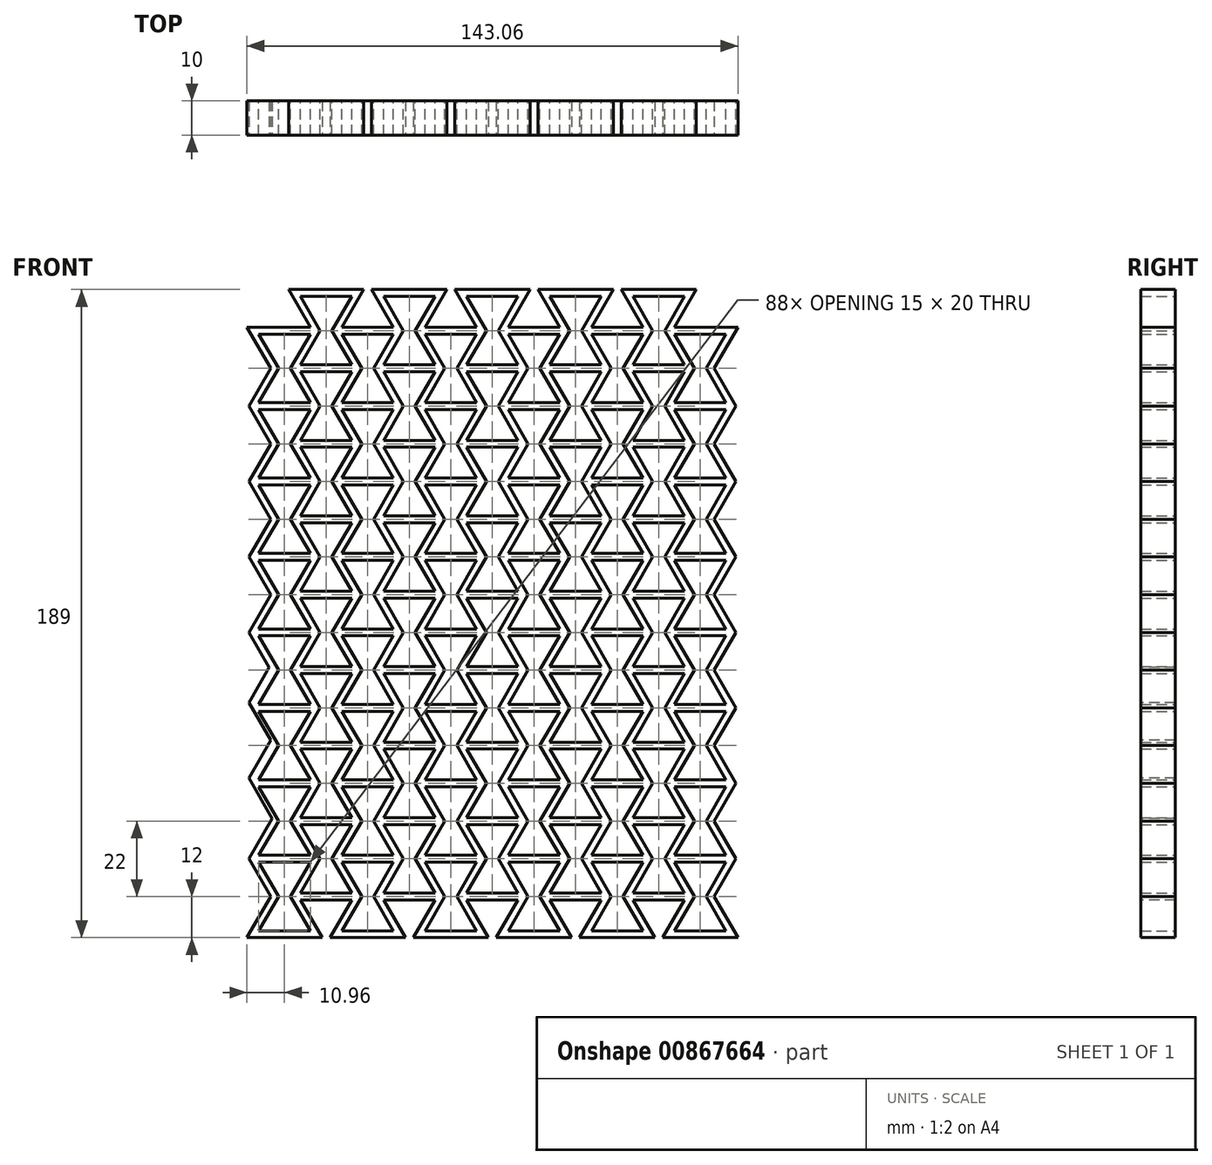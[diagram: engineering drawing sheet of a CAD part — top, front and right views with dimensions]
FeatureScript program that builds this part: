
annotation { "Feature Type Name" : "Feature", "Feature Type Description" : "" }
export const myFeature = defineFeature(function(context is Context, id is Id, definition is map)
    precondition{}
    {
        {
            var Q0;
            Q0=qCreatedBy(makeId("Front.planeOp"),FACE);
            var sketch = newSketch(context, id + "F0", { "sketchPlane" : qUnion([Q0])});
            skLineSegment(sketch, "E0", {"start": v(0, 0) * mm, "end": v(15, 0) * mm});
            skLineSegment(sketch, "E1", {"start": v(0, 20) * mm, "end": v(15, 20) * mm});
            skLineSegment(sketch, "E2", {"start": v(0, 20) * mm, "end": v(5.77, 10) * mm});
            skLineSegment(sketch, "E3", {"start": v(5.77, 10) * mm, "end": v(0, 0) * mm});
            skLineSegment(sketch, "E4", {"start": v(15, 20) * mm, "end": v(9.23, 10) * mm});
            skLineSegment(sketch, "E5", {"start": v(9.23, 10) * mm, "end": v(15, 0) * mm});
            skPoint(sketch, "E6", {"position": v(7.5, 21) * mm});
            skPoint(sketch, "E6.positionSnap0", {"position": v(7.5, 20) * mm});
            skPoint(sketch, "E7", {"position": v(7.5, -1) * mm});
            skPoint(sketch, "E7.positionSnap0", {"position": v(7.5, 0) * mm});
            skPoint(sketch, "E8", {"position": v(1.44, 4.5) * mm});
            skPoint(sketch, "E9", {"position": v(13.56, 4.5) * mm});
            skPoint(sketch, "E10", {"position": v(13.66, 15.67) * mm});
            skPoint(sketch, "E11", {"position": v(0.66, 16.85) * mm});
            skLineSegment(sketch, "E12", {"start": v(10.38, 10) * mm, "end": v(10.04, 10.6) * mm});
            skPoint(sketch, "E13", {"position": v(-1.73, 21) * mm});
            skPoint(sketch, "E14", {"position": v(16.73, 21) * mm});
            skPoint(sketch, "E15", {"position": v(4.62, 10) * mm});
            skPoint(sketch, "E16", {"position": v(10.38, 10) * mm});
            skPoint(sketch, "E17", {"position": v(-1.73, -1) * mm});
            skPoint(sketch, "E18", {"position": v(16.73, -1) * mm});
            skLineSegment(sketch, "E19", {"start": v(0, 22) * mm, "end": v(15, 22) * mm});
            skLineSegment(sketch, "E20", {"start": v(0, 42) * mm, "end": v(15, 42) * mm});
            skLineSegment(sketch, "E21", {"start": v(0, 42) * mm, "end": v(5.77, 32) * mm});
            skLineSegment(sketch, "E22", {"start": v(5.77, 32) * mm, "end": v(0, 22) * mm});
            skLineSegment(sketch, "E23", {"start": v(15, 42) * mm, "end": v(9.23, 32) * mm});
            skLineSegment(sketch, "E24", {"start": v(9.23, 32) * mm, "end": v(15, 22) * mm});
            skPoint(sketch, "E25", {"position": v(7.5, 43) * mm});
            skPoint(sketch, "E25.positionSnap0", {"position": v(7.5, 42) * mm});
            skPoint(sketch, "E26.positionSnap0", {"position": v(7.5, 22) * mm});
            skPoint(sketch, "E27", {"position": v(1.44, 26.5) * mm});
            skPoint(sketch, "E28", {"position": v(13.56, 26.5) * mm});
            skPoint(sketch, "E29", {"position": v(13.66, 37.67) * mm});
            skPoint(sketch, "E30", {"position": v(0.66, 38.85) * mm});
            skLineSegment(sketch, "E31", {"start": v(10.38, 32) * mm, "end": v(10.04, 32.6) * mm});
            skPoint(sketch, "E32", {"position": v(-1.73, 43) * mm});
            skPoint(sketch, "E33", {"position": v(16.73, 43) * mm});
            skPoint(sketch, "E34", {"position": v(4.62, 32) * mm});
            skPoint(sketch, "E35", {"position": v(10.38, 32) * mm});
            skLineSegment(sketch, "E36", {"start": v(0, 44) * mm, "end": v(15, 44) * mm});
            skLineSegment(sketch, "E37", {"start": v(0, 64) * mm, "end": v(15, 64) * mm});
            skLineSegment(sketch, "E38", {"start": v(0, 64) * mm, "end": v(5.77, 54) * mm});
            skLineSegment(sketch, "E39", {"start": v(5.77, 54) * mm, "end": v(0, 44) * mm});
            skLineSegment(sketch, "E40", {"start": v(15, 64) * mm, "end": v(9.23, 54) * mm});
            skLineSegment(sketch, "E41", {"start": v(9.23, 54) * mm, "end": v(15, 44) * mm});
            skPoint(sketch, "E42", {"position": v(7.5, 65) * mm});
            skPoint(sketch, "E42.positionSnap0", {"position": v(7.5, 64) * mm});
            skPoint(sketch, "E43.positionSnap0", {"position": v(7.5, 44) * mm});
            skPoint(sketch, "E44", {"position": v(1.44, 48.5) * mm});
            skPoint(sketch, "E45", {"position": v(13.56, 48.5) * mm});
            skPoint(sketch, "E46", {"position": v(13.66, 59.67) * mm});
            skPoint(sketch, "E47", {"position": v(0.66, 60.85) * mm});
            skLineSegment(sketch, "E48", {"start": v(10.38, 54) * mm, "end": v(10.04, 54.6) * mm});
            skPoint(sketch, "E49", {"position": v(-1.73, 65) * mm});
            skPoint(sketch, "E50", {"position": v(16.73, 65) * mm});
            skPoint(sketch, "E51", {"position": v(4.62, 54) * mm});
            skPoint(sketch, "E52", {"position": v(10.38, 54) * mm});
            skLineSegment(sketch, "E53", {"start": v(0, 66) * mm, "end": v(15, 66) * mm});
            skLineSegment(sketch, "E54", {"start": v(0, 86) * mm, "end": v(15, 86) * mm});
            skLineSegment(sketch, "E55", {"start": v(0, 86) * mm, "end": v(5.77, 76) * mm});
            skLineSegment(sketch, "E56", {"start": v(5.77, 76) * mm, "end": v(0, 66) * mm});
            skLineSegment(sketch, "E57", {"start": v(15, 86) * mm, "end": v(9.23, 76) * mm});
            skLineSegment(sketch, "E58", {"start": v(9.23, 76) * mm, "end": v(15, 66) * mm});
            skPoint(sketch, "E59", {"position": v(7.5, 87) * mm});
            skPoint(sketch, "E59.positionSnap0", {"position": v(7.5, 86) * mm});
            skPoint(sketch, "E60.positionSnap0", {"position": v(7.5, 66) * mm});
            skPoint(sketch, "E61", {"position": v(1.44, 70.5) * mm});
            skPoint(sketch, "E62", {"position": v(13.56, 70.5) * mm});
            skPoint(sketch, "E63", {"position": v(13.66, 81.67) * mm});
            skPoint(sketch, "E64", {"position": v(0.66, 82.85) * mm});
            skLineSegment(sketch, "E65", {"start": v(10.38, 76) * mm, "end": v(10.04, 76.6) * mm});
            skPoint(sketch, "E66", {"position": v(-1.73, 87) * mm});
            skPoint(sketch, "E67", {"position": v(16.73, 87) * mm});
            skPoint(sketch, "E68", {"position": v(4.62, 76) * mm});
            skPoint(sketch, "E69", {"position": v(10.38, 76) * mm});
            skLineSegment(sketch, "E70", {"start": v(0, 88) * mm, "end": v(15, 88) * mm});
            skLineSegment(sketch, "E71", {"start": v(0, 108) * mm, "end": v(15, 108) * mm});
            skLineSegment(sketch, "E72", {"start": v(0, 108) * mm, "end": v(5.77, 98) * mm});
            skLineSegment(sketch, "E73", {"start": v(5.77, 98) * mm, "end": v(0, 88) * mm});
            skLineSegment(sketch, "E74", {"start": v(15, 108) * mm, "end": v(9.23, 98) * mm});
            skLineSegment(sketch, "E75", {"start": v(9.23, 98) * mm, "end": v(15, 88) * mm});
            skPoint(sketch, "E76", {"position": v(7.5, 109) * mm});
            skPoint(sketch, "E76.positionSnap0", {"position": v(7.5, 108) * mm});
            skPoint(sketch, "E77.positionSnap0", {"position": v(7.5, 88) * mm});
            skPoint(sketch, "E78", {"position": v(1.44, 92.5) * mm});
            skPoint(sketch, "E79", {"position": v(13.56, 92.5) * mm});
            skPoint(sketch, "E80", {"position": v(13.66, 103.67) * mm});
            skPoint(sketch, "E81", {"position": v(0.66, 104.85) * mm});
            skLineSegment(sketch, "E82", {"start": v(10.38, 98) * mm, "end": v(10.04, 98.6) * mm});
            skPoint(sketch, "E83", {"position": v(-1.73, 109) * mm});
            skPoint(sketch, "E84", {"position": v(16.73, 109) * mm});
            skPoint(sketch, "E85", {"position": v(4.62, 98) * mm});
            skPoint(sketch, "E86", {"position": v(10.38, 98) * mm});
            skLineSegment(sketch, "E87", {"start": v(0, 110) * mm, "end": v(15, 110) * mm});
            skLineSegment(sketch, "E88", {"start": v(0, 130) * mm, "end": v(15, 130) * mm});
            skLineSegment(sketch, "E89", {"start": v(0, 130) * mm, "end": v(5.77, 120) * mm});
            skLineSegment(sketch, "E90", {"start": v(5.77, 120) * mm, "end": v(0, 110) * mm});
            skLineSegment(sketch, "E91", {"start": v(15, 130) * mm, "end": v(9.23, 120) * mm});
            skLineSegment(sketch, "E92", {"start": v(9.23, 120) * mm, "end": v(15, 110) * mm});
            skPoint(sketch, "E93", {"position": v(7.5, 131) * mm});
            skPoint(sketch, "E93.positionSnap0", {"position": v(7.5, 130) * mm});
            skPoint(sketch, "E94.positionSnap0", {"position": v(7.5, 110) * mm});
            skPoint(sketch, "E95", {"position": v(1.44, 114.5) * mm});
            skPoint(sketch, "E96", {"position": v(13.56, 114.5) * mm});
            skPoint(sketch, "E97", {"position": v(13.66, 125.67) * mm});
            skPoint(sketch, "E98", {"position": v(0.66, 126.85) * mm});
            skLineSegment(sketch, "E99", {"start": v(10.38, 120) * mm, "end": v(10.04, 120.6) * mm});
            skPoint(sketch, "E100", {"position": v(-1.73, 131) * mm});
            skPoint(sketch, "E101", {"position": v(16.73, 131) * mm});
            skPoint(sketch, "E102", {"position": v(4.62, 120) * mm});
            skPoint(sketch, "E103", {"position": v(10.38, 120) * mm});
            skLineSegment(sketch, "E104", {"start": v(0, 132) * mm, "end": v(15, 132) * mm});
            skLineSegment(sketch, "E105", {"start": v(0, 152) * mm, "end": v(15, 152) * mm});
            skLineSegment(sketch, "E106", {"start": v(0, 152) * mm, "end": v(5.77, 142) * mm});
            skLineSegment(sketch, "E107", {"start": v(5.77, 142) * mm, "end": v(0, 132) * mm});
            skLineSegment(sketch, "E108", {"start": v(15, 152) * mm, "end": v(9.23, 142) * mm});
            skLineSegment(sketch, "E109", {"start": v(9.23, 142) * mm, "end": v(15, 132) * mm});
            skPoint(sketch, "E110", {"position": v(7.5, 153) * mm});
            skPoint(sketch, "E110.positionSnap0", {"position": v(7.5, 152) * mm});
            skPoint(sketch, "E111.positionSnap0", {"position": v(7.5, 132) * mm});
            skPoint(sketch, "E112", {"position": v(1.44, 136.5) * mm});
            skPoint(sketch, "E113", {"position": v(13.56, 136.5) * mm});
            skPoint(sketch, "E114", {"position": v(13.66, 147.67) * mm});
            skPoint(sketch, "E115", {"position": v(0.66, 148.85) * mm});
            skLineSegment(sketch, "E116", {"start": v(10.38, 142) * mm, "end": v(10.04, 142.6) * mm});
            skPoint(sketch, "E117", {"position": v(-1.73, 153) * mm});
            skPoint(sketch, "E118", {"position": v(16.73, 153) * mm});
            skPoint(sketch, "E119", {"position": v(4.62, 142) * mm});
            skPoint(sketch, "E120", {"position": v(10.38, 142) * mm});
            skLineSegment(sketch, "E121", {"start": v(0, 154) * mm, "end": v(15, 154) * mm});
            skLineSegment(sketch, "E122", {"start": v(0, 174) * mm, "end": v(15, 174) * mm});
            skLineSegment(sketch, "E123", {"start": v(0, 174) * mm, "end": v(5.77, 164) * mm});
            skLineSegment(sketch, "E124", {"start": v(5.77, 164) * mm, "end": v(0, 154) * mm});
            skLineSegment(sketch, "E125", {"start": v(15, 174) * mm, "end": v(9.23, 164) * mm});
            skLineSegment(sketch, "E126", {"start": v(9.23, 164) * mm, "end": v(15, 154) * mm});
            skPoint(sketch, "E127", {"position": v(7.5, 175) * mm});
            skPoint(sketch, "E127.positionSnap0", {"position": v(7.5, 174) * mm});
            skPoint(sketch, "E128.positionSnap0", {"position": v(7.5, 154) * mm});
            skPoint(sketch, "E129", {"position": v(1.44, 158.5) * mm});
            skPoint(sketch, "E130", {"position": v(13.56, 158.5) * mm});
            skPoint(sketch, "E131", {"position": v(13.66, 169.67) * mm});
            skPoint(sketch, "E132", {"position": v(0.66, 170.85) * mm});
            skLineSegment(sketch, "E133", {"start": v(10.38, 164) * mm, "end": v(10.04, 164.6) * mm});
            skPoint(sketch, "E134", {"position": v(-1.73, 175) * mm});
            skPoint(sketch, "E135", {"position": v(16.73, 175) * mm});
            skPoint(sketch, "E136", {"position": v(4.62, 164) * mm});
            skPoint(sketch, "E137", {"position": v(10.38, 164) * mm});
            skLineSegment(sketch, "E138", {"start": v(12.11, 11) * mm, "end": v(27.11, 11) * mm});
            skLineSegment(sketch, "E139", {"start": v(12.11, 31) * mm, "end": v(27.11, 31) * mm});
            skLineSegment(sketch, "E140", {"start": v(12.11, 31) * mm, "end": v(17.89, 21) * mm});
            skLineSegment(sketch, "E141", {"start": v(17.89, 21) * mm, "end": v(12.11, 11) * mm});
            skLineSegment(sketch, "E142", {"start": v(27.11, 31) * mm, "end": v(21.34, 21) * mm});
            skLineSegment(sketch, "E143", {"start": v(21.34, 21) * mm, "end": v(27.11, 11) * mm});
            skPoint(sketch, "E144", {"position": v(19.61, 32) * mm});
            skPoint(sketch, "E144.positionSnap0", {"position": v(19.61, 31) * mm});
            skPoint(sketch, "E145", {"position": v(19.61, 10) * mm});
            skPoint(sketch, "E145.positionSnap0", {"position": v(19.61, 11) * mm});
            skPoint(sketch, "E146", {"position": v(13.55, 15.5) * mm});
            skPoint(sketch, "E147", {"position": v(25.67, 15.5) * mm});
            skPoint(sketch, "E148", {"position": v(25.77, 26.67) * mm});
            skPoint(sketch, "E149", {"position": v(12.78, 27.85) * mm});
            skLineSegment(sketch, "E150", {"start": v(22.5, 21) * mm, "end": v(22.15, 21.6) * mm});
            skPoint(sketch, "E151", {"position": v(28.85, 32) * mm});
            skPoint(sketch, "E152", {"position": v(22.5, 21) * mm});
            skPoint(sketch, "E153", {"position": v(28.85, 10) * mm});
            skLineSegment(sketch, "E154", {"start": v(12.11, 33) * mm, "end": v(27.11, 33) * mm});
            skLineSegment(sketch, "E155", {"start": v(12.11, 53) * mm, "end": v(27.11, 53) * mm});
            skLineSegment(sketch, "E156", {"start": v(12.11, 53) * mm, "end": v(17.89, 43) * mm});
            skLineSegment(sketch, "E157", {"start": v(17.89, 43) * mm, "end": v(12.11, 33) * mm});
            skLineSegment(sketch, "E158", {"start": v(27.11, 53) * mm, "end": v(21.34, 43) * mm});
            skLineSegment(sketch, "E159", {"start": v(21.34, 43) * mm, "end": v(27.11, 33) * mm});
            skPoint(sketch, "E160", {"position": v(19.61, 54) * mm});
            skPoint(sketch, "E160.positionSnap0", {"position": v(19.61, 53) * mm});
            skPoint(sketch, "E161.positionSnap0", {"position": v(19.61, 33) * mm});
            skPoint(sketch, "E162", {"position": v(13.55, 37.5) * mm});
            skPoint(sketch, "E163", {"position": v(25.67, 37.5) * mm});
            skPoint(sketch, "E164", {"position": v(25.77, 48.67) * mm});
            skPoint(sketch, "E165", {"position": v(12.78, 49.85) * mm});
            skLineSegment(sketch, "E166", {"start": v(22.5, 43) * mm, "end": v(22.15, 43.6) * mm});
            skPoint(sketch, "E167", {"position": v(28.85, 54) * mm});
            skPoint(sketch, "E168", {"position": v(22.5, 43) * mm});
            skLineSegment(sketch, "E169", {"start": v(12.11, 55) * mm, "end": v(27.11, 55) * mm});
            skLineSegment(sketch, "E170", {"start": v(12.11, 75) * mm, "end": v(27.11, 75) * mm});
            skLineSegment(sketch, "E171", {"start": v(12.11, 75) * mm, "end": v(17.89, 65) * mm});
            skLineSegment(sketch, "E172", {"start": v(17.89, 65) * mm, "end": v(12.11, 55) * mm});
            skLineSegment(sketch, "E173", {"start": v(27.11, 75) * mm, "end": v(21.34, 65) * mm});
            skLineSegment(sketch, "E174", {"start": v(21.34, 65) * mm, "end": v(27.11, 55) * mm});
            skPoint(sketch, "E175", {"position": v(19.61, 76) * mm});
            skPoint(sketch, "E175.positionSnap0", {"position": v(19.61, 75) * mm});
            skPoint(sketch, "E176.positionSnap0", {"position": v(19.61, 55) * mm});
            skPoint(sketch, "E177", {"position": v(13.55, 59.5) * mm});
            skPoint(sketch, "E178", {"position": v(25.67, 59.5) * mm});
            skPoint(sketch, "E179", {"position": v(25.77, 70.67) * mm});
            skPoint(sketch, "E180", {"position": v(12.78, 71.85) * mm});
            skLineSegment(sketch, "E181", {"start": v(22.5, 65) * mm, "end": v(22.15, 65.6) * mm});
            skPoint(sketch, "E182", {"position": v(28.85, 76) * mm});
            skPoint(sketch, "E183", {"position": v(22.5, 65) * mm});
            skLineSegment(sketch, "E184", {"start": v(12.11, 77) * mm, "end": v(27.11, 77) * mm});
            skLineSegment(sketch, "E185", {"start": v(12.11, 97) * mm, "end": v(27.11, 97) * mm});
            skLineSegment(sketch, "E186", {"start": v(12.11, 97) * mm, "end": v(17.89, 87) * mm});
            skLineSegment(sketch, "E187", {"start": v(17.89, 87) * mm, "end": v(12.11, 77) * mm});
            skLineSegment(sketch, "E188", {"start": v(27.11, 97) * mm, "end": v(21.34, 87) * mm});
            skLineSegment(sketch, "E189", {"start": v(21.34, 87) * mm, "end": v(27.11, 77) * mm});
            skPoint(sketch, "E190", {"position": v(19.61, 98) * mm});
            skPoint(sketch, "E190.positionSnap0", {"position": v(19.61, 97) * mm});
            skPoint(sketch, "E191.positionSnap0", {"position": v(19.61, 77) * mm});
            skPoint(sketch, "E192", {"position": v(13.55, 81.5) * mm});
            skPoint(sketch, "E193", {"position": v(25.67, 81.5) * mm});
            skPoint(sketch, "E194", {"position": v(25.77, 92.67) * mm});
            skPoint(sketch, "E195", {"position": v(12.78, 93.85) * mm});
            skLineSegment(sketch, "E196", {"start": v(22.5, 87) * mm, "end": v(22.15, 87.6) * mm});
            skPoint(sketch, "E197", {"position": v(28.85, 98) * mm});
            skPoint(sketch, "E198", {"position": v(22.5, 87) * mm});
            skLineSegment(sketch, "E199", {"start": v(12.11, 99) * mm, "end": v(27.11, 99) * mm});
            skLineSegment(sketch, "E200", {"start": v(12.11, 119) * mm, "end": v(27.11, 119) * mm});
            skLineSegment(sketch, "E201", {"start": v(12.11, 119) * mm, "end": v(17.89, 109) * mm});
            skLineSegment(sketch, "E202", {"start": v(17.89, 109) * mm, "end": v(12.11, 99) * mm});
            skLineSegment(sketch, "E203", {"start": v(27.11, 119) * mm, "end": v(21.34, 109) * mm});
            skLineSegment(sketch, "E204", {"start": v(21.34, 109) * mm, "end": v(27.11, 99) * mm});
            skPoint(sketch, "E205", {"position": v(19.61, 120) * mm});
            skPoint(sketch, "E205.positionSnap0", {"position": v(19.61, 119) * mm});
            skPoint(sketch, "E206.positionSnap0", {"position": v(19.61, 99) * mm});
            skPoint(sketch, "E207", {"position": v(13.55, 103.5) * mm});
            skPoint(sketch, "E208", {"position": v(25.67, 103.5) * mm});
            skPoint(sketch, "E209", {"position": v(25.77, 114.67) * mm});
            skPoint(sketch, "E210", {"position": v(12.78, 115.85) * mm});
            skLineSegment(sketch, "E211", {"start": v(22.5, 109) * mm, "end": v(22.15, 109.6) * mm});
            skPoint(sketch, "E212", {"position": v(28.85, 120) * mm});
            skPoint(sketch, "E213", {"position": v(22.5, 109) * mm});
            skLineSegment(sketch, "E214", {"start": v(12.11, 121) * mm, "end": v(27.11, 121) * mm});
            skLineSegment(sketch, "E215", {"start": v(12.11, 141) * mm, "end": v(27.11, 141) * mm});
            skLineSegment(sketch, "E216", {"start": v(12.11, 141) * mm, "end": v(17.89, 131) * mm});
            skLineSegment(sketch, "E217", {"start": v(17.89, 131) * mm, "end": v(12.11, 121) * mm});
            skLineSegment(sketch, "E218", {"start": v(27.11, 141) * mm, "end": v(21.34, 131) * mm});
            skLineSegment(sketch, "E219", {"start": v(21.34, 131) * mm, "end": v(27.11, 121) * mm});
            skPoint(sketch, "E220", {"position": v(19.61, 142) * mm});
            skPoint(sketch, "E220.positionSnap0", {"position": v(19.61, 141) * mm});
            skPoint(sketch, "E221.positionSnap0", {"position": v(19.61, 121) * mm});
            skPoint(sketch, "E222", {"position": v(13.55, 125.5) * mm});
            skPoint(sketch, "E223", {"position": v(25.67, 125.5) * mm});
            skPoint(sketch, "E224", {"position": v(25.77, 136.67) * mm});
            skPoint(sketch, "E225", {"position": v(12.78, 137.85) * mm});
            skLineSegment(sketch, "E226", {"start": v(22.5, 131) * mm, "end": v(22.15, 131.6) * mm});
            skPoint(sketch, "E227", {"position": v(28.85, 142) * mm});
            skPoint(sketch, "E228", {"position": v(22.5, 131) * mm});
            skLineSegment(sketch, "E229", {"start": v(12.11, 143) * mm, "end": v(27.11, 143) * mm});
            skLineSegment(sketch, "E230", {"start": v(12.11, 163) * mm, "end": v(27.11, 163) * mm});
            skLineSegment(sketch, "E231", {"start": v(12.11, 163) * mm, "end": v(17.89, 153) * mm});
            skLineSegment(sketch, "E232", {"start": v(17.89, 153) * mm, "end": v(12.11, 143) * mm});
            skLineSegment(sketch, "E233", {"start": v(27.11, 163) * mm, "end": v(21.34, 153) * mm});
            skLineSegment(sketch, "E234", {"start": v(21.34, 153) * mm, "end": v(27.11, 143) * mm});
            skPoint(sketch, "E235", {"position": v(19.61, 164) * mm});
            skPoint(sketch, "E235.positionSnap0", {"position": v(19.61, 163) * mm});
            skPoint(sketch, "E236.positionSnap0", {"position": v(19.61, 143) * mm});
            skPoint(sketch, "E237", {"position": v(13.55, 147.5) * mm});
            skPoint(sketch, "E238", {"position": v(25.67, 147.5) * mm});
            skPoint(sketch, "E239", {"position": v(25.77, 158.67) * mm});
            skPoint(sketch, "E240", {"position": v(12.78, 159.85) * mm});
            skLineSegment(sketch, "E241", {"start": v(22.5, 153) * mm, "end": v(22.15, 153.6) * mm});
            skPoint(sketch, "E242", {"position": v(28.85, 164) * mm});
            skPoint(sketch, "E243", {"position": v(22.5, 153) * mm});
            skLineSegment(sketch, "E244", {"start": v(12.11, 165) * mm, "end": v(27.11, 165) * mm});
            skLineSegment(sketch, "E245", {"start": v(12.11, 185) * mm, "end": v(27.11, 185) * mm});
            skLineSegment(sketch, "E246", {"start": v(12.11, 185) * mm, "end": v(17.89, 175) * mm});
            skLineSegment(sketch, "E247", {"start": v(17.89, 175) * mm, "end": v(12.11, 165) * mm});
            skLineSegment(sketch, "E248", {"start": v(27.11, 185) * mm, "end": v(21.34, 175) * mm});
            skLineSegment(sketch, "E249", {"start": v(21.34, 175) * mm, "end": v(27.11, 165) * mm});
            skPoint(sketch, "E250", {"position": v(19.61, 186) * mm});
            skPoint(sketch, "E250.positionSnap0", {"position": v(19.61, 185) * mm});
            skPoint(sketch, "E251.positionSnap0", {"position": v(19.61, 165) * mm});
            skPoint(sketch, "E252", {"position": v(13.55, 169.5) * mm});
            skPoint(sketch, "E253", {"position": v(25.67, 169.5) * mm});
            skPoint(sketch, "E254", {"position": v(25.77, 180.67) * mm});
            skPoint(sketch, "E255", {"position": v(12.78, 181.85) * mm});
            skLineSegment(sketch, "E256", {"start": v(22.5, 175) * mm, "end": v(22.15, 175.6) * mm});
            skPoint(sketch, "E257", {"position": v(10.38, 186) * mm});
            skPoint(sketch, "E258", {"position": v(28.85, 186) * mm});
            skPoint(sketch, "E259", {"position": v(22.5, 175) * mm});
            skLineSegment(sketch, "E260", {"start": v(24.23, 0) * mm, "end": v(39.23, 0) * mm});
            skLineSegment(sketch, "E261", {"start": v(24.23, 20) * mm, "end": v(39.23, 20) * mm});
            skLineSegment(sketch, "E262", {"start": v(24.23, 20) * mm, "end": v(30, 10) * mm});
            skLineSegment(sketch, "E263", {"start": v(30, 10) * mm, "end": v(24.23, 0) * mm});
            skLineSegment(sketch, "E264", {"start": v(39.23, 20) * mm, "end": v(33.45, 10) * mm});
            skLineSegment(sketch, "E265", {"start": v(33.45, 10) * mm, "end": v(39.23, 0) * mm});
            skPoint(sketch, "E266", {"position": v(31.73, 21) * mm});
            skPoint(sketch, "E266.positionSnap0", {"position": v(31.73, 20) * mm});
            skPoint(sketch, "E267", {"position": v(31.73, -1) * mm});
            skPoint(sketch, "E267.positionSnap0", {"position": v(31.73, 0) * mm});
            skPoint(sketch, "E268", {"position": v(25.67, 4.5) * mm});
            skPoint(sketch, "E269", {"position": v(37.79, 4.5) * mm});
            skPoint(sketch, "E270", {"position": v(37.88, 15.67) * mm});
            skPoint(sketch, "E271", {"position": v(24.9, 16.85) * mm});
            skLineSegment(sketch, "E272", {"start": v(34.6, 10) * mm, "end": v(34.26, 10.6) * mm});
            skPoint(sketch, "E273", {"position": v(40.96, 21) * mm});
            skPoint(sketch, "E274", {"position": v(34.6, 10) * mm});
            skPoint(sketch, "E275", {"position": v(22.5, -1) * mm});
            skPoint(sketch, "E276", {"position": v(40.96, -1) * mm});
            skLineSegment(sketch, "E277", {"start": v(24.23, 22) * mm, "end": v(39.23, 22) * mm});
            skLineSegment(sketch, "E278", {"start": v(24.23, 42) * mm, "end": v(39.23, 42) * mm});
            skLineSegment(sketch, "E279", {"start": v(24.23, 42) * mm, "end": v(30, 32) * mm});
            skLineSegment(sketch, "E280", {"start": v(30, 32) * mm, "end": v(24.23, 22) * mm});
            skLineSegment(sketch, "E281", {"start": v(39.23, 42) * mm, "end": v(33.45, 32) * mm});
            skLineSegment(sketch, "E282", {"start": v(33.45, 32) * mm, "end": v(39.23, 22) * mm});
            skPoint(sketch, "E283", {"position": v(31.73, 43) * mm});
            skPoint(sketch, "E283.positionSnap0", {"position": v(31.73, 42) * mm});
            skPoint(sketch, "E284.positionSnap0", {"position": v(31.73, 22) * mm});
            skPoint(sketch, "E285", {"position": v(25.67, 26.5) * mm});
            skPoint(sketch, "E286", {"position": v(37.79, 26.5) * mm});
            skPoint(sketch, "E287", {"position": v(37.88, 37.67) * mm});
            skPoint(sketch, "E288", {"position": v(24.9, 38.85) * mm});
            skLineSegment(sketch, "E289", {"start": v(34.6, 32) * mm, "end": v(34.26, 32.6) * mm});
            skPoint(sketch, "E290", {"position": v(40.96, 43) * mm});
            skPoint(sketch, "E291", {"position": v(34.6, 32) * mm});
            skLineSegment(sketch, "E292", {"start": v(24.23, 44) * mm, "end": v(39.23, 44) * mm});
            skLineSegment(sketch, "E293", {"start": v(24.23, 64) * mm, "end": v(39.23, 64) * mm});
            skLineSegment(sketch, "E294", {"start": v(24.23, 64) * mm, "end": v(30, 54) * mm});
            skLineSegment(sketch, "E295", {"start": v(30, 54) * mm, "end": v(24.23, 44) * mm});
            skLineSegment(sketch, "E296", {"start": v(39.23, 64) * mm, "end": v(33.45, 54) * mm});
            skLineSegment(sketch, "E297", {"start": v(33.45, 54) * mm, "end": v(39.23, 44) * mm});
            skPoint(sketch, "E298", {"position": v(31.73, 65) * mm});
            skPoint(sketch, "E298.positionSnap0", {"position": v(31.73, 64) * mm});
            skPoint(sketch, "E299.positionSnap0", {"position": v(31.73, 44) * mm});
            skPoint(sketch, "E300", {"position": v(25.67, 48.5) * mm});
            skPoint(sketch, "E301", {"position": v(37.79, 48.5) * mm});
            skPoint(sketch, "E302", {"position": v(37.88, 59.67) * mm});
            skPoint(sketch, "E303", {"position": v(24.9, 60.85) * mm});
            skLineSegment(sketch, "E304", {"start": v(34.6, 54) * mm, "end": v(34.26, 54.6) * mm});
            skPoint(sketch, "E305", {"position": v(40.96, 65) * mm});
            skPoint(sketch, "E306", {"position": v(34.6, 54) * mm});
            skLineSegment(sketch, "E307", {"start": v(24.23, 66) * mm, "end": v(39.23, 66) * mm});
            skLineSegment(sketch, "E308", {"start": v(24.23, 86) * mm, "end": v(39.23, 86) * mm});
            skLineSegment(sketch, "E309", {"start": v(24.23, 86) * mm, "end": v(30, 76) * mm});
            skLineSegment(sketch, "E310", {"start": v(30, 76) * mm, "end": v(24.23, 66) * mm});
            skLineSegment(sketch, "E311", {"start": v(39.23, 86) * mm, "end": v(33.45, 76) * mm});
            skLineSegment(sketch, "E312", {"start": v(33.45, 76) * mm, "end": v(39.23, 66) * mm});
            skPoint(sketch, "E313", {"position": v(31.73, 87) * mm});
            skPoint(sketch, "E313.positionSnap0", {"position": v(31.73, 86) * mm});
            skPoint(sketch, "E314.positionSnap0", {"position": v(31.73, 66) * mm});
            skPoint(sketch, "E315", {"position": v(25.67, 70.5) * mm});
            skPoint(sketch, "E316", {"position": v(37.79, 70.5) * mm});
            skPoint(sketch, "E317", {"position": v(37.88, 81.67) * mm});
            skPoint(sketch, "E318", {"position": v(24.9, 82.85) * mm});
            skLineSegment(sketch, "E319", {"start": v(34.6, 76) * mm, "end": v(34.26, 76.6) * mm});
            skPoint(sketch, "E320", {"position": v(40.96, 87) * mm});
            skPoint(sketch, "E321", {"position": v(34.6, 76) * mm});
            skLineSegment(sketch, "E322", {"start": v(24.23, 88) * mm, "end": v(39.23, 88) * mm});
            skLineSegment(sketch, "E323", {"start": v(24.23, 108) * mm, "end": v(39.23, 108) * mm});
            skLineSegment(sketch, "E324", {"start": v(24.23, 108) * mm, "end": v(30, 98) * mm});
            skLineSegment(sketch, "E325", {"start": v(30, 98) * mm, "end": v(24.23, 88) * mm});
            skLineSegment(sketch, "E326", {"start": v(39.23, 108) * mm, "end": v(33.45, 98) * mm});
            skLineSegment(sketch, "E327", {"start": v(33.45, 98) * mm, "end": v(39.23, 88) * mm});
            skPoint(sketch, "E328", {"position": v(31.73, 109) * mm});
            skPoint(sketch, "E328.positionSnap0", {"position": v(31.73, 108) * mm});
            skPoint(sketch, "E329.positionSnap0", {"position": v(31.73, 88) * mm});
            skPoint(sketch, "E330", {"position": v(25.67, 92.5) * mm});
            skPoint(sketch, "E331", {"position": v(37.79, 92.5) * mm});
            skPoint(sketch, "E332", {"position": v(37.88, 103.67) * mm});
            skPoint(sketch, "E333", {"position": v(24.9, 104.85) * mm});
            skLineSegment(sketch, "E334", {"start": v(34.6, 98) * mm, "end": v(34.26, 98.6) * mm});
            skPoint(sketch, "E335", {"position": v(40.96, 109) * mm});
            skPoint(sketch, "E336", {"position": v(34.6, 98) * mm});
            skLineSegment(sketch, "E337", {"start": v(24.23, 110) * mm, "end": v(39.23, 110) * mm});
            skLineSegment(sketch, "E338", {"start": v(24.23, 130) * mm, "end": v(39.23, 130) * mm});
            skLineSegment(sketch, "E339", {"start": v(24.23, 130) * mm, "end": v(30, 120) * mm});
            skLineSegment(sketch, "E340", {"start": v(30, 120) * mm, "end": v(24.23, 110) * mm});
            skLineSegment(sketch, "E341", {"start": v(39.23, 130) * mm, "end": v(33.45, 120) * mm});
            skLineSegment(sketch, "E342", {"start": v(33.45, 120) * mm, "end": v(39.23, 110) * mm});
            skPoint(sketch, "E343", {"position": v(31.73, 131) * mm});
            skPoint(sketch, "E343.positionSnap0", {"position": v(31.73, 130) * mm});
            skPoint(sketch, "E344.positionSnap0", {"position": v(31.73, 110) * mm});
            skPoint(sketch, "E345", {"position": v(25.67, 114.5) * mm});
            skPoint(sketch, "E346", {"position": v(37.79, 114.5) * mm});
            skPoint(sketch, "E347", {"position": v(37.88, 125.67) * mm});
            skPoint(sketch, "E348", {"position": v(24.9, 126.85) * mm});
            skLineSegment(sketch, "E349", {"start": v(34.6, 120) * mm, "end": v(34.26, 120.6) * mm});
            skPoint(sketch, "E350", {"position": v(40.96, 131) * mm});
            skPoint(sketch, "E351", {"position": v(34.6, 120) * mm});
            skLineSegment(sketch, "E352", {"start": v(24.23, 132) * mm, "end": v(39.23, 132) * mm});
            skLineSegment(sketch, "E353", {"start": v(24.23, 152) * mm, "end": v(39.23, 152) * mm});
            skLineSegment(sketch, "E354", {"start": v(24.23, 152) * mm, "end": v(30, 142) * mm});
            skLineSegment(sketch, "E355", {"start": v(30, 142) * mm, "end": v(24.23, 132) * mm});
            skLineSegment(sketch, "E356", {"start": v(39.23, 152) * mm, "end": v(33.45, 142) * mm});
            skLineSegment(sketch, "E357", {"start": v(33.45, 142) * mm, "end": v(39.23, 132) * mm});
            skPoint(sketch, "E358", {"position": v(31.73, 153) * mm});
            skPoint(sketch, "E358.positionSnap0", {"position": v(31.73, 152) * mm});
            skPoint(sketch, "E359.positionSnap0", {"position": v(31.73, 132) * mm});
            skPoint(sketch, "E360", {"position": v(25.67, 136.5) * mm});
            skPoint(sketch, "E361", {"position": v(37.79, 136.5) * mm});
            skPoint(sketch, "E362", {"position": v(37.88, 147.67) * mm});
            skPoint(sketch, "E363", {"position": v(24.9, 148.85) * mm});
            skLineSegment(sketch, "E364", {"start": v(34.6, 142) * mm, "end": v(34.26, 142.6) * mm});
            skPoint(sketch, "E365", {"position": v(40.96, 153) * mm});
            skPoint(sketch, "E366", {"position": v(34.6, 142) * mm});
            skLineSegment(sketch, "E367", {"start": v(24.23, 154) * mm, "end": v(39.23, 154) * mm});
            skLineSegment(sketch, "E368", {"start": v(24.23, 174) * mm, "end": v(39.23, 174) * mm});
            skLineSegment(sketch, "E369", {"start": v(24.23, 174) * mm, "end": v(30, 164) * mm});
            skLineSegment(sketch, "E370", {"start": v(30, 164) * mm, "end": v(24.23, 154) * mm});
            skLineSegment(sketch, "E371", {"start": v(39.23, 174) * mm, "end": v(33.45, 164) * mm});
            skLineSegment(sketch, "E372", {"start": v(33.45, 164) * mm, "end": v(39.23, 154) * mm});
            skPoint(sketch, "E373", {"position": v(31.73, 175) * mm});
            skPoint(sketch, "E373.positionSnap0", {"position": v(31.73, 174) * mm});
            skPoint(sketch, "E374.positionSnap0", {"position": v(31.73, 154) * mm});
            skPoint(sketch, "E375", {"position": v(25.67, 158.5) * mm});
            skPoint(sketch, "E376", {"position": v(37.79, 158.5) * mm});
            skPoint(sketch, "E377", {"position": v(37.88, 169.67) * mm});
            skPoint(sketch, "E378", {"position": v(24.9, 170.85) * mm});
            skLineSegment(sketch, "E379", {"start": v(34.6, 164) * mm, "end": v(34.26, 164.6) * mm});
            skPoint(sketch, "E380", {"position": v(40.96, 175) * mm});
            skPoint(sketch, "E381", {"position": v(34.6, 164) * mm});
            skLineSegment(sketch, "E382", {"start": v(36.34, 11) * mm, "end": v(51.34, 11) * mm});
            skLineSegment(sketch, "E383", {"start": v(36.34, 31) * mm, "end": v(51.34, 31) * mm});
            skLineSegment(sketch, "E384", {"start": v(36.34, 31) * mm, "end": v(42.11, 21) * mm});
            skLineSegment(sketch, "E385", {"start": v(42.11, 21) * mm, "end": v(36.34, 11) * mm});
            skLineSegment(sketch, "E386", {"start": v(51.34, 31) * mm, "end": v(45.57, 21) * mm});
            skLineSegment(sketch, "E387", {"start": v(45.57, 21) * mm, "end": v(51.34, 11) * mm});
            skPoint(sketch, "E388", {"position": v(43.84, 32) * mm});
            skPoint(sketch, "E388.positionSnap0", {"position": v(43.84, 31) * mm});
            skPoint(sketch, "E389", {"position": v(43.84, 10) * mm});
            skPoint(sketch, "E389.positionSnap0", {"position": v(43.84, 11) * mm});
            skPoint(sketch, "E390", {"position": v(37.78, 15.5) * mm});
            skPoint(sketch, "E391", {"position": v(49.9, 15.5) * mm});
            skPoint(sketch, "E392", {"position": v(50, 26.67) * mm});
            skPoint(sketch, "E393", {"position": v(37, 27.85) * mm});
            skLineSegment(sketch, "E394", {"start": v(46.72, 21) * mm, "end": v(46.37, 21.6) * mm});
            skPoint(sketch, "E395", {"position": v(53.07, 32) * mm});
            skPoint(sketch, "E396", {"position": v(46.72, 21) * mm});
            skPoint(sketch, "E397", {"position": v(53.07, 10) * mm});
            skLineSegment(sketch, "E398", {"start": v(36.34, 33) * mm, "end": v(51.34, 33) * mm});
            skLineSegment(sketch, "E399", {"start": v(36.34, 53) * mm, "end": v(51.34, 53) * mm});
            skLineSegment(sketch, "E400", {"start": v(36.34, 53) * mm, "end": v(42.11, 43) * mm});
            skLineSegment(sketch, "E401", {"start": v(42.11, 43) * mm, "end": v(36.34, 33) * mm});
            skLineSegment(sketch, "E402", {"start": v(51.34, 53) * mm, "end": v(45.57, 43) * mm});
            skLineSegment(sketch, "E403", {"start": v(45.57, 43) * mm, "end": v(51.34, 33) * mm});
            skPoint(sketch, "E404", {"position": v(43.84, 54) * mm});
            skPoint(sketch, "E404.positionSnap0", {"position": v(43.84, 53) * mm});
            skPoint(sketch, "E405.positionSnap0", {"position": v(43.84, 33) * mm});
            skPoint(sketch, "E406", {"position": v(37.78, 37.5) * mm});
            skPoint(sketch, "E407", {"position": v(49.9, 37.5) * mm});
            skPoint(sketch, "E408", {"position": v(50, 48.67) * mm});
            skPoint(sketch, "E409", {"position": v(37, 49.85) * mm});
            skLineSegment(sketch, "E410", {"start": v(46.72, 43) * mm, "end": v(46.37, 43.6) * mm});
            skPoint(sketch, "E411", {"position": v(53.07, 54) * mm});
            skPoint(sketch, "E412", {"position": v(46.72, 43) * mm});
            skLineSegment(sketch, "E413", {"start": v(36.34, 55) * mm, "end": v(51.34, 55) * mm});
            skLineSegment(sketch, "E414", {"start": v(36.34, 75) * mm, "end": v(51.34, 75) * mm});
            skLineSegment(sketch, "E415", {"start": v(36.34, 75) * mm, "end": v(42.11, 65) * mm});
            skLineSegment(sketch, "E416", {"start": v(42.11, 65) * mm, "end": v(36.34, 55) * mm});
            skLineSegment(sketch, "E417", {"start": v(51.34, 75) * mm, "end": v(45.57, 65) * mm});
            skLineSegment(sketch, "E418", {"start": v(45.57, 65) * mm, "end": v(51.34, 55) * mm});
            skPoint(sketch, "E419", {"position": v(43.84, 76) * mm});
            skPoint(sketch, "E419.positionSnap0", {"position": v(43.84, 75) * mm});
            skPoint(sketch, "E420.positionSnap0", {"position": v(43.84, 55) * mm});
            skPoint(sketch, "E421", {"position": v(37.78, 59.5) * mm});
            skPoint(sketch, "E422", {"position": v(49.9, 59.5) * mm});
            skPoint(sketch, "E423", {"position": v(50, 70.67) * mm});
            skPoint(sketch, "E424", {"position": v(37, 71.85) * mm});
            skLineSegment(sketch, "E425", {"start": v(46.72, 65) * mm, "end": v(46.37, 65.6) * mm});
            skPoint(sketch, "E426", {"position": v(53.07, 76) * mm});
            skPoint(sketch, "E427", {"position": v(46.72, 65) * mm});
            skLineSegment(sketch, "E428", {"start": v(36.34, 77) * mm, "end": v(51.34, 77) * mm});
            skLineSegment(sketch, "E429", {"start": v(36.34, 97) * mm, "end": v(51.34, 97) * mm});
            skLineSegment(sketch, "E430", {"start": v(36.34, 97) * mm, "end": v(42.11, 87) * mm});
            skLineSegment(sketch, "E431", {"start": v(42.11, 87) * mm, "end": v(36.34, 77) * mm});
            skLineSegment(sketch, "E432", {"start": v(51.34, 97) * mm, "end": v(45.57, 87) * mm});
            skLineSegment(sketch, "E433", {"start": v(45.57, 87) * mm, "end": v(51.34, 77) * mm});
            skPoint(sketch, "E434", {"position": v(43.84, 98) * mm});
            skPoint(sketch, "E434.positionSnap0", {"position": v(43.84, 97) * mm});
            skPoint(sketch, "E435.positionSnap0", {"position": v(43.84, 77) * mm});
            skPoint(sketch, "E436", {"position": v(37.78, 81.5) * mm});
            skPoint(sketch, "E437", {"position": v(49.9, 81.5) * mm});
            skPoint(sketch, "E438", {"position": v(50, 92.67) * mm});
            skPoint(sketch, "E439", {"position": v(37, 93.85) * mm});
            skLineSegment(sketch, "E440", {"start": v(46.72, 87) * mm, "end": v(46.37, 87.6) * mm});
            skPoint(sketch, "E441", {"position": v(53.07, 98) * mm});
            skPoint(sketch, "E442", {"position": v(46.72, 87) * mm});
            skLineSegment(sketch, "E443", {"start": v(36.34, 99) * mm, "end": v(51.34, 99) * mm});
            skLineSegment(sketch, "E444", {"start": v(36.34, 119) * mm, "end": v(51.34, 119) * mm});
            skLineSegment(sketch, "E445", {"start": v(36.34, 119) * mm, "end": v(42.11, 109) * mm});
            skLineSegment(sketch, "E446", {"start": v(42.11, 109) * mm, "end": v(36.34, 99) * mm});
            skLineSegment(sketch, "E447", {"start": v(51.34, 119) * mm, "end": v(45.57, 109) * mm});
            skLineSegment(sketch, "E448", {"start": v(45.57, 109) * mm, "end": v(51.34, 99) * mm});
            skPoint(sketch, "E449", {"position": v(43.84, 120) * mm});
            skPoint(sketch, "E449.positionSnap0", {"position": v(43.84, 119) * mm});
            skPoint(sketch, "E450.positionSnap0", {"position": v(43.84, 99) * mm});
            skPoint(sketch, "E451", {"position": v(37.78, 103.5) * mm});
            skPoint(sketch, "E452", {"position": v(49.9, 103.5) * mm});
            skPoint(sketch, "E453", {"position": v(50, 114.67) * mm});
            skPoint(sketch, "E454", {"position": v(37, 115.85) * mm});
            skLineSegment(sketch, "E455", {"start": v(46.72, 109) * mm, "end": v(46.37, 109.6) * mm});
            skPoint(sketch, "E456", {"position": v(53.07, 120) * mm});
            skPoint(sketch, "E457", {"position": v(46.72, 109) * mm});
            skLineSegment(sketch, "E458", {"start": v(36.34, 121) * mm, "end": v(51.34, 121) * mm});
            skLineSegment(sketch, "E459", {"start": v(36.34, 141) * mm, "end": v(51.34, 141) * mm});
            skLineSegment(sketch, "E460", {"start": v(36.34, 141) * mm, "end": v(42.11, 131) * mm});
            skLineSegment(sketch, "E461", {"start": v(42.11, 131) * mm, "end": v(36.34, 121) * mm});
            skLineSegment(sketch, "E462", {"start": v(51.34, 141) * mm, "end": v(45.57, 131) * mm});
            skLineSegment(sketch, "E463", {"start": v(45.57, 131) * mm, "end": v(51.34, 121) * mm});
            skPoint(sketch, "E464", {"position": v(43.84, 142) * mm});
            skPoint(sketch, "E464.positionSnap0", {"position": v(43.84, 141) * mm});
            skPoint(sketch, "E465.positionSnap0", {"position": v(43.84, 121) * mm});
            skPoint(sketch, "E466", {"position": v(37.78, 125.5) * mm});
            skPoint(sketch, "E467", {"position": v(49.9, 125.5) * mm});
            skPoint(sketch, "E468", {"position": v(50, 136.67) * mm});
            skPoint(sketch, "E469", {"position": v(37, 137.85) * mm});
            skLineSegment(sketch, "E470", {"start": v(46.72, 131) * mm, "end": v(46.37, 131.6) * mm});
            skPoint(sketch, "E471", {"position": v(53.07, 142) * mm});
            skPoint(sketch, "E472", {"position": v(46.72, 131) * mm});
            skLineSegment(sketch, "E473", {"start": v(36.34, 143) * mm, "end": v(51.34, 143) * mm});
            skLineSegment(sketch, "E474", {"start": v(36.34, 163) * mm, "end": v(51.34, 163) * mm});
            skLineSegment(sketch, "E475", {"start": v(36.34, 163) * mm, "end": v(42.11, 153) * mm});
            skLineSegment(sketch, "E476", {"start": v(42.11, 153) * mm, "end": v(36.34, 143) * mm});
            skLineSegment(sketch, "E477", {"start": v(51.34, 163) * mm, "end": v(45.57, 153) * mm});
            skLineSegment(sketch, "E478", {"start": v(45.57, 153) * mm, "end": v(51.34, 143) * mm});
            skPoint(sketch, "E479", {"position": v(43.84, 164) * mm});
            skPoint(sketch, "E479.positionSnap0", {"position": v(43.84, 163) * mm});
            skPoint(sketch, "E480.positionSnap0", {"position": v(43.84, 143) * mm});
            skPoint(sketch, "E481", {"position": v(37.78, 147.5) * mm});
            skPoint(sketch, "E482", {"position": v(49.9, 147.5) * mm});
            skPoint(sketch, "E483", {"position": v(50, 158.67) * mm});
            skPoint(sketch, "E484", {"position": v(37, 159.85) * mm});
            skLineSegment(sketch, "E485", {"start": v(46.72, 153) * mm, "end": v(46.37, 153.6) * mm});
            skPoint(sketch, "E486", {"position": v(53.07, 164) * mm});
            skPoint(sketch, "E487", {"position": v(46.72, 153) * mm});
            skLineSegment(sketch, "E488", {"start": v(36.34, 165) * mm, "end": v(51.34, 165) * mm});
            skLineSegment(sketch, "E489", {"start": v(36.34, 185) * mm, "end": v(51.34, 185) * mm});
            skLineSegment(sketch, "E490", {"start": v(36.34, 185) * mm, "end": v(42.11, 175) * mm});
            skLineSegment(sketch, "E491", {"start": v(42.11, 175) * mm, "end": v(36.34, 165) * mm});
            skLineSegment(sketch, "E492", {"start": v(51.34, 185) * mm, "end": v(45.57, 175) * mm});
            skLineSegment(sketch, "E493", {"start": v(45.57, 175) * mm, "end": v(51.34, 165) * mm});
            skPoint(sketch, "E494", {"position": v(43.84, 186) * mm});
            skPoint(sketch, "E494.positionSnap0", {"position": v(43.84, 185) * mm});
            skPoint(sketch, "E495.positionSnap0", {"position": v(43.84, 165) * mm});
            skPoint(sketch, "E496", {"position": v(37.78, 169.5) * mm});
            skPoint(sketch, "E497", {"position": v(49.9, 169.5) * mm});
            skPoint(sketch, "E498", {"position": v(50, 180.67) * mm});
            skPoint(sketch, "E499", {"position": v(37, 181.85) * mm});
            skLineSegment(sketch, "E500", {"start": v(46.72, 175) * mm, "end": v(46.37, 175.6) * mm});
            skPoint(sketch, "E501", {"position": v(34.6, 186) * mm});
            skPoint(sketch, "E502", {"position": v(53.07, 186) * mm});
            skPoint(sketch, "E503", {"position": v(46.72, 175) * mm});
            skLineSegment(sketch, "E504", {"start": v(48.45, 0) * mm, "end": v(63.45, 0) * mm});
            skLineSegment(sketch, "E505", {"start": v(48.45, 20) * mm, "end": v(63.45, 20) * mm});
            skLineSegment(sketch, "E506", {"start": v(48.45, 20) * mm, "end": v(54.23, 10) * mm});
            skLineSegment(sketch, "E507", {"start": v(54.23, 10) * mm, "end": v(48.45, 0) * mm});
            skLineSegment(sketch, "E508", {"start": v(63.45, 20) * mm, "end": v(57.68, 10) * mm});
            skLineSegment(sketch, "E509", {"start": v(57.68, 10) * mm, "end": v(63.45, 0) * mm});
            skPoint(sketch, "E510", {"position": v(55.95, 21) * mm});
            skPoint(sketch, "E510.positionSnap0", {"position": v(55.95, 20) * mm});
            skPoint(sketch, "E511", {"position": v(55.95, -1) * mm});
            skPoint(sketch, "E511.positionSnap0", {"position": v(55.95, 0) * mm});
            skPoint(sketch, "E512", {"position": v(49.9, 4.5) * mm});
            skPoint(sketch, "E513", {"position": v(62.01, 4.5) * mm});
            skPoint(sketch, "E514", {"position": v(62.1, 15.67) * mm});
            skPoint(sketch, "E515", {"position": v(49.12, 16.85) * mm});
            skLineSegment(sketch, "E516", {"start": v(58.83, 10) * mm, "end": v(58.49, 10.6) * mm});
            skPoint(sketch, "E517", {"position": v(65.19, 21) * mm});
            skPoint(sketch, "E518", {"position": v(58.83, 10) * mm});
            skPoint(sketch, "E519", {"position": v(46.72, -1) * mm});
            skPoint(sketch, "E520", {"position": v(65.19, -1) * mm});
            skLineSegment(sketch, "E521", {"start": v(48.45, 22) * mm, "end": v(63.45, 22) * mm});
            skLineSegment(sketch, "E522", {"start": v(48.45, 42) * mm, "end": v(63.45, 42) * mm});
            skLineSegment(sketch, "E523", {"start": v(48.45, 42) * mm, "end": v(54.23, 32) * mm});
            skLineSegment(sketch, "E524", {"start": v(54.23, 32) * mm, "end": v(48.45, 22) * mm});
            skLineSegment(sketch, "E525", {"start": v(63.45, 42) * mm, "end": v(57.68, 32) * mm});
            skLineSegment(sketch, "E526", {"start": v(57.68, 32) * mm, "end": v(63.45, 22) * mm});
            skPoint(sketch, "E527", {"position": v(55.95, 43) * mm});
            skPoint(sketch, "E527.positionSnap0", {"position": v(55.95, 42) * mm});
            skPoint(sketch, "E528.positionSnap0", {"position": v(55.95, 22) * mm});
            skPoint(sketch, "E529", {"position": v(49.9, 26.5) * mm});
            skPoint(sketch, "E530", {"position": v(62.01, 26.5) * mm});
            skPoint(sketch, "E531", {"position": v(62.1, 37.67) * mm});
            skPoint(sketch, "E532", {"position": v(49.12, 38.85) * mm});
            skLineSegment(sketch, "E533", {"start": v(58.83, 32) * mm, "end": v(58.49, 32.6) * mm});
            skPoint(sketch, "E534", {"position": v(65.19, 43) * mm});
            skPoint(sketch, "E535", {"position": v(58.83, 32) * mm});
            skLineSegment(sketch, "E536", {"start": v(48.45, 44) * mm, "end": v(63.45, 44) * mm});
            skLineSegment(sketch, "E537", {"start": v(48.45, 64) * mm, "end": v(63.45, 64) * mm});
            skLineSegment(sketch, "E538", {"start": v(48.45, 64) * mm, "end": v(54.23, 54) * mm});
            skLineSegment(sketch, "E539", {"start": v(54.23, 54) * mm, "end": v(48.45, 44) * mm});
            skLineSegment(sketch, "E540", {"start": v(63.45, 64) * mm, "end": v(57.68, 54) * mm});
            skLineSegment(sketch, "E541", {"start": v(57.68, 54) * mm, "end": v(63.45, 44) * mm});
            skPoint(sketch, "E542", {"position": v(55.95, 65) * mm});
            skPoint(sketch, "E542.positionSnap0", {"position": v(55.95, 64) * mm});
            skPoint(sketch, "E543.positionSnap0", {"position": v(55.95, 44) * mm});
            skPoint(sketch, "E544", {"position": v(49.9, 48.5) * mm});
            skPoint(sketch, "E545", {"position": v(62.01, 48.5) * mm});
            skPoint(sketch, "E546", {"position": v(62.1, 59.67) * mm});
            skPoint(sketch, "E547", {"position": v(49.12, 60.85) * mm});
            skLineSegment(sketch, "E548", {"start": v(58.83, 54) * mm, "end": v(58.49, 54.6) * mm});
            skPoint(sketch, "E549", {"position": v(65.19, 65) * mm});
            skPoint(sketch, "E550", {"position": v(58.83, 54) * mm});
            skLineSegment(sketch, "E551", {"start": v(48.45, 66) * mm, "end": v(63.45, 66) * mm});
            skLineSegment(sketch, "E552", {"start": v(48.45, 86) * mm, "end": v(63.45, 86) * mm});
            skLineSegment(sketch, "E553", {"start": v(48.45, 86) * mm, "end": v(54.23, 76) * mm});
            skLineSegment(sketch, "E554", {"start": v(54.23, 76) * mm, "end": v(48.45, 66) * mm});
            skLineSegment(sketch, "E555", {"start": v(63.45, 86) * mm, "end": v(57.68, 76) * mm});
            skLineSegment(sketch, "E556", {"start": v(57.68, 76) * mm, "end": v(63.45, 66) * mm});
            skPoint(sketch, "E557", {"position": v(55.95, 87) * mm});
            skPoint(sketch, "E557.positionSnap0", {"position": v(55.95, 86) * mm});
            skPoint(sketch, "E558.positionSnap0", {"position": v(55.95, 66) * mm});
            skPoint(sketch, "E559", {"position": v(49.9, 70.5) * mm});
            skPoint(sketch, "E560", {"position": v(62.01, 70.5) * mm});
            skPoint(sketch, "E561", {"position": v(62.1, 81.67) * mm});
            skPoint(sketch, "E562", {"position": v(49.12, 82.85) * mm});
            skLineSegment(sketch, "E563", {"start": v(58.83, 76) * mm, "end": v(58.49, 76.6) * mm});
            skPoint(sketch, "E564", {"position": v(65.19, 87) * mm});
            skPoint(sketch, "E565", {"position": v(58.83, 76) * mm});
            skLineSegment(sketch, "E566", {"start": v(48.45, 88) * mm, "end": v(63.45, 88) * mm});
            skLineSegment(sketch, "E567", {"start": v(48.45, 108) * mm, "end": v(63.45, 108) * mm});
            skLineSegment(sketch, "E568", {"start": v(48.45, 108) * mm, "end": v(54.23, 98) * mm});
            skLineSegment(sketch, "E569", {"start": v(54.23, 98) * mm, "end": v(48.45, 88) * mm});
            skLineSegment(sketch, "E570", {"start": v(63.45, 108) * mm, "end": v(57.68, 98) * mm});
            skLineSegment(sketch, "E571", {"start": v(57.68, 98) * mm, "end": v(63.45, 88) * mm});
            skPoint(sketch, "E572", {"position": v(55.95, 109) * mm});
            skPoint(sketch, "E572.positionSnap0", {"position": v(55.95, 108) * mm});
            skPoint(sketch, "E573.positionSnap0", {"position": v(55.95, 88) * mm});
            skPoint(sketch, "E574", {"position": v(49.9, 92.5) * mm});
            skPoint(sketch, "E575", {"position": v(62.01, 92.5) * mm});
            skPoint(sketch, "E576", {"position": v(62.1, 103.67) * mm});
            skPoint(sketch, "E577", {"position": v(49.12, 104.85) * mm});
            skLineSegment(sketch, "E578", {"start": v(58.83, 98) * mm, "end": v(58.49, 98.6) * mm});
            skPoint(sketch, "E579", {"position": v(65.19, 109) * mm});
            skPoint(sketch, "E580", {"position": v(58.83, 98) * mm});
            skLineSegment(sketch, "E581", {"start": v(48.45, 110) * mm, "end": v(63.45, 110) * mm});
            skLineSegment(sketch, "E582", {"start": v(48.45, 130) * mm, "end": v(63.45, 130) * mm});
            skLineSegment(sketch, "E583", {"start": v(48.45, 130) * mm, "end": v(54.23, 120) * mm});
            skLineSegment(sketch, "E584", {"start": v(54.23, 120) * mm, "end": v(48.45, 110) * mm});
            skLineSegment(sketch, "E585", {"start": v(63.45, 130) * mm, "end": v(57.68, 120) * mm});
            skLineSegment(sketch, "E586", {"start": v(57.68, 120) * mm, "end": v(63.45, 110) * mm});
            skPoint(sketch, "E587", {"position": v(55.95, 131) * mm});
            skPoint(sketch, "E587.positionSnap0", {"position": v(55.95, 130) * mm});
            skPoint(sketch, "E588.positionSnap0", {"position": v(55.95, 110) * mm});
            skPoint(sketch, "E589", {"position": v(49.9, 114.5) * mm});
            skPoint(sketch, "E590", {"position": v(62.01, 114.5) * mm});
            skPoint(sketch, "E591", {"position": v(62.1, 125.67) * mm});
            skPoint(sketch, "E592", {"position": v(49.12, 126.85) * mm});
            skLineSegment(sketch, "E593", {"start": v(58.83, 120) * mm, "end": v(58.49, 120.6) * mm});
            skPoint(sketch, "E594", {"position": v(65.19, 131) * mm});
            skPoint(sketch, "E595", {"position": v(58.83, 120) * mm});
            skLineSegment(sketch, "E596", {"start": v(48.45, 132) * mm, "end": v(63.45, 132) * mm});
            skLineSegment(sketch, "E597", {"start": v(48.45, 152) * mm, "end": v(63.45, 152) * mm});
            skLineSegment(sketch, "E598", {"start": v(48.45, 152) * mm, "end": v(54.23, 142) * mm});
            skLineSegment(sketch, "E599", {"start": v(54.23, 142) * mm, "end": v(48.45, 132) * mm});
            skLineSegment(sketch, "E600", {"start": v(63.45, 152) * mm, "end": v(57.68, 142) * mm});
            skLineSegment(sketch, "E601", {"start": v(57.68, 142) * mm, "end": v(63.45, 132) * mm});
            skPoint(sketch, "E602", {"position": v(55.95, 153) * mm});
            skPoint(sketch, "E602.positionSnap0", {"position": v(55.95, 152) * mm});
            skPoint(sketch, "E603.positionSnap0", {"position": v(55.95, 132) * mm});
            skPoint(sketch, "E604", {"position": v(49.9, 136.5) * mm});
            skPoint(sketch, "E605", {"position": v(62.01, 136.5) * mm});
            skPoint(sketch, "E606", {"position": v(62.1, 147.67) * mm});
            skPoint(sketch, "E607", {"position": v(49.12, 148.85) * mm});
            skLineSegment(sketch, "E608", {"start": v(58.83, 142) * mm, "end": v(58.49, 142.6) * mm});
            skPoint(sketch, "E609", {"position": v(65.19, 153) * mm});
            skPoint(sketch, "E610", {"position": v(58.83, 142) * mm});
            skLineSegment(sketch, "E611", {"start": v(48.45, 154) * mm, "end": v(63.45, 154) * mm});
            skLineSegment(sketch, "E612", {"start": v(48.45, 174) * mm, "end": v(63.45, 174) * mm});
            skLineSegment(sketch, "E613", {"start": v(48.45, 174) * mm, "end": v(54.23, 164) * mm});
            skLineSegment(sketch, "E614", {"start": v(54.23, 164) * mm, "end": v(48.45, 154) * mm});
            skLineSegment(sketch, "E615", {"start": v(63.45, 174) * mm, "end": v(57.68, 164) * mm});
            skLineSegment(sketch, "E616", {"start": v(57.68, 164) * mm, "end": v(63.45, 154) * mm});
            skPoint(sketch, "E617", {"position": v(55.95, 175) * mm});
            skPoint(sketch, "E617.positionSnap0", {"position": v(55.95, 174) * mm});
            skPoint(sketch, "E618.positionSnap0", {"position": v(55.95, 154) * mm});
            skPoint(sketch, "E619", {"position": v(49.9, 158.5) * mm});
            skPoint(sketch, "E620", {"position": v(62.01, 158.5) * mm});
            skPoint(sketch, "E621", {"position": v(62.1, 169.67) * mm});
            skPoint(sketch, "E622", {"position": v(49.12, 170.85) * mm});
            skLineSegment(sketch, "E623", {"start": v(58.83, 164) * mm, "end": v(58.49, 164.6) * mm});
            skPoint(sketch, "E624", {"position": v(65.19, 175) * mm});
            skPoint(sketch, "E625", {"position": v(58.83, 164) * mm});
            skLineSegment(sketch, "E626", {"start": v(60.57, 11) * mm, "end": v(75.57, 11) * mm});
            skLineSegment(sketch, "E627", {"start": v(60.57, 31) * mm, "end": v(75.57, 31) * mm});
            skLineSegment(sketch, "E628", {"start": v(60.57, 31) * mm, "end": v(66.34, 21) * mm});
            skLineSegment(sketch, "E629", {"start": v(66.34, 21) * mm, "end": v(60.57, 11) * mm});
            skLineSegment(sketch, "E630", {"start": v(75.57, 31) * mm, "end": v(69.8, 21) * mm});
            skLineSegment(sketch, "E631", {"start": v(69.8, 21) * mm, "end": v(75.57, 11) * mm});
            skPoint(sketch, "E632", {"position": v(68.07, 32) * mm});
            skPoint(sketch, "E632.positionSnap0", {"position": v(68.07, 31) * mm});
            skPoint(sketch, "E633", {"position": v(68.07, 10) * mm});
            skPoint(sketch, "E633.positionSnap0", {"position": v(68.07, 11) * mm});
            skPoint(sketch, "E634", {"position": v(62, 15.5) * mm});
            skPoint(sketch, "E635", {"position": v(74.13, 15.5) * mm});
            skPoint(sketch, "E636", {"position": v(74.22, 26.67) * mm});
            skPoint(sketch, "E637", {"position": v(61.23, 27.85) * mm});
            skLineSegment(sketch, "E638", {"start": v(70.95, 21) * mm, "end": v(70.6, 21.6) * mm});
            skPoint(sketch, "E639", {"position": v(77.3, 32) * mm});
            skPoint(sketch, "E640", {"position": v(70.95, 21) * mm});
            skPoint(sketch, "E641", {"position": v(77.3, 10) * mm});
            skLineSegment(sketch, "E642", {"start": v(60.57, 33) * mm, "end": v(75.57, 33) * mm});
            skLineSegment(sketch, "E643", {"start": v(60.57, 53) * mm, "end": v(75.57, 53) * mm});
            skLineSegment(sketch, "E644", {"start": v(60.57, 53) * mm, "end": v(66.34, 43) * mm});
            skLineSegment(sketch, "E645", {"start": v(66.34, 43) * mm, "end": v(60.57, 33) * mm});
            skLineSegment(sketch, "E646", {"start": v(75.57, 53) * mm, "end": v(69.8, 43) * mm});
            skLineSegment(sketch, "E647", {"start": v(69.8, 43) * mm, "end": v(75.57, 33) * mm});
            skPoint(sketch, "E648", {"position": v(68.07, 54) * mm});
            skPoint(sketch, "E648.positionSnap0", {"position": v(68.07, 53) * mm});
            skPoint(sketch, "E649.positionSnap0", {"position": v(68.07, 33) * mm});
            skPoint(sketch, "E650", {"position": v(62, 37.5) * mm});
            skPoint(sketch, "E651", {"position": v(74.13, 37.5) * mm});
            skPoint(sketch, "E652", {"position": v(74.22, 48.67) * mm});
            skPoint(sketch, "E653", {"position": v(61.23, 49.85) * mm});
            skLineSegment(sketch, "E654", {"start": v(70.95, 43) * mm, "end": v(70.6, 43.6) * mm});
            skPoint(sketch, "E655", {"position": v(77.3, 54) * mm});
            skPoint(sketch, "E656", {"position": v(70.95, 43) * mm});
            skLineSegment(sketch, "E657", {"start": v(60.57, 55) * mm, "end": v(75.57, 55) * mm});
            skLineSegment(sketch, "E658", {"start": v(60.57, 75) * mm, "end": v(75.57, 75) * mm});
            skLineSegment(sketch, "E659", {"start": v(60.57, 75) * mm, "end": v(66.34, 65) * mm});
            skLineSegment(sketch, "E660", {"start": v(66.34, 65) * mm, "end": v(60.57, 55) * mm});
            skLineSegment(sketch, "E661", {"start": v(75.57, 75) * mm, "end": v(69.8, 65) * mm});
            skLineSegment(sketch, "E662", {"start": v(69.8, 65) * mm, "end": v(75.57, 55) * mm});
            skPoint(sketch, "E663", {"position": v(68.07, 76) * mm});
            skPoint(sketch, "E663.positionSnap0", {"position": v(68.07, 75) * mm});
            skPoint(sketch, "E664.positionSnap0", {"position": v(68.07, 55) * mm});
            skPoint(sketch, "E665", {"position": v(62, 59.5) * mm});
            skPoint(sketch, "E666", {"position": v(74.13, 59.5) * mm});
            skPoint(sketch, "E667", {"position": v(74.22, 70.67) * mm});
            skPoint(sketch, "E668", {"position": v(61.23, 71.85) * mm});
            skLineSegment(sketch, "E669", {"start": v(70.95, 65) * mm, "end": v(70.6, 65.6) * mm});
            skPoint(sketch, "E670", {"position": v(77.3, 76) * mm});
            skPoint(sketch, "E671", {"position": v(70.95, 65) * mm});
            skLineSegment(sketch, "E672", {"start": v(60.57, 77) * mm, "end": v(75.57, 77) * mm});
            skLineSegment(sketch, "E673", {"start": v(60.57, 97) * mm, "end": v(75.57, 97) * mm});
            skLineSegment(sketch, "E674", {"start": v(60.57, 97) * mm, "end": v(66.34, 87) * mm});
            skLineSegment(sketch, "E675", {"start": v(66.34, 87) * mm, "end": v(60.57, 77) * mm});
            skLineSegment(sketch, "E676", {"start": v(75.57, 97) * mm, "end": v(69.8, 87) * mm});
            skLineSegment(sketch, "E677", {"start": v(69.8, 87) * mm, "end": v(75.57, 77) * mm});
            skPoint(sketch, "E678", {"position": v(68.07, 98) * mm});
            skPoint(sketch, "E678.positionSnap0", {"position": v(68.07, 97) * mm});
            skPoint(sketch, "E679.positionSnap0", {"position": v(68.07, 77) * mm});
            skPoint(sketch, "E680", {"position": v(62, 81.5) * mm});
            skPoint(sketch, "E681", {"position": v(74.13, 81.5) * mm});
            skPoint(sketch, "E682", {"position": v(74.22, 92.67) * mm});
            skPoint(sketch, "E683", {"position": v(61.23, 93.85) * mm});
            skLineSegment(sketch, "E684", {"start": v(70.95, 87) * mm, "end": v(70.6, 87.6) * mm});
            skPoint(sketch, "E685", {"position": v(77.3, 98) * mm});
            skPoint(sketch, "E686", {"position": v(70.95, 87) * mm});
            skLineSegment(sketch, "E687", {"start": v(60.57, 99) * mm, "end": v(75.57, 99) * mm});
            skLineSegment(sketch, "E688", {"start": v(60.57, 119) * mm, "end": v(75.57, 119) * mm});
            skLineSegment(sketch, "E689", {"start": v(60.57, 119) * mm, "end": v(66.34, 109) * mm});
            skLineSegment(sketch, "E690", {"start": v(66.34, 109) * mm, "end": v(60.57, 99) * mm});
            skLineSegment(sketch, "E691", {"start": v(75.57, 119) * mm, "end": v(69.8, 109) * mm});
            skLineSegment(sketch, "E692", {"start": v(69.8, 109) * mm, "end": v(75.57, 99) * mm});
            skPoint(sketch, "E693", {"position": v(68.07, 120) * mm});
            skPoint(sketch, "E693.positionSnap0", {"position": v(68.07, 119) * mm});
            skPoint(sketch, "E694.positionSnap0", {"position": v(68.07, 99) * mm});
            skPoint(sketch, "E695", {"position": v(62, 103.5) * mm});
            skPoint(sketch, "E696", {"position": v(74.13, 103.5) * mm});
            skPoint(sketch, "E697", {"position": v(74.22, 114.67) * mm});
            skPoint(sketch, "E698", {"position": v(61.23, 115.85) * mm});
            skLineSegment(sketch, "E699", {"start": v(70.95, 109) * mm, "end": v(70.6, 109.6) * mm});
            skPoint(sketch, "E700", {"position": v(77.3, 120) * mm});
            skPoint(sketch, "E701", {"position": v(70.95, 109) * mm});
            skLineSegment(sketch, "E702", {"start": v(60.57, 121) * mm, "end": v(75.57, 121) * mm});
            skLineSegment(sketch, "E703", {"start": v(60.57, 141) * mm, "end": v(75.57, 141) * mm});
            skLineSegment(sketch, "E704", {"start": v(60.57, 141) * mm, "end": v(66.34, 131) * mm});
            skLineSegment(sketch, "E705", {"start": v(66.34, 131) * mm, "end": v(60.57, 121) * mm});
            skLineSegment(sketch, "E706", {"start": v(75.57, 141) * mm, "end": v(69.8, 131) * mm});
            skLineSegment(sketch, "E707", {"start": v(69.8, 131) * mm, "end": v(75.57, 121) * mm});
            skPoint(sketch, "E708", {"position": v(68.07, 142) * mm});
            skPoint(sketch, "E708.positionSnap0", {"position": v(68.07, 141) * mm});
            skPoint(sketch, "E709.positionSnap0", {"position": v(68.07, 121) * mm});
            skPoint(sketch, "E710", {"position": v(62, 125.5) * mm});
            skPoint(sketch, "E711", {"position": v(74.13, 125.5) * mm});
            skPoint(sketch, "E712", {"position": v(74.22, 136.67) * mm});
            skPoint(sketch, "E713", {"position": v(61.23, 137.85) * mm});
            skLineSegment(sketch, "E714", {"start": v(70.95, 131) * mm, "end": v(70.6, 131.6) * mm});
            skPoint(sketch, "E715", {"position": v(77.3, 142) * mm});
            skPoint(sketch, "E716", {"position": v(70.95, 131) * mm});
            skLineSegment(sketch, "E717", {"start": v(60.57, 143) * mm, "end": v(75.57, 143) * mm});
            skLineSegment(sketch, "E718", {"start": v(60.57, 163) * mm, "end": v(75.57, 163) * mm});
            skLineSegment(sketch, "E719", {"start": v(60.57, 163) * mm, "end": v(66.34, 153) * mm});
            skLineSegment(sketch, "E720", {"start": v(66.34, 153) * mm, "end": v(60.57, 143) * mm});
            skLineSegment(sketch, "E721", {"start": v(75.57, 163) * mm, "end": v(69.8, 153) * mm});
            skLineSegment(sketch, "E722", {"start": v(69.8, 153) * mm, "end": v(75.57, 143) * mm});
            skPoint(sketch, "E723", {"position": v(68.07, 164) * mm});
            skPoint(sketch, "E723.positionSnap0", {"position": v(68.07, 163) * mm});
            skPoint(sketch, "E724.positionSnap0", {"position": v(68.07, 143) * mm});
            skPoint(sketch, "E725", {"position": v(62, 147.5) * mm});
            skPoint(sketch, "E726", {"position": v(74.13, 147.5) * mm});
            skPoint(sketch, "E727", {"position": v(74.22, 158.67) * mm});
            skPoint(sketch, "E728", {"position": v(61.23, 159.85) * mm});
            skLineSegment(sketch, "E729", {"start": v(70.95, 153) * mm, "end": v(70.6, 153.6) * mm});
            skPoint(sketch, "E730", {"position": v(77.3, 164) * mm});
            skPoint(sketch, "E731", {"position": v(70.95, 153) * mm});
            skLineSegment(sketch, "E732", {"start": v(60.57, 165) * mm, "end": v(75.57, 165) * mm});
            skLineSegment(sketch, "E733", {"start": v(60.57, 185) * mm, "end": v(75.57, 185) * mm});
            skLineSegment(sketch, "E734", {"start": v(60.57, 185) * mm, "end": v(66.34, 175) * mm});
            skLineSegment(sketch, "E735", {"start": v(66.34, 175) * mm, "end": v(60.57, 165) * mm});
            skLineSegment(sketch, "E736", {"start": v(75.57, 185) * mm, "end": v(69.8, 175) * mm});
            skLineSegment(sketch, "E737", {"start": v(69.8, 175) * mm, "end": v(75.57, 165) * mm});
            skPoint(sketch, "E738", {"position": v(68.07, 186) * mm});
            skPoint(sketch, "E738.positionSnap0", {"position": v(68.07, 185) * mm});
            skPoint(sketch, "E739.positionSnap0", {"position": v(68.07, 165) * mm});
            skPoint(sketch, "E740", {"position": v(62, 169.5) * mm});
            skPoint(sketch, "E741", {"position": v(74.13, 169.5) * mm});
            skPoint(sketch, "E742", {"position": v(74.22, 180.67) * mm});
            skPoint(sketch, "E743", {"position": v(61.23, 181.85) * mm});
            skLineSegment(sketch, "E744", {"start": v(70.95, 175) * mm, "end": v(70.6, 175.6) * mm});
            skPoint(sketch, "E745", {"position": v(58.83, 186) * mm});
            skPoint(sketch, "E746", {"position": v(77.3, 186) * mm});
            skPoint(sketch, "E747", {"position": v(70.95, 175) * mm});
            skLineSegment(sketch, "E748", {"start": v(72.68, 0) * mm, "end": v(87.68, 0) * mm});
            skLineSegment(sketch, "E749", {"start": v(72.68, 20) * mm, "end": v(87.68, 20) * mm});
            skLineSegment(sketch, "E750", {"start": v(72.68, 20) * mm, "end": v(78.45, 10) * mm});
            skLineSegment(sketch, "E751", {"start": v(78.45, 10) * mm, "end": v(72.68, 0) * mm});
            skLineSegment(sketch, "E752", {"start": v(87.68, 20) * mm, "end": v(81.9, 10) * mm});
            skLineSegment(sketch, "E753", {"start": v(81.9, 10) * mm, "end": v(87.68, 0) * mm});
            skPoint(sketch, "E754", {"position": v(80.18, 21) * mm});
            skPoint(sketch, "E754.positionSnap0", {"position": v(80.18, 20) * mm});
            skPoint(sketch, "E755", {"position": v(80.18, -1) * mm});
            skPoint(sketch, "E755.positionSnap0", {"position": v(80.18, 0) * mm});
            skPoint(sketch, "E756", {"position": v(74.12, 4.5) * mm});
            skPoint(sketch, "E757", {"position": v(86.24, 4.5) * mm});
            skPoint(sketch, "E758", {"position": v(86.34, 15.67) * mm});
            skPoint(sketch, "E759", {"position": v(73.34, 16.85) * mm});
            skLineSegment(sketch, "E760", {"start": v(83.06, 10) * mm, "end": v(82.71, 10.6) * mm});
            skPoint(sketch, "E761", {"position": v(89.41, 21) * mm});
            skPoint(sketch, "E762", {"position": v(83.06, 10) * mm});
            skPoint(sketch, "E763", {"position": v(70.95, -1) * mm});
            skPoint(sketch, "E764", {"position": v(89.41, -1) * mm});
            skLineSegment(sketch, "E765", {"start": v(72.68, 22) * mm, "end": v(87.68, 22) * mm});
            skLineSegment(sketch, "E766", {"start": v(72.68, 42) * mm, "end": v(87.68, 42) * mm});
            skLineSegment(sketch, "E767", {"start": v(72.68, 42) * mm, "end": v(78.45, 32) * mm});
            skLineSegment(sketch, "E768", {"start": v(78.45, 32) * mm, "end": v(72.68, 22) * mm});
            skLineSegment(sketch, "E769", {"start": v(87.68, 42) * mm, "end": v(81.9, 32) * mm});
            skLineSegment(sketch, "E770", {"start": v(81.9, 32) * mm, "end": v(87.68, 22) * mm});
            skPoint(sketch, "E771", {"position": v(80.18, 43) * mm});
            skPoint(sketch, "E771.positionSnap0", {"position": v(80.18, 42) * mm});
            skPoint(sketch, "E772.positionSnap0", {"position": v(80.18, 22) * mm});
            skPoint(sketch, "E773", {"position": v(74.12, 26.5) * mm});
            skPoint(sketch, "E774", {"position": v(86.24, 26.5) * mm});
            skPoint(sketch, "E775", {"position": v(86.34, 37.67) * mm});
            skPoint(sketch, "E776", {"position": v(73.34, 38.85) * mm});
            skLineSegment(sketch, "E777", {"start": v(83.06, 32) * mm, "end": v(82.71, 32.6) * mm});
            skPoint(sketch, "E778", {"position": v(89.41, 43) * mm});
            skPoint(sketch, "E779", {"position": v(83.06, 32) * mm});
            skLineSegment(sketch, "E780", {"start": v(72.68, 44) * mm, "end": v(87.68, 44) * mm});
            skLineSegment(sketch, "E781", {"start": v(72.68, 64) * mm, "end": v(87.68, 64) * mm});
            skLineSegment(sketch, "E782", {"start": v(72.68, 64) * mm, "end": v(78.45, 54) * mm});
            skLineSegment(sketch, "E783", {"start": v(78.45, 54) * mm, "end": v(72.68, 44) * mm});
            skLineSegment(sketch, "E784", {"start": v(87.68, 64) * mm, "end": v(81.9, 54) * mm});
            skLineSegment(sketch, "E785", {"start": v(81.9, 54) * mm, "end": v(87.68, 44) * mm});
            skPoint(sketch, "E786", {"position": v(80.18, 65) * mm});
            skPoint(sketch, "E786.positionSnap0", {"position": v(80.18, 64) * mm});
            skPoint(sketch, "E787.positionSnap0", {"position": v(80.18, 44) * mm});
            skPoint(sketch, "E788", {"position": v(74.12, 48.5) * mm});
            skPoint(sketch, "E789", {"position": v(86.24, 48.5) * mm});
            skPoint(sketch, "E790", {"position": v(86.34, 59.67) * mm});
            skPoint(sketch, "E791", {"position": v(73.34, 60.85) * mm});
            skLineSegment(sketch, "E792", {"start": v(83.06, 54) * mm, "end": v(82.71, 54.6) * mm});
            skPoint(sketch, "E793", {"position": v(89.41, 65) * mm});
            skPoint(sketch, "E794", {"position": v(83.06, 54) * mm});
            skLineSegment(sketch, "E795", {"start": v(72.68, 66) * mm, "end": v(87.68, 66) * mm});
            skLineSegment(sketch, "E796", {"start": v(72.68, 86) * mm, "end": v(87.68, 86) * mm});
            skLineSegment(sketch, "E797", {"start": v(72.68, 86) * mm, "end": v(78.45, 76) * mm});
            skLineSegment(sketch, "E798", {"start": v(78.45, 76) * mm, "end": v(72.68, 66) * mm});
            skLineSegment(sketch, "E799", {"start": v(87.68, 86) * mm, "end": v(81.9, 76) * mm});
            skLineSegment(sketch, "E800", {"start": v(81.9, 76) * mm, "end": v(87.68, 66) * mm});
            skPoint(sketch, "E801", {"position": v(80.18, 87) * mm});
            skPoint(sketch, "E801.positionSnap0", {"position": v(80.18, 86) * mm});
            skPoint(sketch, "E802.positionSnap0", {"position": v(80.18, 66) * mm});
            skPoint(sketch, "E803", {"position": v(74.12, 70.5) * mm});
            skPoint(sketch, "E804", {"position": v(86.24, 70.5) * mm});
            skPoint(sketch, "E805", {"position": v(86.34, 81.67) * mm});
            skPoint(sketch, "E806", {"position": v(73.34, 82.85) * mm});
            skLineSegment(sketch, "E807", {"start": v(83.06, 76) * mm, "end": v(82.71, 76.6) * mm});
            skPoint(sketch, "E808", {"position": v(89.41, 87) * mm});
            skPoint(sketch, "E809", {"position": v(83.06, 76) * mm});
            skLineSegment(sketch, "E810", {"start": v(72.68, 88) * mm, "end": v(87.68, 88) * mm});
            skLineSegment(sketch, "E811", {"start": v(72.68, 108) * mm, "end": v(87.68, 108) * mm});
            skLineSegment(sketch, "E812", {"start": v(72.68, 108) * mm, "end": v(78.45, 98) * mm});
            skLineSegment(sketch, "E813", {"start": v(78.45, 98) * mm, "end": v(72.68, 88) * mm});
            skLineSegment(sketch, "E814", {"start": v(87.68, 108) * mm, "end": v(81.9, 98) * mm});
            skLineSegment(sketch, "E815", {"start": v(81.9, 98) * mm, "end": v(87.68, 88) * mm});
            skPoint(sketch, "E816", {"position": v(80.18, 109) * mm});
            skPoint(sketch, "E816.positionSnap0", {"position": v(80.18, 108) * mm});
            skPoint(sketch, "E817.positionSnap0", {"position": v(80.18, 88) * mm});
            skPoint(sketch, "E818", {"position": v(74.12, 92.5) * mm});
            skPoint(sketch, "E819", {"position": v(86.24, 92.5) * mm});
            skPoint(sketch, "E820", {"position": v(86.34, 103.67) * mm});
            skPoint(sketch, "E821", {"position": v(73.34, 104.85) * mm});
            skLineSegment(sketch, "E822", {"start": v(83.06, 98) * mm, "end": v(82.71, 98.6) * mm});
            skPoint(sketch, "E823", {"position": v(89.41, 109) * mm});
            skPoint(sketch, "E824", {"position": v(83.06, 98) * mm});
            skLineSegment(sketch, "E825", {"start": v(72.68, 110) * mm, "end": v(87.68, 110) * mm});
            skLineSegment(sketch, "E826", {"start": v(72.68, 130) * mm, "end": v(87.68, 130) * mm});
            skLineSegment(sketch, "E827", {"start": v(72.68, 130) * mm, "end": v(78.45, 120) * mm});
            skLineSegment(sketch, "E828", {"start": v(78.45, 120) * mm, "end": v(72.68, 110) * mm});
            skLineSegment(sketch, "E829", {"start": v(87.68, 130) * mm, "end": v(81.9, 120) * mm});
            skLineSegment(sketch, "E830", {"start": v(81.9, 120) * mm, "end": v(87.68, 110) * mm});
            skPoint(sketch, "E831", {"position": v(80.18, 131) * mm});
            skPoint(sketch, "E831.positionSnap0", {"position": v(80.18, 130) * mm});
            skPoint(sketch, "E832.positionSnap0", {"position": v(80.18, 110) * mm});
            skPoint(sketch, "E833", {"position": v(74.12, 114.5) * mm});
            skPoint(sketch, "E834", {"position": v(86.24, 114.5) * mm});
            skPoint(sketch, "E835", {"position": v(86.34, 125.67) * mm});
            skPoint(sketch, "E836", {"position": v(73.34, 126.85) * mm});
            skLineSegment(sketch, "E837", {"start": v(83.06, 120) * mm, "end": v(82.71, 120.6) * mm});
            skPoint(sketch, "E838", {"position": v(89.41, 131) * mm});
            skPoint(sketch, "E839", {"position": v(83.06, 120) * mm});
            skLineSegment(sketch, "E840", {"start": v(72.68, 132) * mm, "end": v(87.68, 132) * mm});
            skLineSegment(sketch, "E841", {"start": v(72.68, 152) * mm, "end": v(87.68, 152) * mm});
            skLineSegment(sketch, "E842", {"start": v(72.68, 152) * mm, "end": v(78.45, 142) * mm});
            skLineSegment(sketch, "E843", {"start": v(78.45, 142) * mm, "end": v(72.68, 132) * mm});
            skLineSegment(sketch, "E844", {"start": v(87.68, 152) * mm, "end": v(81.9, 142) * mm});
            skLineSegment(sketch, "E845", {"start": v(81.9, 142) * mm, "end": v(87.68, 132) * mm});
            skPoint(sketch, "E846", {"position": v(80.18, 153) * mm});
            skPoint(sketch, "E846.positionSnap0", {"position": v(80.18, 152) * mm});
            skPoint(sketch, "E847.positionSnap0", {"position": v(80.18, 132) * mm});
            skPoint(sketch, "E848", {"position": v(74.12, 136.5) * mm});
            skPoint(sketch, "E849", {"position": v(86.24, 136.5) * mm});
            skPoint(sketch, "E850", {"position": v(86.34, 147.67) * mm});
            skPoint(sketch, "E851", {"position": v(73.34, 148.85) * mm});
            skLineSegment(sketch, "E852", {"start": v(83.06, 142) * mm, "end": v(82.71, 142.6) * mm});
            skPoint(sketch, "E853", {"position": v(89.41, 153) * mm});
            skPoint(sketch, "E854", {"position": v(83.06, 142) * mm});
            skLineSegment(sketch, "E855", {"start": v(72.68, 154) * mm, "end": v(87.68, 154) * mm});
            skLineSegment(sketch, "E856", {"start": v(72.68, 174) * mm, "end": v(87.68, 174) * mm});
            skLineSegment(sketch, "E857", {"start": v(72.68, 174) * mm, "end": v(78.45, 164) * mm});
            skLineSegment(sketch, "E858", {"start": v(78.45, 164) * mm, "end": v(72.68, 154) * mm});
            skLineSegment(sketch, "E859", {"start": v(87.68, 174) * mm, "end": v(81.9, 164) * mm});
            skLineSegment(sketch, "E860", {"start": v(81.9, 164) * mm, "end": v(87.68, 154) * mm});
            skPoint(sketch, "E861", {"position": v(80.18, 175) * mm});
            skPoint(sketch, "E861.positionSnap0", {"position": v(80.18, 174) * mm});
            skPoint(sketch, "E862.positionSnap0", {"position": v(80.18, 154) * mm});
            skPoint(sketch, "E863", {"position": v(74.12, 158.5) * mm});
            skPoint(sketch, "E864", {"position": v(86.24, 158.5) * mm});
            skPoint(sketch, "E865", {"position": v(86.34, 169.67) * mm});
            skPoint(sketch, "E866", {"position": v(73.34, 170.85) * mm});
            skLineSegment(sketch, "E867", {"start": v(83.06, 164) * mm, "end": v(82.71, 164.6) * mm});
            skPoint(sketch, "E868", {"position": v(89.41, 175) * mm});
            skPoint(sketch, "E869", {"position": v(83.06, 164) * mm});
            skLineSegment(sketch, "E870", {"start": v(84.8, 11) * mm, "end": v(99.8, 11) * mm});
            skLineSegment(sketch, "E871", {"start": v(84.8, 31) * mm, "end": v(99.8, 31) * mm});
            skLineSegment(sketch, "E872", {"start": v(84.8, 31) * mm, "end": v(90.57, 21) * mm});
            skLineSegment(sketch, "E873", {"start": v(90.57, 21) * mm, "end": v(84.8, 11) * mm});
            skLineSegment(sketch, "E874", {"start": v(99.8, 31) * mm, "end": v(94.02, 21) * mm});
            skLineSegment(sketch, "E875", {"start": v(94.02, 21) * mm, "end": v(99.8, 11) * mm});
            skPoint(sketch, "E876", {"position": v(92.3, 32) * mm});
            skPoint(sketch, "E876.positionSnap0", {"position": v(92.3, 31) * mm});
            skPoint(sketch, "E877", {"position": v(92.3, 10) * mm});
            skPoint(sketch, "E877.positionSnap0", {"position": v(92.3, 11) * mm});
            skPoint(sketch, "E878", {"position": v(86.23, 15.5) * mm});
            skPoint(sketch, "E879", {"position": v(98.35, 15.5) * mm});
            skPoint(sketch, "E880", {"position": v(98.45, 26.67) * mm});
            skPoint(sketch, "E881", {"position": v(85.46, 27.85) * mm});
            skLineSegment(sketch, "E882", {"start": v(95.17, 21) * mm, "end": v(94.83, 21.6) * mm});
            skPoint(sketch, "E883", {"position": v(101.52, 32) * mm});
            skPoint(sketch, "E884", {"position": v(95.17, 21) * mm});
            skPoint(sketch, "E885", {"position": v(101.52, 10) * mm});
            skLineSegment(sketch, "E886", {"start": v(84.8, 33) * mm, "end": v(99.8, 33) * mm});
            skLineSegment(sketch, "E887", {"start": v(84.8, 53) * mm, "end": v(99.8, 53) * mm});
            skLineSegment(sketch, "E888", {"start": v(84.8, 53) * mm, "end": v(90.57, 43) * mm});
            skLineSegment(sketch, "E889", {"start": v(90.57, 43) * mm, "end": v(84.8, 33) * mm});
            skLineSegment(sketch, "E890", {"start": v(99.8, 53) * mm, "end": v(94.02, 43) * mm});
            skLineSegment(sketch, "E891", {"start": v(94.02, 43) * mm, "end": v(99.8, 33) * mm});
            skPoint(sketch, "E892", {"position": v(92.3, 54) * mm});
            skPoint(sketch, "E892.positionSnap0", {"position": v(92.3, 53) * mm});
            skPoint(sketch, "E893.positionSnap0", {"position": v(92.3, 33) * mm});
            skPoint(sketch, "E894", {"position": v(86.23, 37.5) * mm});
            skPoint(sketch, "E895", {"position": v(98.35, 37.5) * mm});
            skPoint(sketch, "E896", {"position": v(98.45, 48.67) * mm});
            skPoint(sketch, "E897", {"position": v(85.46, 49.85) * mm});
            skLineSegment(sketch, "E898", {"start": v(95.17, 43) * mm, "end": v(94.83, 43.6) * mm});
            skPoint(sketch, "E899", {"position": v(101.52, 54) * mm});
            skPoint(sketch, "E900", {"position": v(95.17, 43) * mm});
            skLineSegment(sketch, "E901", {"start": v(84.8, 55) * mm, "end": v(99.8, 55) * mm});
            skLineSegment(sketch, "E902", {"start": v(84.8, 75) * mm, "end": v(99.8, 75) * mm});
            skLineSegment(sketch, "E903", {"start": v(84.8, 75) * mm, "end": v(90.57, 65) * mm});
            skLineSegment(sketch, "E904", {"start": v(90.57, 65) * mm, "end": v(84.8, 55) * mm});
            skLineSegment(sketch, "E905", {"start": v(99.8, 75) * mm, "end": v(94.02, 65) * mm});
            skLineSegment(sketch, "E906", {"start": v(94.02, 65) * mm, "end": v(99.8, 55) * mm});
            skPoint(sketch, "E907", {"position": v(92.3, 76) * mm});
            skPoint(sketch, "E907.positionSnap0", {"position": v(92.3, 75) * mm});
            skPoint(sketch, "E908.positionSnap0", {"position": v(92.3, 55) * mm});
            skPoint(sketch, "E909", {"position": v(86.23, 59.5) * mm});
            skPoint(sketch, "E910", {"position": v(98.35, 59.5) * mm});
            skPoint(sketch, "E911", {"position": v(98.45, 70.67) * mm});
            skPoint(sketch, "E912", {"position": v(85.46, 71.85) * mm});
            skLineSegment(sketch, "E913", {"start": v(95.17, 65) * mm, "end": v(94.83, 65.6) * mm});
            skPoint(sketch, "E914", {"position": v(101.52, 76) * mm});
            skPoint(sketch, "E915", {"position": v(95.17, 65) * mm});
            skLineSegment(sketch, "E916", {"start": v(84.8, 77) * mm, "end": v(99.8, 77) * mm});
            skLineSegment(sketch, "E917", {"start": v(84.8, 97) * mm, "end": v(99.8, 97) * mm});
            skLineSegment(sketch, "E918", {"start": v(84.8, 97) * mm, "end": v(90.57, 87) * mm});
            skLineSegment(sketch, "E919", {"start": v(90.57, 87) * mm, "end": v(84.8, 77) * mm});
            skLineSegment(sketch, "E920", {"start": v(99.8, 97) * mm, "end": v(94.02, 87) * mm});
            skLineSegment(sketch, "E921", {"start": v(94.02, 87) * mm, "end": v(99.8, 77) * mm});
            skPoint(sketch, "E922", {"position": v(92.3, 98) * mm});
            skPoint(sketch, "E922.positionSnap0", {"position": v(92.3, 97) * mm});
            skPoint(sketch, "E923.positionSnap0", {"position": v(92.3, 77) * mm});
            skPoint(sketch, "E924", {"position": v(86.23, 81.5) * mm});
            skPoint(sketch, "E925", {"position": v(98.35, 81.5) * mm});
            skPoint(sketch, "E926", {"position": v(98.45, 92.67) * mm});
            skPoint(sketch, "E927", {"position": v(85.46, 93.85) * mm});
            skLineSegment(sketch, "E928", {"start": v(95.17, 87) * mm, "end": v(94.83, 87.6) * mm});
            skPoint(sketch, "E929", {"position": v(101.52, 98) * mm});
            skPoint(sketch, "E930", {"position": v(95.17, 87) * mm});
            skLineSegment(sketch, "E931", {"start": v(84.8, 99) * mm, "end": v(99.8, 99) * mm});
            skLineSegment(sketch, "E932", {"start": v(84.8, 119) * mm, "end": v(99.8, 119) * mm});
            skLineSegment(sketch, "E933", {"start": v(84.8, 119) * mm, "end": v(90.57, 109) * mm});
            skLineSegment(sketch, "E934", {"start": v(90.57, 109) * mm, "end": v(84.8, 99) * mm});
            skLineSegment(sketch, "E935", {"start": v(99.8, 119) * mm, "end": v(94.02, 109) * mm});
            skLineSegment(sketch, "E936", {"start": v(94.02, 109) * mm, "end": v(99.8, 99) * mm});
            skPoint(sketch, "E937", {"position": v(92.3, 120) * mm});
            skPoint(sketch, "E937.positionSnap0", {"position": v(92.3, 119) * mm});
            skPoint(sketch, "E938.positionSnap0", {"position": v(92.3, 99) * mm});
            skPoint(sketch, "E939", {"position": v(86.23, 103.5) * mm});
            skPoint(sketch, "E940", {"position": v(98.35, 103.5) * mm});
            skPoint(sketch, "E941", {"position": v(98.45, 114.67) * mm});
            skPoint(sketch, "E942", {"position": v(85.46, 115.85) * mm});
            skLineSegment(sketch, "E943", {"start": v(95.17, 109) * mm, "end": v(94.83, 109.6) * mm});
            skPoint(sketch, "E944", {"position": v(101.52, 120) * mm});
            skPoint(sketch, "E945", {"position": v(95.17, 109) * mm});
            skLineSegment(sketch, "E946", {"start": v(84.8, 121) * mm, "end": v(99.8, 121) * mm});
            skLineSegment(sketch, "E947", {"start": v(84.8, 141) * mm, "end": v(99.8, 141) * mm});
            skLineSegment(sketch, "E948", {"start": v(84.8, 141) * mm, "end": v(90.57, 131) * mm});
            skLineSegment(sketch, "E949", {"start": v(90.57, 131) * mm, "end": v(84.8, 121) * mm});
            skLineSegment(sketch, "E950", {"start": v(99.8, 141) * mm, "end": v(94.02, 131) * mm});
            skLineSegment(sketch, "E951", {"start": v(94.02, 131) * mm, "end": v(99.8, 121) * mm});
            skPoint(sketch, "E952", {"position": v(92.3, 142) * mm});
            skPoint(sketch, "E952.positionSnap0", {"position": v(92.3, 141) * mm});
            skPoint(sketch, "E953.positionSnap0", {"position": v(92.3, 121) * mm});
            skPoint(sketch, "E954", {"position": v(86.23, 125.5) * mm});
            skPoint(sketch, "E955", {"position": v(98.35, 125.5) * mm});
            skPoint(sketch, "E956", {"position": v(98.45, 136.67) * mm});
            skPoint(sketch, "E957", {"position": v(85.46, 137.85) * mm});
            skLineSegment(sketch, "E958", {"start": v(95.17, 131) * mm, "end": v(94.83, 131.6) * mm});
            skPoint(sketch, "E959", {"position": v(101.52, 142) * mm});
            skPoint(sketch, "E960", {"position": v(95.17, 131) * mm});
            skLineSegment(sketch, "E961", {"start": v(84.8, 143) * mm, "end": v(99.8, 143) * mm});
            skLineSegment(sketch, "E962", {"start": v(84.8, 163) * mm, "end": v(99.8, 163) * mm});
            skLineSegment(sketch, "E963", {"start": v(84.8, 163) * mm, "end": v(90.57, 153) * mm});
            skLineSegment(sketch, "E964", {"start": v(90.57, 153) * mm, "end": v(84.8, 143) * mm});
            skLineSegment(sketch, "E965", {"start": v(99.8, 163) * mm, "end": v(94.02, 153) * mm});
            skLineSegment(sketch, "E966", {"start": v(94.02, 153) * mm, "end": v(99.8, 143) * mm});
            skPoint(sketch, "E967", {"position": v(92.3, 164) * mm});
            skPoint(sketch, "E967.positionSnap0", {"position": v(92.3, 163) * mm});
            skPoint(sketch, "E968.positionSnap0", {"position": v(92.3, 143) * mm});
            skPoint(sketch, "E969", {"position": v(86.23, 147.5) * mm});
            skPoint(sketch, "E970", {"position": v(98.35, 147.5) * mm});
            skPoint(sketch, "E971", {"position": v(98.45, 158.67) * mm});
            skPoint(sketch, "E972", {"position": v(85.46, 159.85) * mm});
            skLineSegment(sketch, "E973", {"start": v(95.17, 153) * mm, "end": v(94.83, 153.6) * mm});
            skPoint(sketch, "E974", {"position": v(101.52, 164) * mm});
            skPoint(sketch, "E975", {"position": v(95.17, 153) * mm});
            skLineSegment(sketch, "E976", {"start": v(84.8, 165) * mm, "end": v(99.8, 165) * mm});
            skLineSegment(sketch, "E977", {"start": v(84.8, 185) * mm, "end": v(99.8, 185) * mm});
            skLineSegment(sketch, "E978", {"start": v(84.8, 185) * mm, "end": v(90.57, 175) * mm});
            skLineSegment(sketch, "E979", {"start": v(90.57, 175) * mm, "end": v(84.8, 165) * mm});
            skLineSegment(sketch, "E980", {"start": v(99.8, 185) * mm, "end": v(94.02, 175) * mm});
            skLineSegment(sketch, "E981", {"start": v(94.02, 175) * mm, "end": v(99.8, 165) * mm});
            skPoint(sketch, "E982", {"position": v(92.3, 186) * mm});
            skPoint(sketch, "E982.positionSnap0", {"position": v(92.3, 185) * mm});
            skPoint(sketch, "E983.positionSnap0", {"position": v(92.3, 165) * mm});
            skPoint(sketch, "E984", {"position": v(86.23, 169.5) * mm});
            skPoint(sketch, "E985", {"position": v(98.35, 169.5) * mm});
            skPoint(sketch, "E986", {"position": v(98.45, 180.67) * mm});
            skPoint(sketch, "E987", {"position": v(85.46, 181.85) * mm});
            skLineSegment(sketch, "E988", {"start": v(95.17, 175) * mm, "end": v(94.83, 175.6) * mm});
            skPoint(sketch, "E989", {"position": v(83.06, 186) * mm});
            skPoint(sketch, "E990", {"position": v(101.52, 186) * mm});
            skPoint(sketch, "E991", {"position": v(95.17, 175) * mm});
            skLineSegment(sketch, "E992", {"start": v(96.9, 0) * mm, "end": v(111.9, 0) * mm});
            skLineSegment(sketch, "E993", {"start": v(96.9, 20) * mm, "end": v(111.9, 20) * mm});
            skLineSegment(sketch, "E994", {"start": v(96.9, 20) * mm, "end": v(102.68, 10) * mm});
            skLineSegment(sketch, "E995", {"start": v(102.68, 10) * mm, "end": v(96.9, 0) * mm});
            skLineSegment(sketch, "E996", {"start": v(111.9, 20) * mm, "end": v(106.13, 10) * mm});
            skLineSegment(sketch, "E997", {"start": v(106.13, 10) * mm, "end": v(111.9, 0) * mm});
            skPoint(sketch, "E998", {"position": v(104.4, 21) * mm});
            skPoint(sketch, "E998.positionSnap0", {"position": v(104.4, 20) * mm});
            skPoint(sketch, "E999", {"position": v(104.4, -1) * mm});
            skPoint(sketch, "E999.positionSnap0", {"position": v(104.4, 0) * mm});
            skPoint(sketch, "E1000", {"position": v(98.35, 4.5) * mm});
            skPoint(sketch, "E1001", {"position": v(110.47, 4.5) * mm});
            skPoint(sketch, "E1002", {"position": v(110.56, 15.67) * mm});
            skPoint(sketch, "E1003", {"position": v(97.57, 16.85) * mm});
            skLineSegment(sketch, "E1004", {"start": v(107.29, 10) * mm, "end": v(106.94, 10.6) * mm});
            skPoint(sketch, "E1005", {"position": v(113.64, 21) * mm});
            skPoint(sketch, "E1006", {"position": v(107.29, 10) * mm});
            skPoint(sketch, "E1007", {"position": v(95.17, -1) * mm});
            skPoint(sketch, "E1008", {"position": v(113.64, -1) * mm});
            skLineSegment(sketch, "E1009", {"start": v(96.9, 22) * mm, "end": v(111.9, 22) * mm});
            skLineSegment(sketch, "E1010", {"start": v(96.9, 42) * mm, "end": v(111.9, 42) * mm});
            skLineSegment(sketch, "E1011", {"start": v(96.9, 42) * mm, "end": v(102.68, 32) * mm});
            skLineSegment(sketch, "E1012", {"start": v(102.68, 32) * mm, "end": v(96.9, 22) * mm});
            skLineSegment(sketch, "E1013", {"start": v(111.9, 42) * mm, "end": v(106.13, 32) * mm});
            skLineSegment(sketch, "E1014", {"start": v(106.13, 32) * mm, "end": v(111.9, 22) * mm});
            skPoint(sketch, "E1015", {"position": v(104.4, 43) * mm});
            skPoint(sketch, "E1015.positionSnap0", {"position": v(104.4, 42) * mm});
            skPoint(sketch, "E1016.positionSnap0", {"position": v(104.4, 22) * mm});
            skPoint(sketch, "E1017", {"position": v(98.35, 26.5) * mm});
            skPoint(sketch, "E1018", {"position": v(110.47, 26.5) * mm});
            skPoint(sketch, "E1019", {"position": v(110.56, 37.67) * mm});
            skPoint(sketch, "E1020", {"position": v(97.57, 38.85) * mm});
            skLineSegment(sketch, "E1021", {"start": v(107.29, 32) * mm, "end": v(106.94, 32.6) * mm});
            skPoint(sketch, "E1022", {"position": v(113.64, 43) * mm});
            skPoint(sketch, "E1023", {"position": v(107.29, 32) * mm});
            skLineSegment(sketch, "E1024", {"start": v(96.9, 44) * mm, "end": v(111.9, 44) * mm});
            skLineSegment(sketch, "E1025", {"start": v(96.9, 64) * mm, "end": v(111.9, 64) * mm});
            skLineSegment(sketch, "E1026", {"start": v(96.9, 64) * mm, "end": v(102.68, 54) * mm});
            skLineSegment(sketch, "E1027", {"start": v(102.68, 54) * mm, "end": v(96.9, 44) * mm});
            skLineSegment(sketch, "E1028", {"start": v(111.9, 64) * mm, "end": v(106.13, 54) * mm});
            skLineSegment(sketch, "E1029", {"start": v(106.13, 54) * mm, "end": v(111.9, 44) * mm});
            skPoint(sketch, "E1030", {"position": v(104.4, 65) * mm});
            skPoint(sketch, "E1030.positionSnap0", {"position": v(104.4, 64) * mm});
            skPoint(sketch, "E1031.positionSnap0", {"position": v(104.4, 44) * mm});
            skPoint(sketch, "E1032", {"position": v(98.35, 48.5) * mm});
            skPoint(sketch, "E1033", {"position": v(110.47, 48.5) * mm});
            skPoint(sketch, "E1034", {"position": v(110.56, 59.67) * mm});
            skPoint(sketch, "E1035", {"position": v(97.57, 60.85) * mm});
            skLineSegment(sketch, "E1036", {"start": v(107.29, 54) * mm, "end": v(106.94, 54.6) * mm});
            skPoint(sketch, "E1037", {"position": v(113.64, 65) * mm});
            skPoint(sketch, "E1038", {"position": v(107.29, 54) * mm});
            skLineSegment(sketch, "E1039", {"start": v(96.9, 66) * mm, "end": v(111.9, 66) * mm});
            skLineSegment(sketch, "E1040", {"start": v(96.9, 86) * mm, "end": v(111.9, 86) * mm});
            skLineSegment(sketch, "E1041", {"start": v(96.9, 86) * mm, "end": v(102.68, 76) * mm});
            skLineSegment(sketch, "E1042", {"start": v(102.68, 76) * mm, "end": v(96.9, 66) * mm});
            skLineSegment(sketch, "E1043", {"start": v(111.9, 86) * mm, "end": v(106.13, 76) * mm});
            skLineSegment(sketch, "E1044", {"start": v(106.13, 76) * mm, "end": v(111.9, 66) * mm});
            skPoint(sketch, "E1045", {"position": v(104.4, 87) * mm});
            skPoint(sketch, "E1045.positionSnap0", {"position": v(104.4, 86) * mm});
            skPoint(sketch, "E1046.positionSnap0", {"position": v(104.4, 66) * mm});
            skPoint(sketch, "E1047", {"position": v(98.35, 70.5) * mm});
            skPoint(sketch, "E1048", {"position": v(110.47, 70.5) * mm});
            skPoint(sketch, "E1049", {"position": v(110.56, 81.67) * mm});
            skPoint(sketch, "E1050", {"position": v(97.57, 82.85) * mm});
            skLineSegment(sketch, "E1051", {"start": v(107.29, 76) * mm, "end": v(106.94, 76.6) * mm});
            skPoint(sketch, "E1052", {"position": v(113.64, 87) * mm});
            skPoint(sketch, "E1053", {"position": v(107.29, 76) * mm});
            skLineSegment(sketch, "E1054", {"start": v(96.9, 88) * mm, "end": v(111.9, 88) * mm});
            skLineSegment(sketch, "E1055", {"start": v(96.9, 108) * mm, "end": v(111.9, 108) * mm});
            skLineSegment(sketch, "E1056", {"start": v(96.9, 108) * mm, "end": v(102.68, 98) * mm});
            skLineSegment(sketch, "E1057", {"start": v(102.68, 98) * mm, "end": v(96.9, 88) * mm});
            skLineSegment(sketch, "E1058", {"start": v(111.9, 108) * mm, "end": v(106.13, 98) * mm});
            skLineSegment(sketch, "E1059", {"start": v(106.13, 98) * mm, "end": v(111.9, 88) * mm});
            skPoint(sketch, "E1060", {"position": v(104.4, 109) * mm});
            skPoint(sketch, "E1060.positionSnap0", {"position": v(104.4, 108) * mm});
            skPoint(sketch, "E1061.positionSnap0", {"position": v(104.4, 88) * mm});
            skPoint(sketch, "E1062", {"position": v(98.35, 92.5) * mm});
            skPoint(sketch, "E1063", {"position": v(110.47, 92.5) * mm});
            skPoint(sketch, "E1064", {"position": v(110.56, 103.67) * mm});
            skPoint(sketch, "E1065", {"position": v(97.57, 104.85) * mm});
            skLineSegment(sketch, "E1066", {"start": v(107.29, 98) * mm, "end": v(106.94, 98.6) * mm});
            skPoint(sketch, "E1067", {"position": v(113.64, 109) * mm});
            skPoint(sketch, "E1068", {"position": v(107.29, 98) * mm});
            skLineSegment(sketch, "E1069", {"start": v(96.9, 110) * mm, "end": v(111.9, 110) * mm});
            skLineSegment(sketch, "E1070", {"start": v(96.9, 130) * mm, "end": v(111.9, 130) * mm});
            skLineSegment(sketch, "E1071", {"start": v(96.9, 130) * mm, "end": v(102.68, 120) * mm});
            skLineSegment(sketch, "E1072", {"start": v(102.68, 120) * mm, "end": v(96.9, 110) * mm});
            skLineSegment(sketch, "E1073", {"start": v(111.9, 130) * mm, "end": v(106.13, 120) * mm});
            skLineSegment(sketch, "E1074", {"start": v(106.13, 120) * mm, "end": v(111.9, 110) * mm});
            skPoint(sketch, "E1075", {"position": v(104.4, 131) * mm});
            skPoint(sketch, "E1075.positionSnap0", {"position": v(104.4, 130) * mm});
            skPoint(sketch, "E1076.positionSnap0", {"position": v(104.4, 110) * mm});
            skPoint(sketch, "E1077", {"position": v(98.35, 114.5) * mm});
            skPoint(sketch, "E1078", {"position": v(110.47, 114.5) * mm});
            skPoint(sketch, "E1079", {"position": v(110.56, 125.67) * mm});
            skPoint(sketch, "E1080", {"position": v(97.57, 126.85) * mm});
            skLineSegment(sketch, "E1081", {"start": v(107.29, 120) * mm, "end": v(106.94, 120.6) * mm});
            skPoint(sketch, "E1082", {"position": v(113.64, 131) * mm});
            skPoint(sketch, "E1083", {"position": v(107.29, 120) * mm});
            skLineSegment(sketch, "E1084", {"start": v(96.9, 132) * mm, "end": v(111.9, 132) * mm});
            skLineSegment(sketch, "E1085", {"start": v(96.9, 152) * mm, "end": v(111.9, 152) * mm});
            skLineSegment(sketch, "E1086", {"start": v(96.9, 152) * mm, "end": v(102.68, 142) * mm});
            skLineSegment(sketch, "E1087", {"start": v(102.68, 142) * mm, "end": v(96.9, 132) * mm});
            skLineSegment(sketch, "E1088", {"start": v(111.9, 152) * mm, "end": v(106.13, 142) * mm});
            skLineSegment(sketch, "E1089", {"start": v(106.13, 142) * mm, "end": v(111.9, 132) * mm});
            skPoint(sketch, "E1090", {"position": v(104.4, 153) * mm});
            skPoint(sketch, "E1090.positionSnap0", {"position": v(104.4, 152) * mm});
            skPoint(sketch, "E1091.positionSnap0", {"position": v(104.4, 132) * mm});
            skPoint(sketch, "E1092", {"position": v(98.35, 136.5) * mm});
            skPoint(sketch, "E1093", {"position": v(110.47, 136.5) * mm});
            skPoint(sketch, "E1094", {"position": v(110.56, 147.67) * mm});
            skPoint(sketch, "E1095", {"position": v(97.57, 148.85) * mm});
            skLineSegment(sketch, "E1096", {"start": v(107.29, 142) * mm, "end": v(106.94, 142.6) * mm});
            skPoint(sketch, "E1097", {"position": v(113.64, 153) * mm});
            skPoint(sketch, "E1098", {"position": v(107.29, 142) * mm});
            skLineSegment(sketch, "E1099", {"start": v(96.9, 154) * mm, "end": v(111.9, 154) * mm});
            skLineSegment(sketch, "E1100", {"start": v(96.9, 174) * mm, "end": v(111.9, 174) * mm});
            skLineSegment(sketch, "E1101", {"start": v(96.9, 174) * mm, "end": v(102.68, 164) * mm});
            skLineSegment(sketch, "E1102", {"start": v(102.68, 164) * mm, "end": v(96.9, 154) * mm});
            skLineSegment(sketch, "E1103", {"start": v(111.9, 174) * mm, "end": v(106.13, 164) * mm});
            skLineSegment(sketch, "E1104", {"start": v(106.13, 164) * mm, "end": v(111.9, 154) * mm});
            skPoint(sketch, "E1105", {"position": v(104.4, 175) * mm});
            skPoint(sketch, "E1105.positionSnap0", {"position": v(104.4, 174) * mm});
            skPoint(sketch, "E1106.positionSnap0", {"position": v(104.4, 154) * mm});
            skPoint(sketch, "E1107", {"position": v(98.35, 158.5) * mm});
            skPoint(sketch, "E1108", {"position": v(110.47, 158.5) * mm});
            skPoint(sketch, "E1109", {"position": v(110.56, 169.67) * mm});
            skPoint(sketch, "E1110", {"position": v(97.57, 170.85) * mm});
            skLineSegment(sketch, "E1111", {"start": v(107.29, 164) * mm, "end": v(106.94, 164.6) * mm});
            skPoint(sketch, "E1112", {"position": v(113.64, 175) * mm});
            skPoint(sketch, "E1113", {"position": v(107.29, 164) * mm});
            skLineSegment(sketch, "E1114", {"start": v(109.02, 11) * mm, "end": v(124.02, 11) * mm});
            skLineSegment(sketch, "E1115", {"start": v(109.02, 31) * mm, "end": v(124.02, 31) * mm});
            skLineSegment(sketch, "E1116", {"start": v(109.02, 31) * mm, "end": v(114.8, 21) * mm});
            skLineSegment(sketch, "E1117", {"start": v(114.8, 21) * mm, "end": v(109.02, 11) * mm});
            skLineSegment(sketch, "E1118", {"start": v(124.02, 31) * mm, "end": v(118.25, 21) * mm});
            skLineSegment(sketch, "E1119", {"start": v(118.25, 21) * mm, "end": v(124.02, 11) * mm});
            skPoint(sketch, "E1120", {"position": v(116.52, 32) * mm});
            skPoint(sketch, "E1120.positionSnap0", {"position": v(116.52, 31) * mm});
            skPoint(sketch, "E1121", {"position": v(116.52, 10) * mm});
            skPoint(sketch, "E1121.positionSnap0", {"position": v(116.52, 11) * mm});
            skPoint(sketch, "E1122", {"position": v(110.46, 15.5) * mm});
            skPoint(sketch, "E1123", {"position": v(122.58, 15.5) * mm});
            skPoint(sketch, "E1124", {"position": v(122.68, 26.67) * mm});
            skPoint(sketch, "E1125", {"position": v(109.68, 27.85) * mm});
            skLineSegment(sketch, "E1126", {"start": v(119.4, 21) * mm, "end": v(119.05, 21.6) * mm});
            skPoint(sketch, "E1127", {"position": v(125.75, 32) * mm});
            skPoint(sketch, "E1128", {"position": v(119.4, 21) * mm});
            skPoint(sketch, "E1129", {"position": v(125.75, 10) * mm});
            skLineSegment(sketch, "E1130", {"start": v(109.02, 33) * mm, "end": v(124.02, 33) * mm});
            skLineSegment(sketch, "E1131", {"start": v(109.02, 53) * mm, "end": v(124.02, 53) * mm});
            skLineSegment(sketch, "E1132", {"start": v(109.02, 53) * mm, "end": v(114.8, 43) * mm});
            skLineSegment(sketch, "E1133", {"start": v(114.8, 43) * mm, "end": v(109.02, 33) * mm});
            skLineSegment(sketch, "E1134", {"start": v(124.02, 53) * mm, "end": v(118.25, 43) * mm});
            skLineSegment(sketch, "E1135", {"start": v(118.25, 43) * mm, "end": v(124.02, 33) * mm});
            skPoint(sketch, "E1136", {"position": v(116.52, 54) * mm});
            skPoint(sketch, "E1136.positionSnap0", {"position": v(116.52, 53) * mm});
            skPoint(sketch, "E1137.positionSnap0", {"position": v(116.52, 33) * mm});
            skPoint(sketch, "E1138", {"position": v(110.46, 37.5) * mm});
            skPoint(sketch, "E1139", {"position": v(122.58, 37.5) * mm});
            skPoint(sketch, "E1140", {"position": v(122.68, 48.67) * mm});
            skPoint(sketch, "E1141", {"position": v(109.68, 49.85) * mm});
            skLineSegment(sketch, "E1142", {"start": v(119.4, 43) * mm, "end": v(119.05, 43.6) * mm});
            skPoint(sketch, "E1143", {"position": v(125.75, 54) * mm});
            skPoint(sketch, "E1144", {"position": v(119.4, 43) * mm});
            skLineSegment(sketch, "E1145", {"start": v(109.02, 55) * mm, "end": v(124.02, 55) * mm});
            skLineSegment(sketch, "E1146", {"start": v(109.02, 75) * mm, "end": v(124.02, 75) * mm});
            skLineSegment(sketch, "E1147", {"start": v(109.02, 75) * mm, "end": v(114.8, 65) * mm});
            skLineSegment(sketch, "E1148", {"start": v(114.8, 65) * mm, "end": v(109.02, 55) * mm});
            skLineSegment(sketch, "E1149", {"start": v(124.02, 75) * mm, "end": v(118.25, 65) * mm});
            skLineSegment(sketch, "E1150", {"start": v(118.25, 65) * mm, "end": v(124.02, 55) * mm});
            skPoint(sketch, "E1151", {"position": v(116.52, 76) * mm});
            skPoint(sketch, "E1151.positionSnap0", {"position": v(116.52, 75) * mm});
            skPoint(sketch, "E1152.positionSnap0", {"position": v(116.52, 55) * mm});
            skPoint(sketch, "E1153", {"position": v(110.46, 59.5) * mm});
            skPoint(sketch, "E1154", {"position": v(122.58, 59.5) * mm});
            skPoint(sketch, "E1155", {"position": v(122.68, 70.67) * mm});
            skPoint(sketch, "E1156", {"position": v(109.68, 71.85) * mm});
            skLineSegment(sketch, "E1157", {"start": v(119.4, 65) * mm, "end": v(119.05, 65.6) * mm});
            skPoint(sketch, "E1158", {"position": v(125.75, 76) * mm});
            skPoint(sketch, "E1159", {"position": v(119.4, 65) * mm});
            skLineSegment(sketch, "E1160", {"start": v(109.02, 77) * mm, "end": v(124.02, 77) * mm});
            skLineSegment(sketch, "E1161", {"start": v(109.02, 97) * mm, "end": v(124.02, 97) * mm});
            skLineSegment(sketch, "E1162", {"start": v(109.02, 97) * mm, "end": v(114.8, 87) * mm});
            skLineSegment(sketch, "E1163", {"start": v(114.8, 87) * mm, "end": v(109.02, 77) * mm});
            skLineSegment(sketch, "E1164", {"start": v(124.02, 97) * mm, "end": v(118.25, 87) * mm});
            skLineSegment(sketch, "E1165", {"start": v(118.25, 87) * mm, "end": v(124.02, 77) * mm});
            skPoint(sketch, "E1166", {"position": v(116.52, 98) * mm});
            skPoint(sketch, "E1166.positionSnap0", {"position": v(116.52, 97) * mm});
            skPoint(sketch, "E1167.positionSnap0", {"position": v(116.52, 77) * mm});
            skPoint(sketch, "E1168", {"position": v(110.46, 81.5) * mm});
            skPoint(sketch, "E1169", {"position": v(122.58, 81.5) * mm});
            skPoint(sketch, "E1170", {"position": v(122.68, 92.67) * mm});
            skPoint(sketch, "E1171", {"position": v(109.68, 93.85) * mm});
            skLineSegment(sketch, "E1172", {"start": v(119.4, 87) * mm, "end": v(119.05, 87.6) * mm});
            skPoint(sketch, "E1173", {"position": v(125.75, 98) * mm});
            skPoint(sketch, "E1174", {"position": v(119.4, 87) * mm});
            skLineSegment(sketch, "E1175", {"start": v(109.02, 99) * mm, "end": v(124.02, 99) * mm});
            skLineSegment(sketch, "E1176", {"start": v(109.02, 119) * mm, "end": v(124.02, 119) * mm});
            skLineSegment(sketch, "E1177", {"start": v(109.02, 119) * mm, "end": v(114.8, 109) * mm});
            skLineSegment(sketch, "E1178", {"start": v(114.8, 109) * mm, "end": v(109.02, 99) * mm});
            skLineSegment(sketch, "E1179", {"start": v(124.02, 119) * mm, "end": v(118.25, 109) * mm});
            skLineSegment(sketch, "E1180", {"start": v(118.25, 109) * mm, "end": v(124.02, 99) * mm});
            skPoint(sketch, "E1181", {"position": v(116.52, 120) * mm});
            skPoint(sketch, "E1181.positionSnap0", {"position": v(116.52, 119) * mm});
            skPoint(sketch, "E1182.positionSnap0", {"position": v(116.52, 99) * mm});
            skPoint(sketch, "E1183", {"position": v(110.46, 103.5) * mm});
            skPoint(sketch, "E1184", {"position": v(122.58, 103.5) * mm});
            skPoint(sketch, "E1185", {"position": v(122.68, 114.67) * mm});
            skPoint(sketch, "E1186", {"position": v(109.68, 115.85) * mm});
            skLineSegment(sketch, "E1187", {"start": v(119.4, 109) * mm, "end": v(119.05, 109.6) * mm});
            skPoint(sketch, "E1188", {"position": v(125.75, 120) * mm});
            skPoint(sketch, "E1189", {"position": v(119.4, 109) * mm});
            skLineSegment(sketch, "E1190", {"start": v(109.02, 121) * mm, "end": v(124.02, 121) * mm});
            skLineSegment(sketch, "E1191", {"start": v(109.02, 141) * mm, "end": v(124.02, 141) * mm});
            skLineSegment(sketch, "E1192", {"start": v(109.02, 141) * mm, "end": v(114.8, 131) * mm});
            skLineSegment(sketch, "E1193", {"start": v(114.8, 131) * mm, "end": v(109.02, 121) * mm});
            skLineSegment(sketch, "E1194", {"start": v(124.02, 141) * mm, "end": v(118.25, 131) * mm});
            skLineSegment(sketch, "E1195", {"start": v(118.25, 131) * mm, "end": v(124.02, 121) * mm});
            skPoint(sketch, "E1196", {"position": v(116.52, 142) * mm});
            skPoint(sketch, "E1196.positionSnap0", {"position": v(116.52, 141) * mm});
            skPoint(sketch, "E1197.positionSnap0", {"position": v(116.52, 121) * mm});
            skPoint(sketch, "E1198", {"position": v(110.46, 125.5) * mm});
            skPoint(sketch, "E1199", {"position": v(122.58, 125.5) * mm});
            skPoint(sketch, "E1200", {"position": v(122.68, 136.67) * mm});
            skPoint(sketch, "E1201", {"position": v(109.68, 137.85) * mm});
            skLineSegment(sketch, "E1202", {"start": v(119.4, 131) * mm, "end": v(119.05, 131.6) * mm});
            skPoint(sketch, "E1203", {"position": v(125.75, 142) * mm});
            skPoint(sketch, "E1204", {"position": v(119.4, 131) * mm});
            skLineSegment(sketch, "E1205", {"start": v(109.02, 143) * mm, "end": v(124.02, 143) * mm});
            skLineSegment(sketch, "E1206", {"start": v(109.02, 163) * mm, "end": v(124.02, 163) * mm});
            skLineSegment(sketch, "E1207", {"start": v(109.02, 163) * mm, "end": v(114.8, 153) * mm});
            skLineSegment(sketch, "E1208", {"start": v(114.8, 153) * mm, "end": v(109.02, 143) * mm});
            skLineSegment(sketch, "E1209", {"start": v(124.02, 163) * mm, "end": v(118.25, 153) * mm});
            skLineSegment(sketch, "E1210", {"start": v(118.25, 153) * mm, "end": v(124.02, 143) * mm});
            skPoint(sketch, "E1211", {"position": v(116.52, 164) * mm});
            skPoint(sketch, "E1211.positionSnap0", {"position": v(116.52, 163) * mm});
            skPoint(sketch, "E1212.positionSnap0", {"position": v(116.52, 143) * mm});
            skPoint(sketch, "E1213", {"position": v(110.46, 147.5) * mm});
            skPoint(sketch, "E1214", {"position": v(122.58, 147.5) * mm});
            skPoint(sketch, "E1215", {"position": v(122.68, 158.67) * mm});
            skPoint(sketch, "E1216", {"position": v(109.68, 159.85) * mm});
            skLineSegment(sketch, "E1217", {"start": v(119.4, 153) * mm, "end": v(119.05, 153.6) * mm});
            skPoint(sketch, "E1218", {"position": v(125.75, 164) * mm});
            skPoint(sketch, "E1219", {"position": v(119.4, 153) * mm});
            skLineSegment(sketch, "E1220", {"start": v(109.02, 165) * mm, "end": v(124.02, 165) * mm});
            skLineSegment(sketch, "E1221", {"start": v(109.02, 185) * mm, "end": v(124.02, 185) * mm});
            skLineSegment(sketch, "E1222", {"start": v(109.02, 185) * mm, "end": v(114.8, 175) * mm});
            skLineSegment(sketch, "E1223", {"start": v(114.8, 175) * mm, "end": v(109.02, 165) * mm});
            skLineSegment(sketch, "E1224", {"start": v(124.02, 185) * mm, "end": v(118.25, 175) * mm});
            skLineSegment(sketch, "E1225", {"start": v(118.25, 175) * mm, "end": v(124.02, 165) * mm});
            skPoint(sketch, "E1226", {"position": v(116.52, 186) * mm});
            skPoint(sketch, "E1226.positionSnap0", {"position": v(116.52, 185) * mm});
            skPoint(sketch, "E1227.positionSnap0", {"position": v(116.52, 165) * mm});
            skPoint(sketch, "E1228", {"position": v(110.46, 169.5) * mm});
            skPoint(sketch, "E1229", {"position": v(122.58, 169.5) * mm});
            skPoint(sketch, "E1230", {"position": v(122.68, 180.67) * mm});
            skPoint(sketch, "E1231", {"position": v(109.68, 181.85) * mm});
            skLineSegment(sketch, "E1232", {"start": v(119.4, 175) * mm, "end": v(119.05, 175.6) * mm});
            skPoint(sketch, "E1233", {"position": v(107.29, 186) * mm});
            skPoint(sketch, "E1234", {"position": v(125.75, 186) * mm});
            skPoint(sketch, "E1235", {"position": v(119.4, 175) * mm});
            skLineSegment(sketch, "E1236", {"start": v(121.13, 0) * mm, "end": v(136.13, 0) * mm});
            skLineSegment(sketch, "E1237", {"start": v(121.13, 20) * mm, "end": v(136.13, 20) * mm});
            skLineSegment(sketch, "E1238", {"start": v(121.13, 20) * mm, "end": v(126.9, 10) * mm});
            skLineSegment(sketch, "E1239", {"start": v(126.9, 10) * mm, "end": v(121.13, 0) * mm});
            skLineSegment(sketch, "E1240", {"start": v(136.13, 20) * mm, "end": v(130.36, 10) * mm});
            skLineSegment(sketch, "E1241", {"start": v(130.36, 10) * mm, "end": v(136.13, 0) * mm});
            skPoint(sketch, "E1242", {"position": v(128.63, 21) * mm});
            skPoint(sketch, "E1242.positionSnap0", {"position": v(128.63, 20) * mm});
            skPoint(sketch, "E1243", {"position": v(128.63, -1) * mm});
            skPoint(sketch, "E1243.positionSnap0", {"position": v(128.63, 0) * mm});
            skPoint(sketch, "E1244", {"position": v(122.57, 4.5) * mm});
            skPoint(sketch, "E1245", {"position": v(134.7, 4.5) * mm});
            skPoint(sketch, "E1246", {"position": v(134.79, 15.67) * mm});
            skPoint(sketch, "E1247", {"position": v(121.8, 16.85) * mm});
            skLineSegment(sketch, "E1248", {"start": v(131.51, 10) * mm, "end": v(131.17, 10.6) * mm});
            skPoint(sketch, "E1249", {"position": v(137.86, 21) * mm});
            skPoint(sketch, "E1250", {"position": v(131.51, 10) * mm});
            skPoint(sketch, "E1251", {"position": v(119.4, -1) * mm});
            skPoint(sketch, "E1252", {"position": v(137.86, -1) * mm});
            skLineSegment(sketch, "E1253", {"start": v(121.13, 22) * mm, "end": v(136.13, 22) * mm});
            skLineSegment(sketch, "E1254", {"start": v(121.13, 42) * mm, "end": v(136.13, 42) * mm});
            skLineSegment(sketch, "E1255", {"start": v(121.13, 42) * mm, "end": v(126.9, 32) * mm});
            skLineSegment(sketch, "E1256", {"start": v(126.9, 32) * mm, "end": v(121.13, 22) * mm});
            skLineSegment(sketch, "E1257", {"start": v(136.13, 42) * mm, "end": v(130.36, 32) * mm});
            skLineSegment(sketch, "E1258", {"start": v(130.36, 32) * mm, "end": v(136.13, 22) * mm});
            skPoint(sketch, "E1259", {"position": v(128.63, 43) * mm});
            skPoint(sketch, "E1259.positionSnap0", {"position": v(128.63, 42) * mm});
            skPoint(sketch, "E1260.positionSnap0", {"position": v(128.63, 22) * mm});
            skPoint(sketch, "E1261", {"position": v(122.57, 26.5) * mm});
            skPoint(sketch, "E1262", {"position": v(134.7, 26.5) * mm});
            skPoint(sketch, "E1263", {"position": v(134.79, 37.67) * mm});
            skPoint(sketch, "E1264", {"position": v(121.8, 38.85) * mm});
            skLineSegment(sketch, "E1265", {"start": v(131.51, 32) * mm, "end": v(131.17, 32.6) * mm});
            skPoint(sketch, "E1266", {"position": v(137.86, 43) * mm});
            skPoint(sketch, "E1267", {"position": v(131.51, 32) * mm});
            skLineSegment(sketch, "E1268", {"start": v(121.13, 44) * mm, "end": v(136.13, 44) * mm});
            skLineSegment(sketch, "E1269", {"start": v(121.13, 64) * mm, "end": v(136.13, 64) * mm});
            skLineSegment(sketch, "E1270", {"start": v(121.13, 64) * mm, "end": v(126.9, 54) * mm});
            skLineSegment(sketch, "E1271", {"start": v(126.9, 54) * mm, "end": v(121.13, 44) * mm});
            skLineSegment(sketch, "E1272", {"start": v(136.13, 64) * mm, "end": v(130.36, 54) * mm});
            skLineSegment(sketch, "E1273", {"start": v(130.36, 54) * mm, "end": v(136.13, 44) * mm});
            skPoint(sketch, "E1274", {"position": v(128.63, 65) * mm});
            skPoint(sketch, "E1274.positionSnap0", {"position": v(128.63, 64) * mm});
            skPoint(sketch, "E1275.positionSnap0", {"position": v(128.63, 44) * mm});
            skPoint(sketch, "E1276", {"position": v(122.57, 48.5) * mm});
            skPoint(sketch, "E1277", {"position": v(134.7, 48.5) * mm});
            skPoint(sketch, "E1278", {"position": v(134.79, 59.67) * mm});
            skPoint(sketch, "E1279", {"position": v(121.8, 60.85) * mm});
            skLineSegment(sketch, "E1280", {"start": v(131.51, 54) * mm, "end": v(131.17, 54.6) * mm});
            skPoint(sketch, "E1281", {"position": v(137.86, 65) * mm});
            skPoint(sketch, "E1282", {"position": v(131.51, 54) * mm});
            skLineSegment(sketch, "E1283", {"start": v(121.13, 66) * mm, "end": v(136.13, 66) * mm});
            skLineSegment(sketch, "E1284", {"start": v(121.13, 86) * mm, "end": v(136.13, 86) * mm});
            skLineSegment(sketch, "E1285", {"start": v(121.13, 86) * mm, "end": v(126.9, 76) * mm});
            skLineSegment(sketch, "E1286", {"start": v(126.9, 76) * mm, "end": v(121.13, 66) * mm});
            skLineSegment(sketch, "E1287", {"start": v(136.13, 86) * mm, "end": v(130.36, 76) * mm});
            skLineSegment(sketch, "E1288", {"start": v(130.36, 76) * mm, "end": v(136.13, 66) * mm});
            skPoint(sketch, "E1289", {"position": v(128.63, 87) * mm});
            skPoint(sketch, "E1289.positionSnap0", {"position": v(128.63, 86) * mm});
            skPoint(sketch, "E1290.positionSnap0", {"position": v(128.63, 66) * mm});
            skPoint(sketch, "E1291", {"position": v(122.57, 70.5) * mm});
            skPoint(sketch, "E1292", {"position": v(134.7, 70.5) * mm});
            skPoint(sketch, "E1293", {"position": v(134.79, 81.67) * mm});
            skPoint(sketch, "E1294", {"position": v(121.8, 82.85) * mm});
            skLineSegment(sketch, "E1295", {"start": v(131.51, 76) * mm, "end": v(131.17, 76.6) * mm});
            skPoint(sketch, "E1296", {"position": v(137.86, 87) * mm});
            skPoint(sketch, "E1297", {"position": v(131.51, 76) * mm});
            skLineSegment(sketch, "E1298", {"start": v(121.13, 88) * mm, "end": v(136.13, 88) * mm});
            skLineSegment(sketch, "E1299", {"start": v(121.13, 108) * mm, "end": v(136.13, 108) * mm});
            skLineSegment(sketch, "E1300", {"start": v(121.13, 108) * mm, "end": v(126.9, 98) * mm});
            skLineSegment(sketch, "E1301", {"start": v(126.9, 98) * mm, "end": v(121.13, 88) * mm});
            skLineSegment(sketch, "E1302", {"start": v(136.13, 108) * mm, "end": v(130.36, 98) * mm});
            skLineSegment(sketch, "E1303", {"start": v(130.36, 98) * mm, "end": v(136.13, 88) * mm});
            skPoint(sketch, "E1304", {"position": v(128.63, 109) * mm});
            skPoint(sketch, "E1304.positionSnap0", {"position": v(128.63, 108) * mm});
            skPoint(sketch, "E1305.positionSnap0", {"position": v(128.63, 88) * mm});
            skPoint(sketch, "E1306", {"position": v(122.57, 92.5) * mm});
            skPoint(sketch, "E1307", {"position": v(134.7, 92.5) * mm});
            skPoint(sketch, "E1308", {"position": v(134.79, 103.67) * mm});
            skPoint(sketch, "E1309", {"position": v(121.8, 104.85) * mm});
            skLineSegment(sketch, "E1310", {"start": v(131.51, 98) * mm, "end": v(131.17, 98.6) * mm});
            skPoint(sketch, "E1311", {"position": v(137.86, 109) * mm});
            skPoint(sketch, "E1312", {"position": v(131.51, 98) * mm});
            skLineSegment(sketch, "E1313", {"start": v(121.13, 110) * mm, "end": v(136.13, 110) * mm});
            skLineSegment(sketch, "E1314", {"start": v(121.13, 130) * mm, "end": v(136.13, 130) * mm});
            skLineSegment(sketch, "E1315", {"start": v(121.13, 130) * mm, "end": v(126.9, 120) * mm});
            skLineSegment(sketch, "E1316", {"start": v(126.9, 120) * mm, "end": v(121.13, 110) * mm});
            skLineSegment(sketch, "E1317", {"start": v(136.13, 130) * mm, "end": v(130.36, 120) * mm});
            skLineSegment(sketch, "E1318", {"start": v(130.36, 120) * mm, "end": v(136.13, 110) * mm});
            skPoint(sketch, "E1319", {"position": v(128.63, 131) * mm});
            skPoint(sketch, "E1319.positionSnap0", {"position": v(128.63, 130) * mm});
            skPoint(sketch, "E1320.positionSnap0", {"position": v(128.63, 110) * mm});
            skPoint(sketch, "E1321", {"position": v(122.57, 114.5) * mm});
            skPoint(sketch, "E1322", {"position": v(134.7, 114.5) * mm});
            skPoint(sketch, "E1323", {"position": v(134.79, 125.67) * mm});
            skPoint(sketch, "E1324", {"position": v(121.8, 126.85) * mm});
            skLineSegment(sketch, "E1325", {"start": v(131.51, 120) * mm, "end": v(131.17, 120.6) * mm});
            skPoint(sketch, "E1326", {"position": v(137.86, 131) * mm});
            skPoint(sketch, "E1327", {"position": v(131.51, 120) * mm});
            skLineSegment(sketch, "E1328", {"start": v(121.13, 132) * mm, "end": v(136.13, 132) * mm});
            skLineSegment(sketch, "E1329", {"start": v(121.13, 152) * mm, "end": v(136.13, 152) * mm});
            skLineSegment(sketch, "E1330", {"start": v(121.13, 152) * mm, "end": v(126.9, 142) * mm});
            skLineSegment(sketch, "E1331", {"start": v(126.9, 142) * mm, "end": v(121.13, 132) * mm});
            skLineSegment(sketch, "E1332", {"start": v(136.13, 152) * mm, "end": v(130.36, 142) * mm});
            skLineSegment(sketch, "E1333", {"start": v(130.36, 142) * mm, "end": v(136.13, 132) * mm});
            skPoint(sketch, "E1334", {"position": v(128.63, 153) * mm});
            skPoint(sketch, "E1334.positionSnap0", {"position": v(128.63, 152) * mm});
            skPoint(sketch, "E1335.positionSnap0", {"position": v(128.63, 132) * mm});
            skPoint(sketch, "E1336", {"position": v(122.57, 136.5) * mm});
            skPoint(sketch, "E1337", {"position": v(134.7, 136.5) * mm});
            skPoint(sketch, "E1338", {"position": v(134.79, 147.67) * mm});
            skPoint(sketch, "E1339", {"position": v(121.8, 148.85) * mm});
            skLineSegment(sketch, "E1340", {"start": v(131.51, 142) * mm, "end": v(131.17, 142.6) * mm});
            skPoint(sketch, "E1341", {"position": v(137.86, 153) * mm});
            skPoint(sketch, "E1342", {"position": v(131.51, 142) * mm});
            skLineSegment(sketch, "E1343", {"start": v(121.13, 154) * mm, "end": v(136.13, 154) * mm});
            skLineSegment(sketch, "E1344", {"start": v(121.13, 174) * mm, "end": v(136.13, 174) * mm});
            skLineSegment(sketch, "E1345", {"start": v(121.13, 174) * mm, "end": v(126.9, 164) * mm});
            skLineSegment(sketch, "E1346", {"start": v(126.9, 164) * mm, "end": v(121.13, 154) * mm});
            skLineSegment(sketch, "E1347", {"start": v(136.13, 174) * mm, "end": v(130.36, 164) * mm});
            skLineSegment(sketch, "E1348", {"start": v(130.36, 164) * mm, "end": v(136.13, 154) * mm});
            skPoint(sketch, "E1349", {"position": v(128.63, 175) * mm});
            skPoint(sketch, "E1349.positionSnap0", {"position": v(128.63, 174) * mm});
            skPoint(sketch, "E1350.positionSnap0", {"position": v(128.63, 154) * mm});
            skPoint(sketch, "E1351", {"position": v(122.57, 158.5) * mm});
            skPoint(sketch, "E1352", {"position": v(134.7, 158.5) * mm});
            skPoint(sketch, "E1353", {"position": v(134.79, 169.67) * mm});
            skPoint(sketch, "E1354", {"position": v(121.8, 170.85) * mm});
            skLineSegment(sketch, "E1355", {"start": v(131.51, 164) * mm, "end": v(131.17, 164.6) * mm});
            skPoint(sketch, "E1356", {"position": v(137.86, 175) * mm});
            skPoint(sketch, "E1357", {"position": v(131.51, 164) * mm});
            skLineSegment(sketch, "E1358", {"start": v(133.25, 11) * mm, "end": v(148.25, 11) * mm});
            skLineSegment(sketch, "E1359", {"start": v(133.25, 31) * mm, "end": v(148.25, 31) * mm});
            skLineSegment(sketch, "E1360", {"start": v(133.25, 31) * mm, "end": v(139.02, 21) * mm});
            skLineSegment(sketch, "E1361", {"start": v(139.02, 21) * mm, "end": v(133.25, 11) * mm});
            skLineSegment(sketch, "E1362", {"start": v(148.25, 31) * mm, "end": v(142.47, 21) * mm});
            skLineSegment(sketch, "E1363", {"start": v(142.47, 21) * mm, "end": v(148.25, 11) * mm});
            skPoint(sketch, "E1364", {"position": v(140.75, 32) * mm});
            skPoint(sketch, "E1364.positionSnap0", {"position": v(140.75, 31) * mm});
            skPoint(sketch, "E1365", {"position": v(140.75, 10) * mm});
            skPoint(sketch, "E1365.positionSnap0", {"position": v(140.75, 11) * mm});
            skPoint(sketch, "E1366", {"position": v(134.69, 15.5) * mm});
            skPoint(sketch, "E1367", {"position": v(146.8, 15.5) * mm});
            skPoint(sketch, "E1368", {"position": v(146.9, 26.67) * mm});
            skPoint(sketch, "E1369", {"position": v(133.91, 27.85) * mm});
            skLineSegment(sketch, "E1370", {"start": v(143.63, 21) * mm, "end": v(143.28, 21.6) * mm});
            skPoint(sketch, "E1371", {"position": v(149.98, 32) * mm});
            skPoint(sketch, "E1372", {"position": v(143.63, 21) * mm});
            skPoint(sketch, "E1373", {"position": v(149.98, 10) * mm});
            skLineSegment(sketch, "E1374", {"start": v(133.25, 33) * mm, "end": v(148.25, 33) * mm});
            skLineSegment(sketch, "E1375", {"start": v(133.25, 53) * mm, "end": v(148.25, 53) * mm});
            skLineSegment(sketch, "E1376", {"start": v(133.25, 53) * mm, "end": v(139.02, 43) * mm});
            skLineSegment(sketch, "E1377", {"start": v(139.02, 43) * mm, "end": v(133.25, 33) * mm});
            skLineSegment(sketch, "E1378", {"start": v(148.25, 53) * mm, "end": v(142.47, 43) * mm});
            skLineSegment(sketch, "E1379", {"start": v(142.47, 43) * mm, "end": v(148.25, 33) * mm});
            skPoint(sketch, "E1380", {"position": v(140.75, 54) * mm});
            skPoint(sketch, "E1380.positionSnap0", {"position": v(140.75, 53) * mm});
            skPoint(sketch, "E1381.positionSnap0", {"position": v(140.75, 33) * mm});
            skPoint(sketch, "E1382", {"position": v(134.69, 37.5) * mm});
            skPoint(sketch, "E1383", {"position": v(146.8, 37.5) * mm});
            skPoint(sketch, "E1384", {"position": v(146.9, 48.67) * mm});
            skPoint(sketch, "E1385", {"position": v(133.91, 49.85) * mm});
            skLineSegment(sketch, "E1386", {"start": v(143.63, 43) * mm, "end": v(143.28, 43.6) * mm});
            skPoint(sketch, "E1387", {"position": v(149.98, 54) * mm});
            skPoint(sketch, "E1388", {"position": v(143.63, 43) * mm});
            skLineSegment(sketch, "E1389", {"start": v(133.25, 55) * mm, "end": v(148.25, 55) * mm});
            skLineSegment(sketch, "E1390", {"start": v(133.25, 75) * mm, "end": v(148.25, 75) * mm});
            skLineSegment(sketch, "E1391", {"start": v(133.25, 75) * mm, "end": v(139.02, 65) * mm});
            skLineSegment(sketch, "E1392", {"start": v(139.02, 65) * mm, "end": v(133.25, 55) * mm});
            skLineSegment(sketch, "E1393", {"start": v(148.25, 75) * mm, "end": v(142.47, 65) * mm});
            skLineSegment(sketch, "E1394", {"start": v(142.47, 65) * mm, "end": v(148.25, 55) * mm});
            skPoint(sketch, "E1395", {"position": v(140.75, 76) * mm});
            skPoint(sketch, "E1395.positionSnap0", {"position": v(140.75, 75) * mm});
            skPoint(sketch, "E1396.positionSnap0", {"position": v(140.75, 55) * mm});
            skPoint(sketch, "E1397", {"position": v(134.69, 59.5) * mm});
            skPoint(sketch, "E1398", {"position": v(146.8, 59.5) * mm});
            skPoint(sketch, "E1399", {"position": v(146.9, 70.67) * mm});
            skPoint(sketch, "E1400", {"position": v(133.91, 71.85) * mm});
            skLineSegment(sketch, "E1401", {"start": v(143.63, 65) * mm, "end": v(143.28, 65.6) * mm});
            skPoint(sketch, "E1402", {"position": v(149.98, 76) * mm});
            skPoint(sketch, "E1403", {"position": v(143.63, 65) * mm});
            skLineSegment(sketch, "E1404", {"start": v(133.25, 77) * mm, "end": v(148.25, 77) * mm});
            skLineSegment(sketch, "E1405", {"start": v(133.25, 97) * mm, "end": v(148.25, 97) * mm});
            skLineSegment(sketch, "E1406", {"start": v(133.25, 97) * mm, "end": v(139.02, 87) * mm});
            skLineSegment(sketch, "E1407", {"start": v(139.02, 87) * mm, "end": v(133.25, 77) * mm});
            skLineSegment(sketch, "E1408", {"start": v(148.25, 97) * mm, "end": v(142.47, 87) * mm});
            skLineSegment(sketch, "E1409", {"start": v(142.47, 87) * mm, "end": v(148.25, 77) * mm});
            skPoint(sketch, "E1410", {"position": v(140.75, 98) * mm});
            skPoint(sketch, "E1410.positionSnap0", {"position": v(140.75, 97) * mm});
            skPoint(sketch, "E1411.positionSnap0", {"position": v(140.75, 77) * mm});
            skPoint(sketch, "E1412", {"position": v(134.69, 81.5) * mm});
            skPoint(sketch, "E1413", {"position": v(146.8, 81.5) * mm});
            skPoint(sketch, "E1414", {"position": v(146.9, 92.67) * mm});
            skPoint(sketch, "E1415", {"position": v(133.91, 93.85) * mm});
            skLineSegment(sketch, "E1416", {"start": v(143.63, 87) * mm, "end": v(143.28, 87.6) * mm});
            skPoint(sketch, "E1417", {"position": v(149.98, 98) * mm});
            skPoint(sketch, "E1418", {"position": v(143.63, 87) * mm});
            skLineSegment(sketch, "E1419", {"start": v(133.25, 99) * mm, "end": v(148.25, 99) * mm});
            skLineSegment(sketch, "E1420", {"start": v(133.25, 119) * mm, "end": v(148.25, 119) * mm});
            skLineSegment(sketch, "E1421", {"start": v(133.25, 119) * mm, "end": v(139.02, 109) * mm});
            skLineSegment(sketch, "E1422", {"start": v(139.02, 109) * mm, "end": v(133.25, 99) * mm});
            skLineSegment(sketch, "E1423", {"start": v(148.25, 119) * mm, "end": v(142.47, 109) * mm});
            skLineSegment(sketch, "E1424", {"start": v(142.47, 109) * mm, "end": v(148.25, 99) * mm});
            skPoint(sketch, "E1425", {"position": v(140.75, 120) * mm});
            skPoint(sketch, "E1425.positionSnap0", {"position": v(140.75, 119) * mm});
            skPoint(sketch, "E1426.positionSnap0", {"position": v(140.75, 99) * mm});
            skPoint(sketch, "E1427", {"position": v(134.69, 103.5) * mm});
            skPoint(sketch, "E1428", {"position": v(146.8, 103.5) * mm});
            skPoint(sketch, "E1429", {"position": v(146.9, 114.67) * mm});
            skPoint(sketch, "E1430", {"position": v(133.91, 115.85) * mm});
            skLineSegment(sketch, "E1431", {"start": v(143.63, 109) * mm, "end": v(143.28, 109.6) * mm});
            skPoint(sketch, "E1432", {"position": v(149.98, 120) * mm});
            skPoint(sketch, "E1433", {"position": v(143.63, 109) * mm});
            skLineSegment(sketch, "E1434", {"start": v(133.25, 121) * mm, "end": v(148.25, 121) * mm});
            skLineSegment(sketch, "E1435", {"start": v(133.25, 141) * mm, "end": v(148.25, 141) * mm});
            skLineSegment(sketch, "E1436", {"start": v(133.25, 141) * mm, "end": v(139.02, 131) * mm});
            skLineSegment(sketch, "E1437", {"start": v(139.02, 131) * mm, "end": v(133.25, 121) * mm});
            skLineSegment(sketch, "E1438", {"start": v(148.25, 141) * mm, "end": v(142.47, 131) * mm});
            skLineSegment(sketch, "E1439", {"start": v(142.47, 131) * mm, "end": v(148.25, 121) * mm});
            skPoint(sketch, "E1440", {"position": v(140.75, 142) * mm});
            skPoint(sketch, "E1440.positionSnap0", {"position": v(140.75, 141) * mm});
            skPoint(sketch, "E1441.positionSnap0", {"position": v(140.75, 121) * mm});
            skPoint(sketch, "E1442", {"position": v(134.69, 125.5) * mm});
            skPoint(sketch, "E1443", {"position": v(146.8, 125.5) * mm});
            skPoint(sketch, "E1444", {"position": v(146.9, 136.67) * mm});
            skPoint(sketch, "E1445", {"position": v(133.91, 137.85) * mm});
            skLineSegment(sketch, "E1446", {"start": v(143.63, 131) * mm, "end": v(143.28, 131.6) * mm});
            skPoint(sketch, "E1447", {"position": v(149.98, 142) * mm});
            skPoint(sketch, "E1448", {"position": v(143.63, 131) * mm});
            skLineSegment(sketch, "E1449", {"start": v(133.25, 143) * mm, "end": v(148.25, 143) * mm});
            skLineSegment(sketch, "E1450", {"start": v(133.25, 163) * mm, "end": v(148.25, 163) * mm});
            skLineSegment(sketch, "E1451", {"start": v(133.25, 163) * mm, "end": v(139.02, 153) * mm});
            skLineSegment(sketch, "E1452", {"start": v(139.02, 153) * mm, "end": v(133.25, 143) * mm});
            skLineSegment(sketch, "E1453", {"start": v(148.25, 163) * mm, "end": v(142.47, 153) * mm});
            skLineSegment(sketch, "E1454", {"start": v(142.47, 153) * mm, "end": v(148.25, 143) * mm});
            skPoint(sketch, "E1455", {"position": v(140.75, 164) * mm});
            skPoint(sketch, "E1455.positionSnap0", {"position": v(140.75, 163) * mm});
            skPoint(sketch, "E1456.positionSnap0", {"position": v(140.75, 143) * mm});
            skPoint(sketch, "E1457", {"position": v(134.69, 147.5) * mm});
            skPoint(sketch, "E1458", {"position": v(146.8, 147.5) * mm});
            skPoint(sketch, "E1459", {"position": v(146.9, 158.67) * mm});
            skPoint(sketch, "E1460", {"position": v(133.91, 159.85) * mm});
            skLineSegment(sketch, "E1461", {"start": v(143.63, 153) * mm, "end": v(143.28, 153.6) * mm});
            skPoint(sketch, "E1462", {"position": v(149.98, 164) * mm});
            skPoint(sketch, "E1463", {"position": v(143.63, 153) * mm});
            skPoint(sketch, "E1464", {"position": v(140.75, 186) * mm});
            skPoint(sketch, "E1464.positionSnap0", {"position": v(140.75, 185) * mm});
            skPoint(sketch, "E1465.positionSnap0", {"position": v(140.75, 165) * mm});
            skPoint(sketch, "E1466", {"position": v(134.69, 169.5) * mm});
            skPoint(sketch, "E1467", {"position": v(146.8, 169.5) * mm});
            skPoint(sketch, "E1468", {"position": v(146.9, 180.67) * mm});
            skPoint(sketch, "E1469", {"position": v(133.91, 181.85) * mm});
            skLineSegment(sketch, "E1470", {"start": v(143.63, 175) * mm, "end": v(143.28, 175.6) * mm});
            skPoint(sketch, "E1471", {"position": v(131.51, 186) * mm});
            skPoint(sketch, "E1472", {"position": v(149.98, 186) * mm});
            skPoint(sketch, "E1473", {"position": v(143.63, 175) * mm});
            skLineSegment(sketch, "E1474.bottom", {"start": v(-36.43, 201.1) * mm, "end": v(176.03, 201.1) * mm});
            skLineSegment(sketch, "E1474.top", {"start": v(-36.43, -13.62) * mm, "end": v(176.03, -13.62) * mm});
            skLineSegment(sketch, "E1474.left", {"start": v(-36.43, 201.1) * mm, "end": v(-36.43, -13.62) * mm});
            skLineSegment(sketch, "E1474.right", {"start": v(176.03, 201.1) * mm, "end": v(176.03, -13.62) * mm});
            skSolve(sketch);
        }
        {
            var Q0;
            Q0=qSketchRegion(id+"F0",true);
            extrude(context, id + "F1", {"entities" : qUnion([Q0]), "depth" : 10 * mm, "offsetDistance" : 25 * mm});
        }
        {
            var Q0;
            Q0=makeQuery(id+"F1.opExtrude","CAP_FACE",FACE,{"disambiguationData":[OSD([sQuery(id+"F0.wireOp",EDGE,"E0"),sQuery(id+"F0.wireOp",EDGE,"E1"),sQuery(id+"F0.wireOp",EDGE,"E2"),sQuery(id+"F0.wireOp",EDGE,"E3"),sQuery(id+"F0.wireOp",EDGE,"E4"),sQuery(id+"F0.wireOp",EDGE,"E5"),sQuery(id+"F0.wireOp",EDGE,"E19"),sQuery(id+"F0.wireOp",EDGE,"E20"),sQuery(id+"F0.wireOp",EDGE,"E21"),sQuery(id+"F0.wireOp",EDGE,"E22"),sQuery(id+"F0.wireOp",EDGE,"E23"),sQuery(id+"F0.wireOp",EDGE,"E24"),sQuery(id+"F0.wireOp",EDGE,"E36"),sQuery(id+"F0.wireOp",EDGE,"E37"),sQuery(id+"F0.wireOp",EDGE,"E38"),sQuery(id+"F0.wireOp",EDGE,"E39"),sQuery(id+"F0.wireOp",EDGE,"E40"),sQuery(id+"F0.wireOp",EDGE,"E41"),sQuery(id+"F0.wireOp",EDGE,"E53"),sQuery(id+"F0.wireOp",EDGE,"E54"),sQuery(id+"F0.wireOp",EDGE,"E55"),sQuery(id+"F0.wireOp",EDGE,"E56"),sQuery(id+"F0.wireOp",EDGE,"E57"),sQuery(id+"F0.wireOp",EDGE,"E58"),sQuery(id+"F0.wireOp",EDGE,"E70"),sQuery(id+"F0.wireOp",EDGE,"E71"),sQuery(id+"F0.wireOp",EDGE,"E72"),sQuery(id+"F0.wireOp",EDGE,"E73"),sQuery(id+"F0.wireOp",EDGE,"E74"),sQuery(id+"F0.wireOp",EDGE,"E75"),sQuery(id+"F0.wireOp",EDGE,"E87"),sQuery(id+"F0.wireOp",EDGE,"E88"),sQuery(id+"F0.wireOp",EDGE,"E89"),sQuery(id+"F0.wireOp",EDGE,"E90"),sQuery(id+"F0.wireOp",EDGE,"E91"),sQuery(id+"F0.wireOp",EDGE,"E92"),sQuery(id+"F0.wireOp",EDGE,"E104"),sQuery(id+"F0.wireOp",EDGE,"E105"),sQuery(id+"F0.wireOp",EDGE,"E106"),sQuery(id+"F0.wireOp",EDGE,"E107"),sQuery(id+"F0.wireOp",EDGE,"E108"),sQuery(id+"F0.wireOp",EDGE,"E109"),sQuery(id+"F0.wireOp",EDGE,"E121"),sQuery(id+"F0.wireOp",EDGE,"E122"),sQuery(id+"F0.wireOp",EDGE,"E123"),sQuery(id+"F0.wireOp",EDGE,"E124"),sQuery(id+"F0.wireOp",EDGE,"E125"),sQuery(id+"F0.wireOp",EDGE,"E126"),sQuery(id+"F0.wireOp",EDGE,"E138"),sQuery(id+"F0.wireOp",EDGE,"E139"),sQuery(id+"F0.wireOp",EDGE,"E140"),sQuery(id+"F0.wireOp",EDGE,"E141"),sQuery(id+"F0.wireOp",EDGE,"E142"),sQuery(id+"F0.wireOp",EDGE,"E143"),sQuery(id+"F0.wireOp",EDGE,"E154"),sQuery(id+"F0.wireOp",EDGE,"E155"),sQuery(id+"F0.wireOp",EDGE,"E156"),sQuery(id+"F0.wireOp",EDGE,"E157"),sQuery(id+"F0.wireOp",EDGE,"E158"),sQuery(id+"F0.wireOp",EDGE,"E159"),sQuery(id+"F0.wireOp",EDGE,"E169"),sQuery(id+"F0.wireOp",EDGE,"E170"),sQuery(id+"F0.wireOp",EDGE,"E171"),sQuery(id+"F0.wireOp",EDGE,"E172"),sQuery(id+"F0.wireOp",EDGE,"E173"),sQuery(id+"F0.wireOp",EDGE,"E174"),sQuery(id+"F0.wireOp",EDGE,"E184"),sQuery(id+"F0.wireOp",EDGE,"E185"),sQuery(id+"F0.wireOp",EDGE,"E186"),sQuery(id+"F0.wireOp",EDGE,"E187"),sQuery(id+"F0.wireOp",EDGE,"E188"),sQuery(id+"F0.wireOp",EDGE,"E189"),sQuery(id+"F0.wireOp",EDGE,"E199"),sQuery(id+"F0.wireOp",EDGE,"E200"),sQuery(id+"F0.wireOp",EDGE,"E201"),sQuery(id+"F0.wireOp",EDGE,"E202"),sQuery(id+"F0.wireOp",EDGE,"E203"),sQuery(id+"F0.wireOp",EDGE,"E204"),sQuery(id+"F0.wireOp",EDGE,"E214"),sQuery(id+"F0.wireOp",EDGE,"E215"),sQuery(id+"F0.wireOp",EDGE,"E216"),sQuery(id+"F0.wireOp",EDGE,"E217"),sQuery(id+"F0.wireOp",EDGE,"E218"),sQuery(id+"F0.wireOp",EDGE,"E219"),sQuery(id+"F0.wireOp",EDGE,"E229"),sQuery(id+"F0.wireOp",EDGE,"E230"),sQuery(id+"F0.wireOp",EDGE,"E231"),sQuery(id+"F0.wireOp",EDGE,"E232"),sQuery(id+"F0.wireOp",EDGE,"E233"),sQuery(id+"F0.wireOp",EDGE,"E234"),sQuery(id+"F0.wireOp",EDGE,"E244"),sQuery(id+"F0.wireOp",EDGE,"E245"),sQuery(id+"F0.wireOp",EDGE,"E246"),sQuery(id+"F0.wireOp",EDGE,"E247"),sQuery(id+"F0.wireOp",EDGE,"E248"),sQuery(id+"F0.wireOp",EDGE,"E249"),sQuery(id+"F0.wireOp",EDGE,"E260"),sQuery(id+"F0.wireOp",EDGE,"E261"),sQuery(id+"F0.wireOp",EDGE,"E262"),sQuery(id+"F0.wireOp",EDGE,"E263"),sQuery(id+"F0.wireOp",EDGE,"E264"),sQuery(id+"F0.wireOp",EDGE,"E265"),sQuery(id+"F0.wireOp",EDGE,"E277"),sQuery(id+"F0.wireOp",EDGE,"E278"),sQuery(id+"F0.wireOp",EDGE,"E279"),sQuery(id+"F0.wireOp",EDGE,"E280"),sQuery(id+"F0.wireOp",EDGE,"E281"),sQuery(id+"F0.wireOp",EDGE,"E282"),sQuery(id+"F0.wireOp",EDGE,"E292"),sQuery(id+"F0.wireOp",EDGE,"E293"),sQuery(id+"F0.wireOp",EDGE,"E294"),sQuery(id+"F0.wireOp",EDGE,"E295"),sQuery(id+"F0.wireOp",EDGE,"E296"),sQuery(id+"F0.wireOp",EDGE,"E297"),sQuery(id+"F0.wireOp",EDGE,"E307"),sQuery(id+"F0.wireOp",EDGE,"E308"),sQuery(id+"F0.wireOp",EDGE,"E309"),sQuery(id+"F0.wireOp",EDGE,"E310"),sQuery(id+"F0.wireOp",EDGE,"E311"),sQuery(id+"F0.wireOp",EDGE,"E312"),sQuery(id+"F0.wireOp",EDGE,"E322"),sQuery(id+"F0.wireOp",EDGE,"E323"),sQuery(id+"F0.wireOp",EDGE,"E324"),sQuery(id+"F0.wireOp",EDGE,"E325"),sQuery(id+"F0.wireOp",EDGE,"E326"),sQuery(id+"F0.wireOp",EDGE,"E327"),sQuery(id+"F0.wireOp",EDGE,"E337"),sQuery(id+"F0.wireOp",EDGE,"E338"),sQuery(id+"F0.wireOp",EDGE,"E339"),sQuery(id+"F0.wireOp",EDGE,"E340"),sQuery(id+"F0.wireOp",EDGE,"E341"),sQuery(id+"F0.wireOp",EDGE,"E342"),sQuery(id+"F0.wireOp",EDGE,"E352"),sQuery(id+"F0.wireOp",EDGE,"E353"),sQuery(id+"F0.wireOp",EDGE,"E354"),sQuery(id+"F0.wireOp",EDGE,"E355"),sQuery(id+"F0.wireOp",EDGE,"E356"),sQuery(id+"F0.wireOp",EDGE,"E357"),sQuery(id+"F0.wireOp",EDGE,"E367"),sQuery(id+"F0.wireOp",EDGE,"E368"),sQuery(id+"F0.wireOp",EDGE,"E369"),sQuery(id+"F0.wireOp",EDGE,"E370"),sQuery(id+"F0.wireOp",EDGE,"E371"),sQuery(id+"F0.wireOp",EDGE,"E372"),sQuery(id+"F0.wireOp",EDGE,"E382"),sQuery(id+"F0.wireOp",EDGE,"E383"),sQuery(id+"F0.wireOp",EDGE,"E384"),sQuery(id+"F0.wireOp",EDGE,"E385"),sQuery(id+"F0.wireOp",EDGE,"E386"),sQuery(id+"F0.wireOp",EDGE,"E387"),sQuery(id+"F0.wireOp",EDGE,"E398"),sQuery(id+"F0.wireOp",EDGE,"E399"),sQuery(id+"F0.wireOp",EDGE,"E400"),sQuery(id+"F0.wireOp",EDGE,"E401"),sQuery(id+"F0.wireOp",EDGE,"E402"),sQuery(id+"F0.wireOp",EDGE,"E403"),sQuery(id+"F0.wireOp",EDGE,"E413"),sQuery(id+"F0.wireOp",EDGE,"E414"),sQuery(id+"F0.wireOp",EDGE,"E415"),sQuery(id+"F0.wireOp",EDGE,"E416"),sQuery(id+"F0.wireOp",EDGE,"E417"),sQuery(id+"F0.wireOp",EDGE,"E418"),sQuery(id+"F0.wireOp",EDGE,"E428"),sQuery(id+"F0.wireOp",EDGE,"E429"),sQuery(id+"F0.wireOp",EDGE,"E430"),sQuery(id+"F0.wireOp",EDGE,"E431"),sQuery(id+"F0.wireOp",EDGE,"E432"),sQuery(id+"F0.wireOp",EDGE,"E433"),sQuery(id+"F0.wireOp",EDGE,"E443"),sQuery(id+"F0.wireOp",EDGE,"E444"),sQuery(id+"F0.wireOp",EDGE,"E445"),sQuery(id+"F0.wireOp",EDGE,"E446"),sQuery(id+"F0.wireOp",EDGE,"E447"),sQuery(id+"F0.wireOp",EDGE,"E448"),sQuery(id+"F0.wireOp",EDGE,"E458"),sQuery(id+"F0.wireOp",EDGE,"E459"),sQuery(id+"F0.wireOp",EDGE,"E460"),sQuery(id+"F0.wireOp",EDGE,"E461"),sQuery(id+"F0.wireOp",EDGE,"E462"),sQuery(id+"F0.wireOp",EDGE,"E463"),sQuery(id+"F0.wireOp",EDGE,"E473"),sQuery(id+"F0.wireOp",EDGE,"E474"),sQuery(id+"F0.wireOp",EDGE,"E475"),sQuery(id+"F0.wireOp",EDGE,"E476"),sQuery(id+"F0.wireOp",EDGE,"E477"),sQuery(id+"F0.wireOp",EDGE,"E478"),sQuery(id+"F0.wireOp",EDGE,"E488"),sQuery(id+"F0.wireOp",EDGE,"E489"),sQuery(id+"F0.wireOp",EDGE,"E490"),sQuery(id+"F0.wireOp",EDGE,"E491"),sQuery(id+"F0.wireOp",EDGE,"E492"),sQuery(id+"F0.wireOp",EDGE,"E493"),sQuery(id+"F0.wireOp",EDGE,"E504"),sQuery(id+"F0.wireOp",EDGE,"E505"),sQuery(id+"F0.wireOp",EDGE,"E506"),sQuery(id+"F0.wireOp",EDGE,"E507"),sQuery(id+"F0.wireOp",EDGE,"E508"),sQuery(id+"F0.wireOp",EDGE,"E509"),sQuery(id+"F0.wireOp",EDGE,"E521"),sQuery(id+"F0.wireOp",EDGE,"E522"),sQuery(id+"F0.wireOp",EDGE,"E523"),sQuery(id+"F0.wireOp",EDGE,"E524"),sQuery(id+"F0.wireOp",EDGE,"E525"),sQuery(id+"F0.wireOp",EDGE,"E526"),sQuery(id+"F0.wireOp",EDGE,"E536"),sQuery(id+"F0.wireOp",EDGE,"E537"),sQuery(id+"F0.wireOp",EDGE,"E538"),sQuery(id+"F0.wireOp",EDGE,"E539"),sQuery(id+"F0.wireOp",EDGE,"E540"),sQuery(id+"F0.wireOp",EDGE,"E541"),sQuery(id+"F0.wireOp",EDGE,"E551"),sQuery(id+"F0.wireOp",EDGE,"E552"),sQuery(id+"F0.wireOp",EDGE,"E553"),sQuery(id+"F0.wireOp",EDGE,"E554"),sQuery(id+"F0.wireOp",EDGE,"E555"),sQuery(id+"F0.wireOp",EDGE,"E556"),sQuery(id+"F0.wireOp",EDGE,"E566"),sQuery(id+"F0.wireOp",EDGE,"E567"),sQuery(id+"F0.wireOp",EDGE,"E568"),sQuery(id+"F0.wireOp",EDGE,"E569"),sQuery(id+"F0.wireOp",EDGE,"E570"),sQuery(id+"F0.wireOp",EDGE,"E571"),sQuery(id+"F0.wireOp",EDGE,"E581"),sQuery(id+"F0.wireOp",EDGE,"E582"),sQuery(id+"F0.wireOp",EDGE,"E583"),sQuery(id+"F0.wireOp",EDGE,"E584"),sQuery(id+"F0.wireOp",EDGE,"E585"),sQuery(id+"F0.wireOp",EDGE,"E586"),sQuery(id+"F0.wireOp",EDGE,"E596"),sQuery(id+"F0.wireOp",EDGE,"E597"),sQuery(id+"F0.wireOp",EDGE,"E598"),sQuery(id+"F0.wireOp",EDGE,"E599"),sQuery(id+"F0.wireOp",EDGE,"E600"),sQuery(id+"F0.wireOp",EDGE,"E601"),sQuery(id+"F0.wireOp",EDGE,"E611"),sQuery(id+"F0.wireOp",EDGE,"E612"),sQuery(id+"F0.wireOp",EDGE,"E613"),sQuery(id+"F0.wireOp",EDGE,"E614"),sQuery(id+"F0.wireOp",EDGE,"E615"),sQuery(id+"F0.wireOp",EDGE,"E616"),sQuery(id+"F0.wireOp",EDGE,"E626"),sQuery(id+"F0.wireOp",EDGE,"E627"),sQuery(id+"F0.wireOp",EDGE,"E628"),sQuery(id+"F0.wireOp",EDGE,"E629"),sQuery(id+"F0.wireOp",EDGE,"E630"),sQuery(id+"F0.wireOp",EDGE,"E631"),sQuery(id+"F0.wireOp",EDGE,"E642"),sQuery(id+"F0.wireOp",EDGE,"E643"),sQuery(id+"F0.wireOp",EDGE,"E644"),sQuery(id+"F0.wireOp",EDGE,"E645"),sQuery(id+"F0.wireOp",EDGE,"E646"),sQuery(id+"F0.wireOp",EDGE,"E647"),sQuery(id+"F0.wireOp",EDGE,"E657"),sQuery(id+"F0.wireOp",EDGE,"E658"),sQuery(id+"F0.wireOp",EDGE,"E659"),sQuery(id+"F0.wireOp",EDGE,"E660"),sQuery(id+"F0.wireOp",EDGE,"E661"),sQuery(id+"F0.wireOp",EDGE,"E662"),sQuery(id+"F0.wireOp",EDGE,"E672"),sQuery(id+"F0.wireOp",EDGE,"E673"),sQuery(id+"F0.wireOp",EDGE,"E674"),sQuery(id+"F0.wireOp",EDGE,"E675"),sQuery(id+"F0.wireOp",EDGE,"E676"),sQuery(id+"F0.wireOp",EDGE,"E677"),sQuery(id+"F0.wireOp",EDGE,"E687"),sQuery(id+"F0.wireOp",EDGE,"E688"),sQuery(id+"F0.wireOp",EDGE,"E689"),sQuery(id+"F0.wireOp",EDGE,"E690"),sQuery(id+"F0.wireOp",EDGE,"E691"),sQuery(id+"F0.wireOp",EDGE,"E692"),sQuery(id+"F0.wireOp",EDGE,"E702"),sQuery(id+"F0.wireOp",EDGE,"E703"),sQuery(id+"F0.wireOp",EDGE,"E704"),sQuery(id+"F0.wireOp",EDGE,"E705"),sQuery(id+"F0.wireOp",EDGE,"E706"),sQuery(id+"F0.wireOp",EDGE,"E707"),sQuery(id+"F0.wireOp",EDGE,"E717"),sQuery(id+"F0.wireOp",EDGE,"E718"),sQuery(id+"F0.wireOp",EDGE,"E719"),sQuery(id+"F0.wireOp",EDGE,"E720"),sQuery(id+"F0.wireOp",EDGE,"E721"),sQuery(id+"F0.wireOp",EDGE,"E722"),sQuery(id+"F0.wireOp",EDGE,"E732"),sQuery(id+"F0.wireOp",EDGE,"E733"),sQuery(id+"F0.wireOp",EDGE,"E734"),sQuery(id+"F0.wireOp",EDGE,"E735"),sQuery(id+"F0.wireOp",EDGE,"E736"),sQuery(id+"F0.wireOp",EDGE,"E737"),sQuery(id+"F0.wireOp",EDGE,"E748"),sQuery(id+"F0.wireOp",EDGE,"E749"),sQuery(id+"F0.wireOp",EDGE,"E750"),sQuery(id+"F0.wireOp",EDGE,"E751"),sQuery(id+"F0.wireOp",EDGE,"E752"),sQuery(id+"F0.wireOp",EDGE,"E753"),sQuery(id+"F0.wireOp",EDGE,"E765"),sQuery(id+"F0.wireOp",EDGE,"E766"),sQuery(id+"F0.wireOp",EDGE,"E767"),sQuery(id+"F0.wireOp",EDGE,"E768"),sQuery(id+"F0.wireOp",EDGE,"E769"),sQuery(id+"F0.wireOp",EDGE,"E770"),sQuery(id+"F0.wireOp",EDGE,"E780"),sQuery(id+"F0.wireOp",EDGE,"E781"),sQuery(id+"F0.wireOp",EDGE,"E782"),sQuery(id+"F0.wireOp",EDGE,"E783"),sQuery(id+"F0.wireOp",EDGE,"E784"),sQuery(id+"F0.wireOp",EDGE,"E785"),sQuery(id+"F0.wireOp",EDGE,"E795"),sQuery(id+"F0.wireOp",EDGE,"E796"),sQuery(id+"F0.wireOp",EDGE,"E797"),sQuery(id+"F0.wireOp",EDGE,"E798"),sQuery(id+"F0.wireOp",EDGE,"E799"),sQuery(id+"F0.wireOp",EDGE,"E800"),sQuery(id+"F0.wireOp",EDGE,"E810"),sQuery(id+"F0.wireOp",EDGE,"E811"),sQuery(id+"F0.wireOp",EDGE,"E812"),sQuery(id+"F0.wireOp",EDGE,"E813"),sQuery(id+"F0.wireOp",EDGE,"E814"),sQuery(id+"F0.wireOp",EDGE,"E815"),sQuery(id+"F0.wireOp",EDGE,"E825"),sQuery(id+"F0.wireOp",EDGE,"E826"),sQuery(id+"F0.wireOp",EDGE,"E827"),sQuery(id+"F0.wireOp",EDGE,"E828"),sQuery(id+"F0.wireOp",EDGE,"E829"),sQuery(id+"F0.wireOp",EDGE,"E830"),sQuery(id+"F0.wireOp",EDGE,"E840"),sQuery(id+"F0.wireOp",EDGE,"E841"),sQuery(id+"F0.wireOp",EDGE,"E842"),sQuery(id+"F0.wireOp",EDGE,"E843"),sQuery(id+"F0.wireOp",EDGE,"E844"),sQuery(id+"F0.wireOp",EDGE,"E845"),sQuery(id+"F0.wireOp",EDGE,"E855"),sQuery(id+"F0.wireOp",EDGE,"E856"),sQuery(id+"F0.wireOp",EDGE,"E857"),sQuery(id+"F0.wireOp",EDGE,"E858"),sQuery(id+"F0.wireOp",EDGE,"E859"),sQuery(id+"F0.wireOp",EDGE,"E860"),sQuery(id+"F0.wireOp",EDGE,"E870"),sQuery(id+"F0.wireOp",EDGE,"E871"),sQuery(id+"F0.wireOp",EDGE,"E872"),sQuery(id+"F0.wireOp",EDGE,"E873"),sQuery(id+"F0.wireOp",EDGE,"E874"),sQuery(id+"F0.wireOp",EDGE,"E875"),sQuery(id+"F0.wireOp",EDGE,"E886"),sQuery(id+"F0.wireOp",EDGE,"E887"),sQuery(id+"F0.wireOp",EDGE,"E888"),sQuery(id+"F0.wireOp",EDGE,"E889"),sQuery(id+"F0.wireOp",EDGE,"E890"),sQuery(id+"F0.wireOp",EDGE,"E891"),sQuery(id+"F0.wireOp",EDGE,"E901"),sQuery(id+"F0.wireOp",EDGE,"E902"),sQuery(id+"F0.wireOp",EDGE,"E903"),sQuery(id+"F0.wireOp",EDGE,"E904"),sQuery(id+"F0.wireOp",EDGE,"E905"),sQuery(id+"F0.wireOp",EDGE,"E906"),sQuery(id+"F0.wireOp",EDGE,"E916"),sQuery(id+"F0.wireOp",EDGE,"E917"),sQuery(id+"F0.wireOp",EDGE,"E918"),sQuery(id+"F0.wireOp",EDGE,"E919"),sQuery(id+"F0.wireOp",EDGE,"E920"),sQuery(id+"F0.wireOp",EDGE,"E921"),sQuery(id+"F0.wireOp",EDGE,"E931"),sQuery(id+"F0.wireOp",EDGE,"E932"),sQuery(id+"F0.wireOp",EDGE,"E933"),sQuery(id+"F0.wireOp",EDGE,"E934"),sQuery(id+"F0.wireOp",EDGE,"E935"),sQuery(id+"F0.wireOp",EDGE,"E936"),sQuery(id+"F0.wireOp",EDGE,"E946"),sQuery(id+"F0.wireOp",EDGE,"E947"),sQuery(id+"F0.wireOp",EDGE,"E948"),sQuery(id+"F0.wireOp",EDGE,"E949"),sQuery(id+"F0.wireOp",EDGE,"E950"),sQuery(id+"F0.wireOp",EDGE,"E951"),sQuery(id+"F0.wireOp",EDGE,"E961"),sQuery(id+"F0.wireOp",EDGE,"E962"),sQuery(id+"F0.wireOp",EDGE,"E963"),sQuery(id+"F0.wireOp",EDGE,"E964"),sQuery(id+"F0.wireOp",EDGE,"E965"),sQuery(id+"F0.wireOp",EDGE,"E966"),sQuery(id+"F0.wireOp",EDGE,"E976"),sQuery(id+"F0.wireOp",EDGE,"E977"),sQuery(id+"F0.wireOp",EDGE,"E978"),sQuery(id+"F0.wireOp",EDGE,"E979"),sQuery(id+"F0.wireOp",EDGE,"E980"),sQuery(id+"F0.wireOp",EDGE,"E981"),sQuery(id+"F0.wireOp",EDGE,"E992"),sQuery(id+"F0.wireOp",EDGE,"E993"),sQuery(id+"F0.wireOp",EDGE,"E994"),sQuery(id+"F0.wireOp",EDGE,"E995"),sQuery(id+"F0.wireOp",EDGE,"E996"),sQuery(id+"F0.wireOp",EDGE,"E997"),sQuery(id+"F0.wireOp",EDGE,"E1009"),sQuery(id+"F0.wireOp",EDGE,"E1010"),sQuery(id+"F0.wireOp",EDGE,"E1011"),sQuery(id+"F0.wireOp",EDGE,"E1012"),sQuery(id+"F0.wireOp",EDGE,"E1013"),sQuery(id+"F0.wireOp",EDGE,"E1014"),sQuery(id+"F0.wireOp",EDGE,"E1024"),sQuery(id+"F0.wireOp",EDGE,"E1025"),sQuery(id+"F0.wireOp",EDGE,"E1026"),sQuery(id+"F0.wireOp",EDGE,"E1027"),sQuery(id+"F0.wireOp",EDGE,"E1028"),sQuery(id+"F0.wireOp",EDGE,"E1029"),sQuery(id+"F0.wireOp",EDGE,"E1039"),sQuery(id+"F0.wireOp",EDGE,"E1040"),sQuery(id+"F0.wireOp",EDGE,"E1041"),sQuery(id+"F0.wireOp",EDGE,"E1042"),sQuery(id+"F0.wireOp",EDGE,"E1043"),sQuery(id+"F0.wireOp",EDGE,"E1044"),sQuery(id+"F0.wireOp",EDGE,"E1054"),sQuery(id+"F0.wireOp",EDGE,"E1055"),sQuery(id+"F0.wireOp",EDGE,"E1056"),sQuery(id+"F0.wireOp",EDGE,"E1057"),sQuery(id+"F0.wireOp",EDGE,"E1058"),sQuery(id+"F0.wireOp",EDGE,"E1059"),sQuery(id+"F0.wireOp",EDGE,"E1069"),sQuery(id+"F0.wireOp",EDGE,"E1070"),sQuery(id+"F0.wireOp",EDGE,"E1071"),sQuery(id+"F0.wireOp",EDGE,"E1072"),sQuery(id+"F0.wireOp",EDGE,"E1073"),sQuery(id+"F0.wireOp",EDGE,"E1074"),sQuery(id+"F0.wireOp",EDGE,"E1084"),sQuery(id+"F0.wireOp",EDGE,"E1085"),sQuery(id+"F0.wireOp",EDGE,"E1086"),sQuery(id+"F0.wireOp",EDGE,"E1087"),sQuery(id+"F0.wireOp",EDGE,"E1088"),sQuery(id+"F0.wireOp",EDGE,"E1089"),sQuery(id+"F0.wireOp",EDGE,"E1099"),sQuery(id+"F0.wireOp",EDGE,"E1100"),sQuery(id+"F0.wireOp",EDGE,"E1101"),sQuery(id+"F0.wireOp",EDGE,"E1102"),sQuery(id+"F0.wireOp",EDGE,"E1103"),sQuery(id+"F0.wireOp",EDGE,"E1104"),sQuery(id+"F0.wireOp",EDGE,"E1114"),sQuery(id+"F0.wireOp",EDGE,"E1115"),sQuery(id+"F0.wireOp",EDGE,"E1116"),sQuery(id+"F0.wireOp",EDGE,"E1117"),sQuery(id+"F0.wireOp",EDGE,"E1118"),sQuery(id+"F0.wireOp",EDGE,"E1119"),sQuery(id+"F0.wireOp",EDGE,"E1130"),sQuery(id+"F0.wireOp",EDGE,"E1131"),sQuery(id+"F0.wireOp",EDGE,"E1132"),sQuery(id+"F0.wireOp",EDGE,"E1133"),sQuery(id+"F0.wireOp",EDGE,"E1134"),sQuery(id+"F0.wireOp",EDGE,"E1135"),sQuery(id+"F0.wireOp",EDGE,"E1145"),sQuery(id+"F0.wireOp",EDGE,"E1146"),sQuery(id+"F0.wireOp",EDGE,"E1147"),sQuery(id+"F0.wireOp",EDGE,"E1148"),sQuery(id+"F0.wireOp",EDGE,"E1149"),sQuery(id+"F0.wireOp",EDGE,"E1150"),sQuery(id+"F0.wireOp",EDGE,"E1160"),sQuery(id+"F0.wireOp",EDGE,"E1161"),sQuery(id+"F0.wireOp",EDGE,"E1162"),sQuery(id+"F0.wireOp",EDGE,"E1163"),sQuery(id+"F0.wireOp",EDGE,"E1164"),sQuery(id+"F0.wireOp",EDGE,"E1165"),sQuery(id+"F0.wireOp",EDGE,"E1175"),sQuery(id+"F0.wireOp",EDGE,"E1176"),sQuery(id+"F0.wireOp",EDGE,"E1177"),sQuery(id+"F0.wireOp",EDGE,"E1178"),sQuery(id+"F0.wireOp",EDGE,"E1179"),sQuery(id+"F0.wireOp",EDGE,"E1180"),sQuery(id+"F0.wireOp",EDGE,"E1190"),sQuery(id+"F0.wireOp",EDGE,"E1191"),sQuery(id+"F0.wireOp",EDGE,"E1192"),sQuery(id+"F0.wireOp",EDGE,"E1193"),sQuery(id+"F0.wireOp",EDGE,"E1194"),sQuery(id+"F0.wireOp",EDGE,"E1195"),sQuery(id+"F0.wireOp",EDGE,"E1205"),sQuery(id+"F0.wireOp",EDGE,"E1206"),sQuery(id+"F0.wireOp",EDGE,"E1207"),sQuery(id+"F0.wireOp",EDGE,"E1208"),sQuery(id+"F0.wireOp",EDGE,"E1209"),sQuery(id+"F0.wireOp",EDGE,"E1210"),sQuery(id+"F0.wireOp",EDGE,"E1220"),sQuery(id+"F0.wireOp",EDGE,"E1221"),sQuery(id+"F0.wireOp",EDGE,"E1222"),sQuery(id+"F0.wireOp",EDGE,"E1223"),sQuery(id+"F0.wireOp",EDGE,"E1224"),sQuery(id+"F0.wireOp",EDGE,"E1225"),sQuery(id+"F0.wireOp",EDGE,"E1236"),sQuery(id+"F0.wireOp",EDGE,"E1237"),sQuery(id+"F0.wireOp",EDGE,"E1238"),sQuery(id+"F0.wireOp",EDGE,"E1239"),sQuery(id+"F0.wireOp",EDGE,"E1240"),sQuery(id+"F0.wireOp",EDGE,"E1241"),sQuery(id+"F0.wireOp",EDGE,"E1253"),sQuery(id+"F0.wireOp",EDGE,"E1254"),sQuery(id+"F0.wireOp",EDGE,"E1255"),sQuery(id+"F0.wireOp",EDGE,"E1256"),sQuery(id+"F0.wireOp",EDGE,"E1257"),sQuery(id+"F0.wireOp",EDGE,"E1258"),sQuery(id+"F0.wireOp",EDGE,"E1268"),sQuery(id+"F0.wireOp",EDGE,"E1269"),sQuery(id+"F0.wireOp",EDGE,"E1270"),sQuery(id+"F0.wireOp",EDGE,"E1271"),sQuery(id+"F0.wireOp",EDGE,"E1272"),sQuery(id+"F0.wireOp",EDGE,"E1273"),sQuery(id+"F0.wireOp",EDGE,"E1283"),sQuery(id+"F0.wireOp",EDGE,"E1284"),sQuery(id+"F0.wireOp",EDGE,"E1285"),sQuery(id+"F0.wireOp",EDGE,"E1286"),sQuery(id+"F0.wireOp",EDGE,"E1287"),sQuery(id+"F0.wireOp",EDGE,"E1288"),sQuery(id+"F0.wireOp",EDGE,"E1298"),sQuery(id+"F0.wireOp",EDGE,"E1299"),sQuery(id+"F0.wireOp",EDGE,"E1300"),sQuery(id+"F0.wireOp",EDGE,"E1301"),sQuery(id+"F0.wireOp",EDGE,"E1302"),sQuery(id+"F0.wireOp",EDGE,"E1303"),sQuery(id+"F0.wireOp",EDGE,"E1313"),sQuery(id+"F0.wireOp",EDGE,"E1314"),sQuery(id+"F0.wireOp",EDGE,"E1315"),sQuery(id+"F0.wireOp",EDGE,"E1316"),sQuery(id+"F0.wireOp",EDGE,"E1317"),sQuery(id+"F0.wireOp",EDGE,"E1318"),sQuery(id+"F0.wireOp",EDGE,"E1328"),sQuery(id+"F0.wireOp",EDGE,"E1329"),sQuery(id+"F0.wireOp",EDGE,"E1330"),sQuery(id+"F0.wireOp",EDGE,"E1331"),sQuery(id+"F0.wireOp",EDGE,"E1332"),sQuery(id+"F0.wireOp",EDGE,"E1333"),sQuery(id+"F0.wireOp",EDGE,"E1343"),sQuery(id+"F0.wireOp",EDGE,"E1344"),sQuery(id+"F0.wireOp",EDGE,"E1345"),sQuery(id+"F0.wireOp",EDGE,"E1346"),sQuery(id+"F0.wireOp",EDGE,"E1347"),sQuery(id+"F0.wireOp",EDGE,"E1348"),sQuery(id+"F0.wireOp",EDGE,"E1358"),sQuery(id+"F0.wireOp",EDGE,"E1359"),sQuery(id+"F0.wireOp",EDGE,"E1360"),sQuery(id+"F0.wireOp",EDGE,"E1361"),sQuery(id+"F0.wireOp",EDGE,"E1362"),sQuery(id+"F0.wireOp",EDGE,"E1363"),sQuery(id+"F0.wireOp",EDGE,"E1374"),sQuery(id+"F0.wireOp",EDGE,"E1375"),sQuery(id+"F0.wireOp",EDGE,"E1376"),sQuery(id+"F0.wireOp",EDGE,"E1377"),sQuery(id+"F0.wireOp",EDGE,"E1378"),sQuery(id+"F0.wireOp",EDGE,"E1379"),sQuery(id+"F0.wireOp",EDGE,"E1389"),sQuery(id+"F0.wireOp",EDGE,"E1390"),sQuery(id+"F0.wireOp",EDGE,"E1391"),sQuery(id+"F0.wireOp",EDGE,"E1392"),sQuery(id+"F0.wireOp",EDGE,"E1393"),sQuery(id+"F0.wireOp",EDGE,"E1394"),sQuery(id+"F0.wireOp",EDGE,"E1404"),sQuery(id+"F0.wireOp",EDGE,"E1405"),sQuery(id+"F0.wireOp",EDGE,"E1406"),sQuery(id+"F0.wireOp",EDGE,"E1407"),sQuery(id+"F0.wireOp",EDGE,"E1408"),sQuery(id+"F0.wireOp",EDGE,"E1409"),sQuery(id+"F0.wireOp",EDGE,"E1419"),sQuery(id+"F0.wireOp",EDGE,"E1420"),sQuery(id+"F0.wireOp",EDGE,"E1421"),sQuery(id+"F0.wireOp",EDGE,"E1422"),sQuery(id+"F0.wireOp",EDGE,"E1423"),sQuery(id+"F0.wireOp",EDGE,"E1424"),sQuery(id+"F0.wireOp",EDGE,"E1434"),sQuery(id+"F0.wireOp",EDGE,"E1435"),sQuery(id+"F0.wireOp",EDGE,"E1436"),sQuery(id+"F0.wireOp",EDGE,"E1437"),sQuery(id+"F0.wireOp",EDGE,"E1438"),sQuery(id+"F0.wireOp",EDGE,"E1439"),sQuery(id+"F0.wireOp",EDGE,"E1449"),sQuery(id+"F0.wireOp",EDGE,"E1450"),sQuery(id+"F0.wireOp",EDGE,"E1451"),sQuery(id+"F0.wireOp",EDGE,"E1452"),sQuery(id+"F0.wireOp",EDGE,"E1453"),sQuery(id+"F0.wireOp",EDGE,"E1454"),sQuery(id+"F0.wireOp",EDGE,"ee3eb250-1661-4155-86ec-dae5921570f0"),sQuery(id+"F0.wireOp",EDGE,"41b0b4bd-b274-45d1-b67e-6795481cb549"),sQuery(id+"F0.wireOp",EDGE,"dd59f366-ba7d-4e5a-bf2b-2efbbdece830"),sQuery(id+"F0.wireOp",EDGE,"e15401b2-9218-4683-a37e-0150a1617781"),sQuery(id+"F0.wireOp",EDGE,"c8841f8c-7797-46fb-a8c1-38bbecde44fd"),sQuery(id+"F0.wireOp",EDGE,"f2f586a9-af0c-4e53-85e5-e688b2b667e0"),sQuery(id+"F0.wireOp",EDGE,"E1474.bottom"),sQuery(id+"F0.wireOp",EDGE,"E1474.top"),sQuery(id+"F0.wireOp",EDGE,"E1474.left"),sQuery(id+"F0.wireOp",EDGE,"E1474.right")])],"isStart":false});
            var sketch = newSketch(context, id + "F2", { "sketchPlane" : qUnion([Q0])});
            skPoint(sketch, "E1475", {"position": v(12.11, 9) * mm});
            skPoint(sketch, "E1476", {"position": v(27.11, 9) * mm});
            skPoint(sketch, "E1477", {"position": v(7.5, -2) * mm});
            skPoint(sketch, "E1477.positionSnap0", {"position": v(7.5, 0) * mm});
            skPoint(sketch, "E1478", {"position": v(31.73, -2) * mm});
            skPoint(sketch, "E1478.positionSnap0", {"position": v(31.73, 0) * mm});
            skLineSegment(sketch, "E1479", {"start": v(12.11, 9) * mm, "end": v(27.11, 9) * mm});
            skLineSegment(sketch, "E1480", {"start": v(12.11, 9) * mm, "end": v(18.46, -2) * mm});
            skPoint(sketch, "E1481", {"position": v(2.89, 9) * mm});
            skLineSegment(sketch, "E1482", {"start": v(2.89, 9) * mm, "end": v(-3.46, -2) * mm});
            skLineSegment(sketch, "E1483", {"start": v(-3.46, -2) * mm, "end": v(18.46, -2) * mm});
            skLineSegment(sketch, "E1484", {"start": v(20.76, -2) * mm, "end": v(42.7, -2) * mm});
            skLineSegment(sketch, "E1485", {"start": v(36.34, 9) * mm, "end": v(51.34, 9) * mm});
            skPoint(sketch, "E1486", {"position": v(36.34, 9) * mm});
            skPoint(sketch, "E1487", {"position": v(51.34, 9) * mm});
            skPoint(sketch, "E1488", {"position": v(60.57, 9) * mm});
            skPoint(sketch, "E1489", {"position": v(75.57, 9) * mm});
            skPoint(sketch, "E1490", {"position": v(84.8, 9) * mm});
            skPoint(sketch, "E1491", {"position": v(99.8, 9) * mm});
            skPoint(sketch, "E1492", {"position": v(109.02, 9) * mm});
            skPoint(sketch, "E1493", {"position": v(124.02, 9) * mm});
            skPoint(sketch, "E1494", {"position": v(133.25, 9) * mm});
            skLineSegment(sketch, "E1495", {"start": v(27.11, 9) * mm, "end": v(20.76, -2) * mm});
            skLineSegment(sketch, "E1496", {"start": v(36.34, 9) * mm, "end": v(42.7, -2) * mm});
            skLineSegment(sketch, "E1497", {"start": v(51.34, 9) * mm, "end": v(44.99, -2) * mm});
            skLineSegment(sketch, "E1498", {"start": v(60.57, 9) * mm, "end": v(66.92, -2) * mm});
            skLineSegment(sketch, "E1499", {"start": v(75.57, 9) * mm, "end": v(69.22, -2) * mm});
            skLineSegment(sketch, "E1500", {"start": v(84.8, 9) * mm, "end": v(91.14, -2) * mm});
            skLineSegment(sketch, "E1501", {"start": v(99.8, 9) * mm, "end": v(93.44, -2) * mm});
            skLineSegment(sketch, "E1502", {"start": v(93.44, -2) * mm, "end": v(93.36, -1.45) * mm});
            skLineSegment(sketch, "E1503", {"start": v(109.02, 9) * mm, "end": v(115.37, -2) * mm});
            skLineSegment(sketch, "E1504", {"start": v(115.37, -2) * mm, "end": v(114.76, -1.64) * mm});
            skLineSegment(sketch, "E1505", {"start": v(124.02, 9) * mm, "end": v(117.67, -2) * mm});
            skLineSegment(sketch, "E1506", {"start": v(133.25, 9) * mm, "end": v(139.6, -2) * mm});
            skPoint(sketch, "E1507", {"position": v(-1.73, 21) * mm});
            skPoint(sketch, "E1508", {"position": v(0.82, 14.59) * mm});
            skLineSegment(sketch, "E1509", {"start": v(0.82, 14.59) * mm, "end": v(3.46, 10) * mm});
            skLineSegment(sketch, "E1510", {"start": v(2.89, 9) * mm, "end": v(3.46, 10) * mm});
            skLineSegment(sketch, "E1511", {"start": v(0.82, 14.59) * mm, "end": v(-2.89, 21) * mm});
            skLineSegment(sketch, "E1512", {"start": v(-2.89, 21) * mm, "end": v(3.92, 32.78) * mm});
            skLineSegment(sketch, "E1513", {"start": v(3.92, 32.78) * mm, "end": v(-2.89, 44.56) * mm});
            skLineSegment(sketch, "E1514", {"start": v(-2.89, 44.56) * mm, "end": v(3.46, 55.56) * mm});
            skLineSegment(sketch, "E1515", {"start": v(3.46, 55.56) * mm, "end": v(-2.89, 66.56) * mm});
            skLineSegment(sketch, "E1516", {"start": v(-2.89, 66.56) * mm, "end": v(3.01, 76.78) * mm});
            skLineSegment(sketch, "E1517", {"start": v(3.01, 76.78) * mm, "end": v(-2.89, 87) * mm});
            skLineSegment(sketch, "E1518", {"start": v(-2.89, 87) * mm, "end": v(3.46, 98) * mm});
            skLineSegment(sketch, "E1519", {"start": v(3.46, 98) * mm, "end": v(-2.89, 109) * mm});
            skLineSegment(sketch, "E1520", {"start": v(-2.89, 109) * mm, "end": v(3.46, 120) * mm});
            skLineSegment(sketch, "E1521", {"start": v(3.46, 120) * mm, "end": v(-2.89, 131) * mm});
            skLineSegment(sketch, "E1522", {"start": v(-2.89, 131) * mm, "end": v(3.46, 142) * mm});
            skLineSegment(sketch, "E1523", {"start": v(3.46, 142) * mm, "end": v(-2.89, 153) * mm});
            skLineSegment(sketch, "E1524", {"start": v(-2.89, 153) * mm, "end": v(3.46, 164) * mm});
            skLineSegment(sketch, "E1525", {"start": v(3.46, 164) * mm, "end": v(-2.89, 175) * mm});
            skLineSegment(sketch, "E1526.trimOffspring", {"start": v(44.99, -2) * mm, "end": v(66.92, -2) * mm});
            skLineSegment(sketch, "E1527.trimOffspring", {"start": v(69.22, -2) * mm, "end": v(91.14, -2) * mm});
            skLineSegment(sketch, "E1528.trimOffspring", {"start": v(93.44, -2) * mm, "end": v(115.37, -2) * mm});
            skLineSegment(sketch, "E1529.trimOffspring", {"start": v(60.57, 9) * mm, "end": v(75.57, 9) * mm});
            skLineSegment(sketch, "E1530.trimOffspring", {"start": v(84.8, 9) * mm, "end": v(99.8, 9) * mm});
            skLineSegment(sketch, "E1531.trimOffspring", {"start": v(109.02, 9) * mm, "end": v(124.02, 9) * mm});
            skLineSegment(sketch, "E1532.trimOffspring", {"start": v(117.67, -2) * mm, "end": v(139.6, -2) * mm});
            skPoint(sketch, "E1533", {"position": v(144.78, 21) * mm});
            skPoint(sketch, "E1534", {"position": v(5.77, 10) * mm});
            skPoint(sketch, "E1535", {"position": v(136.13, 176) * mm});
            skPoint(sketch, "E1536", {"position": v(121.13, 176) * mm});
            skPoint(sketch, "E1537", {"position": v(116.52, 187) * mm});
            skPoint(sketch, "E1537.positionSnap0", {"position": v(116.52, 185) * mm});
            skLineSegment(sketch, "E1538", {"start": v(136.13, 176) * mm, "end": v(121.13, 176) * mm});
            skPoint(sketch, "E1539", {"position": v(145.36, 176) * mm});
            skLineSegment(sketch, "E1540", {"start": v(127.48, 187) * mm, "end": v(105.56, 187) * mm});
            skLineSegment(sketch, "E1541", {"start": v(111.9, 176) * mm, "end": v(96.9, 176) * mm});
            skPoint(sketch, "E1542", {"position": v(111.9, 176) * mm});
            skPoint(sketch, "E1543", {"position": v(96.9, 176) * mm});
            skPoint(sketch, "E1544", {"position": v(87.68, 176) * mm});
            skPoint(sketch, "E1545", {"position": v(72.68, 176) * mm});
            skPoint(sketch, "E1546", {"position": v(63.45, 176) * mm});
            skPoint(sketch, "E1547", {"position": v(48.45, 176) * mm});
            skPoint(sketch, "E1548", {"position": v(39.23, 176) * mm});
            skPoint(sketch, "E1549", {"position": v(24.23, 176) * mm});
            skPoint(sketch, "E1550", {"position": v(15, 176) * mm});
            skPoint(sketch, "E1551", {"position": v(0, 176) * mm});
            skLineSegment(sketch, "E1552", {"start": v(121.13, 176) * mm, "end": v(127.48, 187) * mm});
            skLineSegment(sketch, "E1553", {"start": v(111.9, 176) * mm, "end": v(105.56, 187) * mm});
            skLineSegment(sketch, "E1554", {"start": v(96.9, 176) * mm, "end": v(103.26, 187) * mm});
            skLineSegment(sketch, "E1555", {"start": v(87.68, 176) * mm, "end": v(81.33, 187) * mm});
            skLineSegment(sketch, "E1556", {"start": v(72.68, 176) * mm, "end": v(79.03, 187) * mm});
            skLineSegment(sketch, "E1557", {"start": v(63.45, 176) * mm, "end": v(57.1, 187) * mm});
            skLineSegment(sketch, "E1558", {"start": v(48.45, 176) * mm, "end": v(54.8, 187) * mm});
            skLineSegment(sketch, "E1559", {"start": v(54.8, 187) * mm, "end": v(54.9, 186.45) * mm});
            skLineSegment(sketch, "E1560", {"start": v(39.23, 176) * mm, "end": v(32.88, 187) * mm});
            skLineSegment(sketch, "E1561", {"start": v(32.88, 187) * mm, "end": v(33.49, 186.64) * mm});
            skLineSegment(sketch, "E1562", {"start": v(24.23, 176) * mm, "end": v(30.58, 187) * mm});
            skLineSegment(sketch, "E1563", {"start": v(15, 176) * mm, "end": v(8.65, 187) * mm});
            skLineSegment(sketch, "E1564.trimOffspring", {"start": v(103.26, 187) * mm, "end": v(81.33, 187) * mm});
            skLineSegment(sketch, "E1565.trimOffspring", {"start": v(79.03, 187) * mm, "end": v(57.1, 187) * mm});
            skLineSegment(sketch, "E1566.trimOffspring", {"start": v(54.8, 187) * mm, "end": v(32.88, 187) * mm});
            skLineSegment(sketch, "E1567.trimOffspring", {"start": v(87.68, 176) * mm, "end": v(72.68, 176) * mm});
            skLineSegment(sketch, "E1568.trimOffspring", {"start": v(63.45, 176) * mm, "end": v(48.45, 176) * mm});
            skLineSegment(sketch, "E1569.trimOffspring", {"start": v(39.23, 176) * mm, "end": v(24.23, 176) * mm});
            skLineSegment(sketch, "E1570.trimOffspring", {"start": v(15, 176) * mm, "end": v(-3.46, 176) * mm});
            skLineSegment(sketch, "E1571.trimOffspring", {"start": v(30.58, 187) * mm, "end": v(8.65, 187) * mm});
            skPoint(sketch, "E1572", {"position": v(142.47, 175) * mm});
            skLineSegment(sketch, "E1573", {"start": v(-0.24, 170.41) * mm, "end": v(-2.89, 175) * mm});
            skLineSegment(sketch, "E1574", {"start": v(-2.89, 175) * mm, "end": v(-3.46, 176) * mm});
            skLineSegment(sketch, "E1575.bottom", {"start": v(-78.84, 213.16) * mm, "end": v(237.71, 213.16) * mm});
            skLineSegment(sketch, "E1575.top", {"start": v(-78.84, -25.35) * mm, "end": v(237.71, -25.35) * mm});
            skLineSegment(sketch, "E1575.left", {"start": v(-78.84, 213.16) * mm, "end": v(-78.84, -25.35) * mm});
            skLineSegment(sketch, "E1575.right", {"start": v(237.71, 213.16) * mm, "end": v(237.71, -25.35) * mm});
            skLineSegment(sketch, "E1576", {"start": v(139.02, 21) * mm, "end": v(132.67, 10) * mm});
            skLineSegment(sketch, "E1577", {"start": v(133.8, 8.03) * mm, "end": v(132.67, 10) * mm});
            skLineSegment(sketch, "E1578", {"start": v(139.02, 21) * mm, "end": v(132.1, 33) * mm});
            skLineSegment(sketch, "E1579", {"start": v(139.02, 43) * mm, "end": v(132.67, 32) * mm});
            skLineSegment(sketch, "E1580", {"start": v(139.02, 43) * mm, "end": v(132.1, 55) * mm});
            skLineSegment(sketch, "E1581", {"start": v(132.1, 55) * mm, "end": v(131.49, 54.41) * mm});
            skLineSegment(sketch, "E1582", {"start": v(139.02, 65) * mm, "end": v(132.67, 54) * mm});
            skLineSegment(sketch, "E1583", {"start": v(139.02, 65) * mm, "end": v(132.1, 77) * mm});
            skLineSegment(sketch, "E1584", {"start": v(139.02, 87) * mm, "end": v(132.67, 76) * mm});
            skLineSegment(sketch, "E1585", {"start": v(139.02, 87) * mm, "end": v(132.1, 99) * mm});
            skLineSegment(sketch, "E1586", {"start": v(132.1, 99) * mm, "end": v(131.78, 98.47) * mm});
            skLineSegment(sketch, "E1587", {"start": v(139.02, 109) * mm, "end": v(132.67, 98) * mm});
            skLineSegment(sketch, "E1588", {"start": v(139.02, 109) * mm, "end": v(132.08, 121.03) * mm});
            skLineSegment(sketch, "E1589", {"start": v(139.02, 131) * mm, "end": v(132.67, 120) * mm});
            skLineSegment(sketch, "E1590", {"start": v(139.02, 131) * mm, "end": v(132.1, 143) * mm});
            skLineSegment(sketch, "E1591", {"start": v(139.02, 153) * mm, "end": v(132.67, 142) * mm});
            skLineSegment(sketch, "E1592", {"start": v(132.67, 142) * mm, "end": v(132.75, 141.67) * mm});
            skLineSegment(sketch, "E1593", {"start": v(139.02, 153) * mm, "end": v(132.67, 164) * mm});
            skLineSegment(sketch, "E1594", {"start": v(139.02, 175) * mm, "end": v(132.67, 164) * mm});
            skLineSegment(sketch, "E1595", {"start": v(132.67, 164) * mm, "end": v(139.6, 176) * mm});
            skLineSegment(sketch, "E1596", {"start": v(139.6, 176) * mm, "end": v(136.13, 176) * mm});
            skPoint(sketch, "E1597.orphan", {"position": v(132.1, 165) * mm});
            skSolve(sketch);
        }
        {
            var Q0;
            Q0 = qSketchRegion(id + "F2", true);
            extrude(context, id + "F3", {"entities" : qUnion([Q0]), "operationType" : NewBodyOperationType.REMOVE, "oppositeDirection" : true, "depth" : 50 * mm, "offsetDistance" : 25 * mm});
        }
    });
